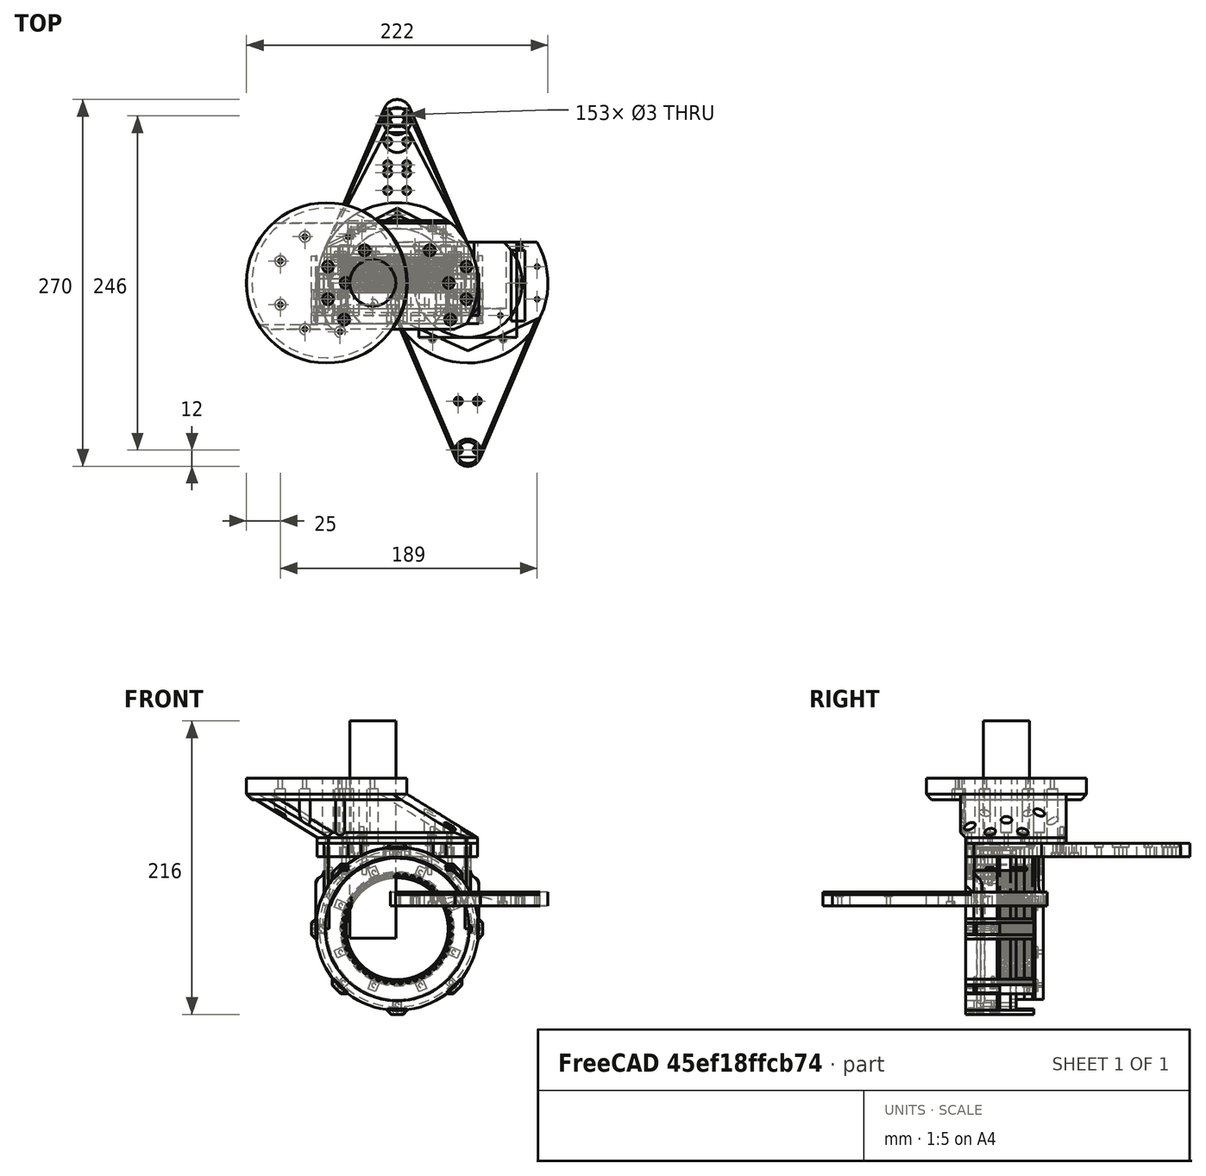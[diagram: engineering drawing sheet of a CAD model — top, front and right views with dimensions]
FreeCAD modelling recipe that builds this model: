
FCSTD DOCUMENT  (FreeCAD 0.19R24276 (Git))
Label: Base_triangle_014
License: All rights reserved
LicenseURL: http://en.wikipedia.org/wiki/All_rights_reserved
objects: Part::Cylinder×647, Part::Compound×283, Part::Cut×229, Part::Box×183, Part::Chamfer×32, Part::FeaturePython×15, Part::Fillet×14, Sketcher::SketchObject×7, PartDesign::Pad×6, PartDesign::Body×6, Part::Common×3, Mesh::Feature×2, Part::Torus×1, Part::Extrusion×1
note: 1433 computed .brp shape members not serialized (recipe doc carries the construction recipe); baked Part::Feature solids carry a one-line shape summary decoded from their .brp

FEATURE [Part::Cylinder] Cylinder284  label="Válec284"
  Angle = 360
  AttacherType = Attacher::AttachEngine3D
  Height = 10
  Placement = pos=(0,106,0) rot=(0,0,1;0rad)
  Radius = 10
FEATURE [Part::Box] Box135  label="Krychle135"
  AttacherType = Attacher::AttachEngine3D
  Height = 32
  Length = 200
  Placement = pos=(-100,-124,0) rot=(0,0,1;0rad)
  Width = 100
FEATURE [Part::Box] Box136  label="Krychle136"
  AttacherType = Attacher::AttachEngine3D
  Height = 10
  Length = 10
  Placement = pos=(32,-24,0) rot=(0,0,1;0rad)
  Width = 52
FEATURE [Part::FeaturePython] Tube  # WARN: FeaturePython — macro-defined, semantics opaque (R4)
  AttacherType = Attacher::AttachEngine3D
  Height = 10
  InnerRadius = 40
  OuterRadius = 59
FEATURE [Part::Cylinder] Cylinder292  label="Válec292"
  Angle = 360
  AttacherType = Attacher::AttachEngine3D
  Height = 100
  Placement = pos=(51,-12,0) rot=(0,0,1;0rad)
  Radius = 1.5
FEATURE [Part::Cylinder] Cylinder312  label="Válec312"
  Angle = 360
  AttacherType = Attacher::AttachEngine3D
  Height = 4
  Placement = pos=(34,36,-1) rot=(0,0,1;0rad)
  Radius = 3
FEATURE [Part::Cylinder] Cylinder311  label="Válec311"
  Angle = 360
  AttacherType = Attacher::AttachEngine3D
  Height = 4
  Placement = pos=(-34,36,-1) rot=(0,0,1;0rad)
  Radius = 3
FEATURE [Part::Compound] Compound290
  Links = -> [Cylinder312,Cylinder311]
FEATURE [Part::Cut] Cut136
  Base = -> Tube
  Tool = -> Compound290
FEATURE [Part::Box] Box137  label="Krychle137"
  AttacherType = Attacher::AttachEngine3D
  Height = 10
  Length = 10
  Placement = pos=(-42,-24,0) rot=(0,0,1;0rad)
  Width = 52
FEATURE [Part::Box] Box138  label="Krychle138"
  AttacherType = Attacher::AttachEngine3D
  Height = 10
  Length = 72
  Placement = pos=(-36,10,0) rot=(0,0,1;0rad)
  Width = 34
FEATURE [Part::Cylinder] Cylinder291  label="Válec291"
  Angle = 360
  AttacherType = Attacher::AttachEngine3D
  Height = 100
  Placement = pos=(-51,-12,0) rot=(0,0,1;0rad)
  Radius = 1.5
FEATURE [Part::Compound] Compound292
  Links = -> [Cylinder291,Cylinder292]
FEATURE [Part::Cylinder] Cylinder324  label="Válec324"
  Angle = 360
  AttacherType = Attacher::AttachEngine3D
  Height = 4
  Placement = pos=(51,7,0) rot=(0,0,1;0rad)
  Radius = 3
FEATURE [Part::Cylinder] Cylinder325  label="Válec325"
  Angle = 360
  AttacherType = Attacher::AttachEngine3D
  Height = 4
  Placement = pos=(-24,18,0) rot=(0,0,1;0rad)
  Radius = 3
FEATURE [Part::Cylinder] Cylinder326  label="Válec326"
  Angle = 360
  AttacherType = Attacher::AttachEngine3D
  Height = 4
  Placement = pos=(24,18,0) rot=(0,0,1;0rad)
  Radius = 3
FEATURE [Part::Cylinder] Cylinder315  label="Válec315"
  Angle = 360
  AttacherType = Attacher::AttachEngine3D
  Height = 4
  Placement = pos=(-51,-16,0) rot=(0,0,1;0rad)
  Radius = 3
FEATURE [Part::Cylinder] Cylinder314  label="Válec314"
  Angle = 360
  AttacherType = Attacher::AttachEngine3D
  Height = 50
  Placement = pos=(-34,36,0) rot=(0,0,1;0rad)
  Radius = 1.5
FEATURE [Part::Cylinder] Cylinder328  label="Válec328"
  Angle = 360
  AttacherType = Attacher::AttachEngine3D
  Height = 50
  Placement = pos=(-51,6,0) rot=(0,0,1;0rad)
  Radius = 1.5
FEATURE [Part::Cylinder] Cylinder327  label="Válec327"
  Angle = 360
  AttacherType = Attacher::AttachEngine3D
  Height = 4
  Placement = pos=(-24,18,0) rot=(0,0,1;0rad)
  Radius = 3
FEATURE [Part::Cylinder] Cylinder319  label="Válec319"
  Angle = 360
  AttacherType = Attacher::AttachEngine3D
  Height = 50
  Placement = pos=(51,6,0) rot=(0,0,1;0rad)
  Radius = 1.5
FEATURE [Part::Cylinder] Cylinder313  label="Válec313"
  Angle = 360
  AttacherType = Attacher::AttachEngine3D
  Height = 50
  Placement = pos=(34,36,0) rot=(0,0,1;0rad)
  Radius = 1.5
FEATURE [Part::Compound] Compound291
  Links = -> [Cylinder314,Cylinder313]
FEATURE [Part::Cylinder] Cylinder323  label="Válec323"
  Angle = 360
  AttacherType = Attacher::AttachEngine3D
  Height = 4
  Placement = pos=(-51,7,0) rot=(0,0,1;0rad)
  Radius = 3
FEATURE [Part::Compound] Compound296
  Links = -> [Cylinder324,Cylinder323,Cylinder325,Cylinder326]
  Placement = pos=(0,0,8) rot=(0,0,1;0rad)
FEATURE [Part::Cylinder] Cylinder329  label="Válec329"
  Angle = 360
  AttacherType = Attacher::AttachEngine3D
  Height = 50
  Placement = pos=(51,6,0) rot=(0,0,1;0rad)
  Radius = 1.5
FEATURE [Part::Cylinder] Cylinder330  label="Válec330"
  Angle = 360
  AttacherType = Attacher::AttachEngine3D
  Height = 50
  Placement = pos=(-24,18,0) rot=(0,0,1;0rad)
  Radius = 1.5
FEATURE [Part::Cylinder] Cylinder316  label="Válec316"
  Angle = 360
  AttacherType = Attacher::AttachEngine3D
  Height = 4
  Placement = pos=(51,-16,0) rot=(0,0,1;0rad)
  Radius = 3
FEATURE [Part::Compound] Compound293
  Links = -> [Cylinder315,Cylinder316]
  Placement = pos=(0,0,25) rot=(0,0,1;0rad)
FEATURE [Part::Cylinder] Cylinder320  label="Válec320"
  Angle = 360
  AttacherType = Attacher::AttachEngine3D
  Height = 50
  Placement = pos=(-51,6,0) rot=(0,0,1;0rad)
  Radius = 1.5
FEATURE [Part::Cylinder] Cylinder321  label="Válec321"
  Angle = 360
  AttacherType = Attacher::AttachEngine3D
  Height = 50
  Placement = pos=(-24,18,0) rot=(0,0,1;0rad)
  Radius = 1.5
FEATURE [Part::Cylinder] Cylinder322  label="Válec322"
  Angle = 360
  AttacherType = Attacher::AttachEngine3D
  Height = 50
  Placement = pos=(24,18,0) rot=(0,0,1;0rad)
  Radius = 1.5
FEATURE [Part::Compound] Compound295
  Links = -> [Cylinder319,Cylinder320,Cylinder321,Cylinder322]
FEATURE [Part::Cut] Cut137
  Base = -> Cut136
  Tool = -> Compound291
FEATURE [Part::Cut] Cut138
  Base = -> Cut137
  Tool = -> Compound293
FEATURE [Part::Cut] Cut139
  Base = -> Cut138
  Tool = -> Compound292
FEATURE [Part::Cylinder] Cylinder334  label="Válec334"
  Angle = 360
  AttacherType = Attacher::AttachEngine3D
  Height = 4
  Placement = pos=(24,18,0) rot=(0,0,1;0rad)
  Radius = 3
FEATURE [Part::Compound] Compound298
  Links = -> [Cylinder327,Cylinder334]
  Placement = pos=(0,0,7) rot=(0,0,1;0rad)
FEATURE [Part::Cut] Cut142
  Base = -> Cut139
  Tool = -> Compound298
FEATURE [Part::Cylinder] Cylinder331  label="Válec331"
  Angle = 360
  AttacherType = Attacher::AttachEngine3D
  Height = 50
  Placement = pos=(24,18,0) rot=(0,0,1;0rad)
  Radius = 1.5
FEATURE [Part::Compound] Compound297
  Links = -> [Cylinder329,Cylinder328,Cylinder330,Cylinder331]
FEATURE [Part::Cut] Cut143
  Base = -> Cut142
  Tool = -> Compound297
FEATURE [Part::Cut] Cut144
  Base = -> Cut143
  Tool = -> Box135
FEATURE [Part::Cylinder] Cylinder297  label="Válec297"
  Angle = 360
  AttacherType = Attacher::AttachEngine3D
  Height = 4
  Placement = pos=(34,36,-1) rot=(0,0,1;0rad)
  Radius = 3
FEATURE [Part::Cylinder] Cylinder363  label="Válec363"
  Angle = 360
  AttacherType = Attacher::AttachEngine3D
  Height = 4
  Placement = pos=(0,50,-1) rot=(0,0,1;0rad)
  Radius = 3
FEATURE [Part::Cut] Cut153
  Base = -> Cut144
  Tool = -> Cylinder363
FEATURE [Part::Cylinder] Cylinder364  label="Válec364"
  Angle = 360
  AttacherType = Attacher::AttachEngine3D
  Height = 50
  Placement = pos=(0,50,0) rot=(0,0,1;0rad)
  Radius = 1.5
FEATURE [Part::Cut] Cut154
  Base = -> Cut153
  Tool = -> Cylinder364
FEATURE [Part::Cylinder] Cylinder298  label="Válec298"
  Angle = 360
  AttacherType = Attacher::AttachEngine3D
  Height = 4
  Placement = pos=(-34,36,-1) rot=(0,0,1;0rad)
  Radius = 3
FEATURE [Part::Compound] Compound282
  Links = -> [Cylinder298,Cylinder297]
FEATURE [Part::Cut] Cut131
  Base = -> Box138
  Tool = -> Compound282
FEATURE [Part::Cylinder] Cylinder294  label="Válec294"
  Angle = 360
  AttacherType = Attacher::AttachEngine3D
  Height = 50
  Placement = pos=(-34,36,0) rot=(0,0,1;0rad)
  Radius = 1.5
FEATURE [Part::Cylinder] Cylinder293  label="Válec293"
  Angle = 360
  AttacherType = Attacher::AttachEngine3D
  Height = 50
  Placement = pos=(34,36,0) rot=(0,0,1;0rad)
  Radius = 1.5
FEATURE [Part::Compound] Compound284
  Links = -> [Cylinder294,Cylinder293]
FEATURE [Part::Cut] Cut132
  Base = -> Cut131
  Tool = -> Compound284
FEATURE [Part::Cut] Cut140
  Base = -> Cut132
  Tool = -> Compound296
FEATURE [Part::Cut] Cut141
  Base = -> Cut140
  Tool = -> Compound295
FEATURE [Part::Cylinder] Cylinder424  label="Válec424"
  Angle = 360
  AttacherType = Attacher::AttachEngine3D
  Height = 4
  Placement = pos=(-7,-34,73) rot=(1,0,0;1.5708rad)
  Radius = 3
FEATURE [Part::Cylinder] Cylinder413  label="Válec413"
  Angle = 360
  AttacherType = Attacher::AttachEngine3D
  Height = 20
  Placement = pos=(7,-34,37) rot=(1,0,0;1.5708rad)
  Radius = 1.5
FEATURE [Part::Cylinder] Cylinder414  label="Válec414"
  Angle = 360
  AttacherType = Attacher::AttachEngine3D
  Height = 20
  Placement = pos=(7,-34,73) rot=(1,0,0;1.5708rad)
  Radius = 1.5
FEATURE [Part::Cylinder] Cylinder415  label="Válec415"
  Angle = 360
  AttacherType = Attacher::AttachEngine3D
  Height = 20
  Placement = pos=(-7,-34,37) rot=(1,0,0;1.5708rad)
  Radius = 1.5
FEATURE [Part::Cylinder] Cylinder412  label="Válec412"
  Angle = 360
  AttacherType = Attacher::AttachEngine3D
  Height = 20
  Placement = pos=(-7,-34,73) rot=(1,0,0;1.5708rad)
  Radius = 1.5
FEATURE [Part::Compound] Compound317
  Links = -> [Cylinder413,Cylinder415,Cylinder414,Cylinder412]
  Placement = pos=(0,141,45) rot=(1,0,0;1.5708rad)
FEATURE [Part::Cut] Cut166
  Base = -> Cylinder284
  Tool = -> Compound317
FEATURE [Part::Cylinder] Cylinder427  label="Válec427"
  Angle = 360
  AttacherType = Attacher::AttachEngine3D
  Height = 4
  Placement = pos=(-7,-34,37) rot=(1,0,0;1.5708rad)
  Radius = 3
FEATURE [Part::Cylinder] Cylinder426  label="Válec426"
  Angle = 360
  AttacherType = Attacher::AttachEngine3D
  Height = 4
  Placement = pos=(7,-34,73) rot=(1,0,0;1.5708rad)
  Radius = 3
FEATURE [Part::Cylinder] Cylinder425  label="Válec425"
  Angle = 360
  AttacherType = Attacher::AttachEngine3D
  Height = 4
  Placement = pos=(7,-34,37) rot=(1,0,0;1.5708rad)
  Radius = 3
FEATURE [Part::Compound] Compound320
  Links = -> [Cylinder425,Cylinder427,Cylinder426,Cylinder424]
  Placement = pos=(0,141,45) rot=(1,0,0;1.5708rad)
FEATURE [Part::Cut] Cut168
  Base = -> Cut166
  Tool = -> Compound320
FEATURE [Sketcher::SketchObject] Sketch
  FullyConstrained = false
  MapMode = 5
  Support = -> [XY_Plane]
  sketch-geometry (5):
    g0: LineSegment StartX=-51.8839 StartY=28.0157 StartZ=0 EndX=-8.82571 EndY=110.528 EndZ=0
    g1: LineSegment StartX=-8.82571 StartY=110.528 StartZ=0 EndX=8.88346 EndY=110.528 EndZ=0
    g2: LineSegment StartX=8.88346 StartY=110.528 StartZ=0 EndX=51.7746 EndY=28.1985 EndZ=0
    g3: LineSegment StartX=51.7746 StartY=28.1985 StartZ=0 EndX=0 EndY=55.1408 EndZ=0
    g4: LineSegment StartX=0 StartY=55.1408 StartZ=0 EndX=-51.8839 EndY=28.0157 EndZ=0
  constraints (7):
    c: Coincident(g0,g1)
    c: Horizontal(g1)
    c: Coincident(g1,g2)
    c: Coincident(g2,g3)
    c: PointOnObject(g3,g-2)
    c: Coincident(g3,g4)
    c: Coincident(g4,g0)
FEATURE [PartDesign::Pad] Pad
  Direction = (1,1,1)
  Length = 10
  Length2 = 100
  Profile = -> Sketch
  Type = 0
FEATURE [PartDesign::Body] Body
  Group = -> [Sketch,Pad]
  Origin = -> Origin
  Tip = -> Pad
FEATURE [Part::Cylinder] Cylinder307  label="Válec307"
  Angle = 360
  AttacherType = Attacher::AttachEngine3D
  Height = 4
  Placement = pos=(-34,36,-1) rot=(0,0,1;0rad)
  Radius = 3
FEATURE [Part::Cylinder] Cylinder308  label="Válec308"
  Angle = 360
  AttacherType = Attacher::AttachEngine3D
  Height = 4
  Placement = pos=(34,36,-1) rot=(0,0,1;0rad)
  Radius = 3
FEATURE [Part::Compound] Compound288
  Links = -> [Cylinder308,Cylinder307]
FEATURE [Part::Cut] Cut134
  Base = -> Body
  Tool = -> Compound288
FEATURE [Part::Cylinder] Cylinder309  label="Válec309"
  Angle = 360
  AttacherType = Attacher::AttachEngine3D
  Height = 50
  Placement = pos=(34,36,0) rot=(0,0,1;0rad)
  Radius = 1.5
FEATURE [Part::Cylinder] Cylinder310  label="Válec310"
  Angle = 360
  AttacherType = Attacher::AttachEngine3D
  Height = 50
  Placement = pos=(-34,36,0) rot=(0,0,1;0rad)
  Radius = 1.5
FEATURE [Part::Compound] Compound289
  Links = -> [Cylinder310,Cylinder309]
FEATURE [Part::Cut] Cut135
  Base = -> Cut134
  Tool = -> Compound289
FEATURE [Part::Cylinder] Cylinder421  label="Válec421"
  Angle = 360
  AttacherType = Attacher::AttachEngine3D
  Height = 4
  Placement = pos=(7,-34,37) rot=(1,0,0;1.5708rad)
  Radius = 3
FEATURE [Part::Cylinder] Cylinder419  label="Válec419"
  Angle = 360
  AttacherType = Attacher::AttachEngine3D
  Height = 20
  Placement = pos=(-7,-34,37) rot=(1,0,0;1.5708rad)
  Radius = 1.5
FEATURE [Part::Cylinder] Cylinder417  label="Válec417"
  Angle = 360
  AttacherType = Attacher::AttachEngine3D
  Height = 20
  Placement = pos=(7,-34,37) rot=(1,0,0;1.5708rad)
  Radius = 1.5
FEATURE [Part::Cylinder] Cylinder418  label="Válec418"
  Angle = 360
  AttacherType = Attacher::AttachEngine3D
  Height = 20
  Placement = pos=(7,-34,73) rot=(1,0,0;1.5708rad)
  Radius = 1.5
FEATURE [Part::Cylinder] Cylinder416  label="Válec416"
  Angle = 360
  AttacherType = Attacher::AttachEngine3D
  Height = 20
  Placement = pos=(-7,-34,73) rot=(1,0,0;1.5708rad)
  Radius = 1.5
FEATURE [Part::Compound] Compound318
  Links = -> [Cylinder417,Cylinder419,Cylinder418,Cylinder416]
  Placement = pos=(0,141,45) rot=(1,0,0;1.5708rad)
FEATURE [Part::Cut] Cut165
  Base = -> Cut135
  Tool = -> Compound318
FEATURE [Part::Cylinder] Cylinder420  label="Válec420"
  Angle = 360
  AttacherType = Attacher::AttachEngine3D
  Height = 4
  Placement = pos=(-7,-34,73) rot=(1,0,0;1.5708rad)
  Radius = 3
FEATURE [Part::Cylinder] Cylinder423  label="Válec423"
  Angle = 360
  AttacherType = Attacher::AttachEngine3D
  Height = 4
  Placement = pos=(-7,-34,37) rot=(1,0,0;1.5708rad)
  Radius = 3
FEATURE [Part::Cylinder] Cylinder422  label="Válec422"
  Angle = 360
  AttacherType = Attacher::AttachEngine3D
  Height = 4
  Placement = pos=(7,-34,73) rot=(1,0,0;1.5708rad)
  Radius = 3
FEATURE [Part::Compound] Compound319
  Links = -> [Cylinder421,Cylinder423,Cylinder422,Cylinder420]
  Placement = pos=(0,141,45) rot=(1,0,0;1.5708rad)
FEATURE [Part::Cut] Cut167
  Base = -> Cut165
  Tool = -> Compound319
FEATURE [Part::Cylinder] Cylinder531  label="Válec531"
  Angle = 360
  AttacherType = Attacher::AttachEngine3D
  Height = 100
  Placement = pos=(39,-21,0) rot=(0,0,1;0rad)
  Radius = 1.5
FEATURE [Part::Cylinder] Cylinder530  label="Válec530"
  Angle = 360
  AttacherType = Attacher::AttachEngine3D
  Height = 100
  Placement = pos=(-39,-21,0) rot=(0,0,1;0rad)
  Radius = 1.5
FEATURE [Part::Compound] Compound308
  Links = -> [Cylinder530,Cylinder531]
FEATURE [Part::Cylinder] Cylinder532  label="Válec532"
  Angle = 360
  AttacherType = Attacher::AttachEngine3D
  Height = 100
  Placement = pos=(-39,-21,0) rot=(0,0,1;0rad)
  Radius = 1.5
FEATURE [Part::Cylinder] Cylinder533  label="Válec533"
  Angle = 360
  AttacherType = Attacher::AttachEngine3D
  Height = 100
  Placement = pos=(39,-21,0) rot=(0,0,1;0rad)
  Radius = 1.5
FEATURE [Part::Compound] Compound321
  Links = -> [Cylinder532,Cylinder533]
FEATURE [Part::Compound] Compound
  Links = -> [Box136,Box137]
FEATURE [Part::Cut] Cut
  Base = -> Compound
  Tool = -> Compound321
FEATURE [Part::Cut] Cut169
  Base = -> Cut154
  Tool = -> Compound308
FEATURE [Part::Compound] Compound322  label="bazovina_part-A_trojuhelnikovina"
  Links = -> [Cut141,Cut168,Cut167,Cut,Cut169]
FEATURE [Sketcher::SketchObject] Sketch001
  FullyConstrained = false
  MapMode = 5
  Support = -> [XY_Plane001]
  sketch-geometry (5):
    g0: LineSegment StartX=-51.8839 StartY=28.0157 StartZ=0 EndX=-9.41248 EndY=122.349 EndZ=0
    g1: LineSegment StartX=-9.41248 StartY=122.349 StartZ=0 EndX=9.41746 EndY=122.349 EndZ=0
    g2: LineSegment StartX=9.41746 StartY=122.349 StartZ=0 EndX=51.7746 EndY=28.1985 EndZ=0
    g3: LineSegment StartX=51.7746 StartY=28.1985 StartZ=0 EndX=0 EndY=55.1408 EndZ=0
    g4: LineSegment StartX=0 StartY=55.1408 StartZ=0 EndX=-51.8839 EndY=28.0157 EndZ=0
  constraints (7):
    c: Coincident(g0,g1)
    c: Horizontal(g1)
    c: Coincident(g1,g2)
    c: Coincident(g2,g3)
    c: PointOnObject(g3,g-2)
    c: Coincident(g3,g4)
    c: Coincident(g4,g0)
FEATURE [Part::Cylinder] Cylinder534  label="Válec534"
  Angle = 360
  AttacherType = Attacher::AttachEngine3D
  Height = 10
  Placement = pos=(0,106,0) rot=(0,0,1;0rad)
  Radius = 10
FEATURE [Part::Box] Box139  label="Krychle139"
  AttacherType = Attacher::AttachEngine3D
  Height = 32
  Length = 200
  Placement = pos=(-100,-124,0) rot=(0,0,1;0rad)
  Width = 100
FEATURE [Part::Box] Box140  label="Krychle140"
  AttacherType = Attacher::AttachEngine3D
  Height = 10
  Length = 10
  Placement = pos=(32,-24,0) rot=(0,0,1;0rad)
  Width = 52
FEATURE [Part::Cylinder] Cylinder535  label="Válec535"
  Angle = 360
  AttacherType = Attacher::AttachEngine3D
  Height = 100
  Placement = pos=(51,-12,0) rot=(0,0,1;0rad)
  Radius = 1.5
FEATURE [Part::Box] Box141  label="Krychle141"
  AttacherType = Attacher::AttachEngine3D
  Height = 10
  Length = 10
  Placement = pos=(-42,-24,0) rot=(0,0,1;0rad)
  Width = 52
FEATURE [Part::Box] Box142  label="Krychle142"
  AttacherType = Attacher::AttachEngine3D
  Height = 10
  Length = 72
  Placement = pos=(-36,-24,0) rot=(0,0,1;0rad)
  Width = 70
FEATURE [Part::Cylinder] Cylinder538  label="Válec538"
  Angle = 360
  AttacherType = Attacher::AttachEngine3D
  Height = 100
  Placement = pos=(-51,-12,0) rot=(0,0,1;0rad)
  Radius = 1.5
FEATURE [Part::Compound] Compound323
  Links = -> [Cylinder538,Cylinder535]
FEATURE [PartDesign::Pad] Pad001
  Direction = (1,1,1)
  Length = 10
  Length2 = 100
  Profile = -> Sketch001
  Type = 0
FEATURE [Part::FeaturePython] Tube001  # WARN: FeaturePython — macro-defined, semantics opaque (R4)
  AttacherType = Attacher::AttachEngine3D
  Height = 10
  InnerRadius = 40
  OuterRadius = 59
FEATURE [PartDesign::Body] Body001
  Group = -> [Sketch001,Pad001]
  Origin = -> Origin001
  Tip = -> Pad001
FEATURE [Part::Cylinder] Cylinder544  label="Válec544"
  Angle = 360
  AttacherType = Attacher::AttachEngine3D
  Height = 50
  Placement = pos=(-51,6,0) rot=(0,0,1;0rad)
  Radius = 1.5
FEATURE [Part::Cylinder] Cylinder549  label="Válec549"
  Angle = 360
  AttacherType = Attacher::AttachEngine3D
  Height = 50
  Placement = pos=(51,6,0) rot=(0,0,1;0rad)
  Radius = 1.5
FEATURE [Part::Cylinder] Cylinder550  label="Válec550"
  Angle = 360
  AttacherType = Attacher::AttachEngine3D
  Height = 50
  Placement = pos=(-24,18,0) rot=(0,0,1;0rad)
  Radius = 1.5
FEATURE [Part::Cylinder] Cylinder556  label="Válec556"
  Angle = 360
  AttacherType = Attacher::AttachEngine3D
  Height = 50
  Placement = pos=(24,18,0) rot=(0,0,1;0rad)
  Radius = 1.5
FEATURE [Part::Compound] Compound324
  Links = -> [Cylinder549,Cylinder544,Cylinder550,Cylinder556]
FEATURE [Part::Cylinder] Cylinder563  label="Válec563"
  Angle = 360
  AttacherType = Attacher::AttachEngine3D
  Height = 4
  Placement = pos=(-7,-34,73) rot=(1,0,0;1.5708rad)
  Radius = 3
FEATURE [Part::Cylinder] Cylinder564  label="Válec564"
  Angle = 360
  AttacherType = Attacher::AttachEngine3D
  Height = 20
  Placement = pos=(7,-34,37) rot=(1,0,0;1.5708rad)
  Radius = 1.5
FEATURE [Part::Cylinder] Cylinder565  label="Válec565"
  Angle = 360
  AttacherType = Attacher::AttachEngine3D
  Height = 20
  Placement = pos=(7,-34,73) rot=(1,0,0;1.5708rad)
  Radius = 1.5
FEATURE [Part::Cylinder] Cylinder566  label="Válec566"
  Angle = 360
  AttacherType = Attacher::AttachEngine3D
  Height = 20
  Placement = pos=(-7,-34,37) rot=(1,0,0;1.5708rad)
  Radius = 1.5
FEATURE [Part::Cylinder] Cylinder567  label="Válec567"
  Angle = 360
  AttacherType = Attacher::AttachEngine3D
  Height = 20
  Placement = pos=(-7,-34,73) rot=(1,0,0;1.5708rad)
  Radius = 1.5
FEATURE [Part::Compound] Compound333
  Links = -> [Cylinder564,Cylinder566,Cylinder565,Cylinder567]
  Placement = pos=(0,141,45) rot=(1,0,0;1.5708rad)
FEATURE [Part::Cut] Cut189
  Base = -> Cylinder534
  Tool = -> Compound333
FEATURE [Part::Cylinder] Cylinder568  label="Válec568"
  Angle = 360
  AttacherType = Attacher::AttachEngine3D
  Height = 4
  Placement = pos=(-7,-34,37) rot=(1,0,0;1.5708rad)
  Radius = 3
FEATURE [Part::Cylinder] Cylinder569  label="Válec569"
  Angle = 360
  AttacherType = Attacher::AttachEngine3D
  Height = 4
  Placement = pos=(7,-34,73) rot=(1,0,0;1.5708rad)
  Radius = 3
FEATURE [Part::Cylinder] Cylinder570  label="Válec570"
  Angle = 360
  AttacherType = Attacher::AttachEngine3D
  Height = 4
  Placement = pos=(7,-34,37) rot=(1,0,0;1.5708rad)
  Radius = 3
FEATURE [Part::Compound] Compound332
  Links = -> [Cylinder570,Cylinder568,Cylinder569,Cylinder563]
  Placement = pos=(0,141,45) rot=(1,0,0;1.5708rad)
FEATURE [Part::Cut] Cut190
  Base = -> Cut189
  Placement = pos=(0,13,0) rot=(0,0,1;0rad)
  Tool = -> Compound332
FEATURE [Part::Cylinder] Cylinder575  label="Válec575"
  Angle = 360
  AttacherType = Attacher::AttachEngine3D
  Height = 4
  Placement = pos=(7,-34,37) rot=(1,0,0;1.5708rad)
  Radius = 3
FEATURE [Part::Cylinder] Cylinder576  label="Válec576"
  Angle = 360
  AttacherType = Attacher::AttachEngine3D
  Height = 20
  Placement = pos=(-7,-34,37) rot=(1,0,0;1.5708rad)
  Radius = 1.5
FEATURE [Part::Compound] Compound341
  Links = -> [Box140,Box141]
FEATURE [Part::Cylinder] Cylinder577  label="Válec577"
  Angle = 360
  AttacherType = Attacher::AttachEngine3D
  Height = 20
  Placement = pos=(7,-34,37) rot=(1,0,0;1.5708rad)
  Radius = 1.5
FEATURE [Part::Cylinder] Cylinder578  label="Válec578"
  Angle = 360
  AttacherType = Attacher::AttachEngine3D
  Height = 20
  Placement = pos=(7,-34,73) rot=(1,0,0;1.5708rad)
  Radius = 1.5
FEATURE [Part::Cylinder] Cylinder579  label="Válec579"
  Angle = 360
  AttacherType = Attacher::AttachEngine3D
  Height = 20
  Placement = pos=(-7,-34,73) rot=(1,0,0;1.5708rad)
  Radius = 1.5
FEATURE [Part::Compound] Compound337
  Links = -> [Cylinder577,Cylinder576,Cylinder578,Cylinder579]
  Placement = pos=(0,154,45) rot=(1,0,0;1.5708rad)
FEATURE [Part::Cylinder] Cylinder580  label="Válec580"
  Angle = 360
  AttacherType = Attacher::AttachEngine3D
  Height = 4
  Placement = pos=(-7,-34,73) rot=(1,0,0;1.5708rad)
  Radius = 3
FEATURE [Part::Cylinder] Cylinder581  label="Válec581"
  Angle = 360
  AttacherType = Attacher::AttachEngine3D
  Height = 4
  Placement = pos=(-7,-34,37) rot=(1,0,0;1.5708rad)
  Radius = 3
FEATURE [Part::Cylinder] Cylinder582  label="Válec582"
  Angle = 360
  AttacherType = Attacher::AttachEngine3D
  Height = 4
  Placement = pos=(7,-34,73) rot=(1,0,0;1.5708rad)
  Radius = 3
FEATURE [Part::Compound] Compound338
  Links = -> [Cylinder575,Cylinder581,Cylinder582,Cylinder580]
  Placement = pos=(0,154,45) rot=(1,0,0;1.5708rad)
FEATURE [Part::Cylinder] Cylinder583  label="Válec583"
  Angle = 360
  AttacherType = Attacher::AttachEngine3D
  Height = 100
  Placement = pos=(39,-21,0) rot=(0,0,1;0rad)
  Radius = 1.5
FEATURE [Part::Cylinder] Cylinder584  label="Válec584"
  Angle = 360
  AttacherType = Attacher::AttachEngine3D
  Height = 100
  Placement = pos=(-39,-21,0) rot=(0,0,1;0rad)
  Radius = 1.5
FEATURE [Part::Compound] Compound339
  Links = -> [Cylinder584,Cylinder583]
FEATURE [Part::Cylinder] Cylinder585  label="Válec585"
  Angle = 360
  AttacherType = Attacher::AttachEngine3D
  Height = 100
  Placement = pos=(-39,-21,0) rot=(0,0,1;0rad)
  Radius = 1.5
FEATURE [Part::Cylinder] Cylinder586  label="Válec586"
  Angle = 360
  AttacherType = Attacher::AttachEngine3D
  Height = 100
  Placement = pos=(39,-21,0) rot=(0,0,1;0rad)
  Radius = 1.5
FEATURE [Part::Compound] Compound340
  Links = -> [Cylinder585,Cylinder586]
FEATURE [Part::Cut] Cut173
  Base = -> Compound341
  Tool = -> Compound340
FEATURE [Part::Box] Box236  label="Krychle236"
  AttacherType = Attacher::AttachEngine3D
  Height = 64
  Length = 6
  Placement = pos=(11,-3,-93) rot=(0,0,1;0rad)
  Width = 6
FEATURE [Part::Box] Box237  label="Krychle237"
  AttacherType = Attacher::AttachEngine3D
  Height = 64
  Length = 6
  Placement = pos=(87,-3,-93) rot=(0,0,1;0rad)
  Width = 6
FEATURE [Part::Compound] Compound627
  Links = -> [Box236,Box237]
  Placement = pos=(-52,0,36) rot=(0,0,1;0rad)
FEATURE [Part::Cylinder] Cylinder1238  label="Válec1238"
  Angle = 360
  AttacherType = Attacher::AttachEngine3D
  Height = 100
  Placement = pos=(90,0,-60) rot=(0,0,1;0rad)
  Radius = 1.5
FEATURE [Part::Cylinder] Cylinder1239  label="Válec1239"
  Angle = 360
  AttacherType = Attacher::AttachEngine3D
  Height = 100
  Placement = pos=(14,0,-60) rot=(0,0,1;0rad)
  Radius = 1.5
FEATURE [Part::Compound] Compound625  label="srouby_troj001"
  Links = -> [Cylinder1238,Cylinder1239]
  Placement = pos=(-52,0,0) rot=(0,0,1;0rad)
FEATURE [Part::Cylinder] Cylinder1232  label="Válec1232"
  Angle = 360
  AttacherType = Attacher::AttachEngine3D
  Height = 32
  Placement = pos=(26,41,-42) rot=(0,0,1;0rad)
  Radius = 1.5
FEATURE [Part::Cylinder] Cylinder1233  label="Válec1233"
  Angle = 360
  AttacherType = Attacher::AttachEngine3D
  Height = 32
  Placement = pos=(78,41,-42) rot=(0,0,1;0rad)
  Radius = 1.5
FEATURE [Part::Compound] Compound620
  Links = -> [Cylinder1232,Cylinder1233]
  Placement = pos=(-52,0,36) rot=(0,0,1;0rad)
FEATURE [Part::Cut] Cut191
  Base = -> Tube001
  Tool = -> Box139
FEATURE [Part::Compound] Compound628
  Links = -> [Compound339,Compound324,Compound323]
  Placement = pos=(0,0,-10) rot=(0,0,1;0rad)
FEATURE [Part::Compound] Compound630
  Links = -> [Compound625,Compound620]
FEATURE [Part::Cylinder] Cylinder1242  label="Válec1242"
  Angle = 360
  AttacherType = Attacher::AttachEngine3D
  Height = 3
  Placement = pos=(26,41,-42) rot=(0,0,1;0rad)
  Radius = 3
FEATURE [Part::Cylinder] Cylinder1243  label="Válec1243"
  Angle = 360
  AttacherType = Attacher::AttachEngine3D
  Height = 3
  Placement = pos=(78,41,-42) rot=(0,0,1;0rad)
  Radius = 3
FEATURE [Part::Compound] Compound633
  Links = -> [Cylinder1242,Cylinder1243]
  Placement = pos=(-52,0,42) rot=(0,0,1;0rad)
FEATURE [Part::Cylinder] Cylinder1244  label="Válec1244"
  Angle = 360
  AttacherType = Attacher::AttachEngine3D
  Height = 3
  Placement = pos=(26,41,-42) rot=(0,0,1;0rad)
  Radius = 3
FEATURE [Part::Cylinder] Cylinder1245  label="Válec1245"
  Angle = 360
  AttacherType = Attacher::AttachEngine3D
  Height = 3
  Placement = pos=(78,41,-42) rot=(0,0,1;0rad)
  Radius = 3
FEATURE [Part::Compound] Compound634
  Links = -> [Cylinder1244,Cylinder1245]
  Placement = pos=(-52,0,42) rot=(0,0,1;0rad)
FEATURE [Part::Cut] Cut192
  Base = -> Body001
  Tool = -> Compound337
FEATURE [Part::Cut] Cut193
  Base = -> Cut192
  Tool = -> Compound338
FEATURE [Part::Cylinder] Cylinder1246  label="Válec1246"
  Angle = 360
  AttacherType = Attacher::AttachEngine3D
  Height = 100
  Placement = pos=(51,-12,0) rot=(0,0,1;0rad)
  Radius = 1.5
FEATURE [Part::Cylinder] Cylinder1247  label="Válec1247"
  Angle = 360
  AttacherType = Attacher::AttachEngine3D
  Height = 100
  Placement = pos=(-51,-12,0) rot=(0,0,1;0rad)
  Radius = 1.5
FEATURE [Part::Compound] Compound636
  Links = -> [Cylinder1247,Cylinder1246]
FEATURE [Part::Cylinder] Cylinder1248  label="Válec1248"
  Angle = 360
  AttacherType = Attacher::AttachEngine3D
  Height = 50
  Placement = pos=(-51,6,0) rot=(0,0,1;0rad)
  Radius = 1.5
FEATURE [Part::Cylinder] Cylinder1249  label="Válec1249"
  Angle = 360
  AttacherType = Attacher::AttachEngine3D
  Height = 50
  Placement = pos=(51,6,0) rot=(0,0,1;0rad)
  Radius = 1.5
FEATURE [Part::Cylinder] Cylinder1250  label="Válec1250"
  Angle = 360
  AttacherType = Attacher::AttachEngine3D
  Height = 50
  Placement = pos=(-24,18,0) rot=(0,0,1;0rad)
  Radius = 1.5
FEATURE [Part::Cylinder] Cylinder1251  label="Válec1251"
  Angle = 360
  AttacherType = Attacher::AttachEngine3D
  Height = 50
  Placement = pos=(24,18,0) rot=(0,0,1;0rad)
  Radius = 1.5
FEATURE [Part::Compound] Compound637
  Links = -> [Cylinder1249,Cylinder1248,Cylinder1250,Cylinder1251]
FEATURE [Part::Cylinder] Cylinder1252  label="Válec1252"
  Angle = 360
  AttacherType = Attacher::AttachEngine3D
  Height = 100
  Placement = pos=(39,-21,0) rot=(0,0,1;0rad)
  Radius = 1.5
FEATURE [Part::Cylinder] Cylinder1253  label="Válec1253"
  Angle = 360
  AttacherType = Attacher::AttachEngine3D
  Height = 100
  Placement = pos=(-39,-21,0) rot=(0,0,1;0rad)
  Radius = 1.5
FEATURE [Part::Compound] Compound638
  Links = -> [Cylinder1253,Cylinder1252]
FEATURE [Part::Compound] Compound635
  Links = -> [Compound638,Compound637,Compound636]
  Placement = pos=(0,0,-10) rot=(0,0,1;0rad)
FEATURE [Part::Cut] Cut194
  Base = -> Cut191
  Tool = -> Compound635
FEATURE [Part::Cylinder] Cylinder1254  label="Válec1254"
  Angle = 360
  AttacherType = Attacher::AttachEngine3D
  Height = 100
  Placement = pos=(90,0,-60) rot=(0,0,1;0rad)
  Radius = 1.5
FEATURE [Part::Cylinder] Cylinder1255  label="Válec1255"
  Angle = 360
  AttacherType = Attacher::AttachEngine3D
  Height = 100
  Placement = pos=(14,0,-60) rot=(0,0,1;0rad)
  Radius = 1.5
FEATURE [Part::Compound] Compound640  label="srouby_troj002"
  Links = -> [Cylinder1254,Cylinder1255]
  Placement = pos=(-52,0,0) rot=(0,0,1;0rad)
FEATURE [Part::Cylinder] Cylinder1256  label="Válec1256"
  Angle = 360
  AttacherType = Attacher::AttachEngine3D
  Height = 32
  Placement = pos=(26,41,-42) rot=(0,0,1;0rad)
  Radius = 1.5
FEATURE [Part::Cylinder] Cylinder1257  label="Válec1257"
  Angle = 360
  AttacherType = Attacher::AttachEngine3D
  Height = 32
  Placement = pos=(78,41,-42) rot=(0,0,1;0rad)
  Radius = 1.5
FEATURE [Part::Compound] Compound641
  Links = -> [Cylinder1256,Cylinder1257]
  Placement = pos=(-52,0,36) rot=(0,0,1;0rad)
FEATURE [Part::Compound] Compound639
  Links = -> [Compound640,Compound641]
FEATURE [Part::Cut] Cut195
  Base = -> Cut194
  Tool = -> Compound639
FEATURE [Part::Cut] Cut196
  Base = -> Cut195
  Tool = -> Compound633
FEATURE [Part::Cylinder] Cylinder1258  label="Válec1258"
  Angle = 360
  AttacherType = Attacher::AttachEngine3D
  Height = 3
  Placement = pos=(26,41,-42) rot=(0,0,1;0rad)
  Radius = 3
FEATURE [Part::Cylinder] Cylinder1259  label="Válec1259"
  Angle = 360
  AttacherType = Attacher::AttachEngine3D
  Height = 3
  Placement = pos=(78,41,-42) rot=(0,0,1;0rad)
  Radius = 3
FEATURE [Part::Compound] Compound642
  Links = -> [Cylinder1258,Cylinder1259]
  Placement = pos=(-52,0,42) rot=(0,0,1;0rad)
FEATURE [Part::Cut] Cut197
  Base = -> Cut193
  Tool = -> Compound642
FEATURE [Part::Cut] Cut198
  Base = -> Cut196
  Tool = -> Compound627
FEATURE [Part::Cylinder] Cylinder1260  label="Válec1260"
  Angle = 360
  AttacherType = Attacher::AttachEngine3D
  Height = 100
  Placement = pos=(90,0,-60) rot=(0,0,1;0rad)
  Radius = 1.5
FEATURE [Part::Cylinder] Cylinder1261  label="Válec1261"
  Angle = 360
  AttacherType = Attacher::AttachEngine3D
  Height = 100
  Placement = pos=(14,0,-60) rot=(0,0,1;0rad)
  Radius = 1.5
FEATURE [Part::Compound] Compound644  label="srouby_troj003"
  Links = -> [Cylinder1260,Cylinder1261]
  Placement = pos=(-52,0,0) rot=(0,0,1;0rad)
FEATURE [Part::Cylinder] Cylinder1262  label="Válec1262"
  Angle = 360
  AttacherType = Attacher::AttachEngine3D
  Height = 32
  Placement = pos=(26,41,-42) rot=(0,0,1;0rad)
  Radius = 1.5
FEATURE [Part::Cylinder] Cylinder1263  label="Válec1263"
  Angle = 360
  AttacherType = Attacher::AttachEngine3D
  Height = 32
  Placement = pos=(78,41,-42) rot=(0,0,1;0rad)
  Radius = 1.5
FEATURE [Part::Compound] Compound645
  Links = -> [Cylinder1262,Cylinder1263]
  Placement = pos=(-52,0,36) rot=(0,0,1;0rad)
FEATURE [Part::Compound] Compound643
  Links = -> [Compound644,Compound645]
FEATURE [Part::Cut] Cut199
  Base = -> Cut173
  Tool = -> Compound643
FEATURE [Part::Box] Box238  label="Krychle238"
  AttacherType = Attacher::AttachEngine3D
  Height = 64
  Length = 6
  Placement = pos=(11,-3,-93) rot=(0,0,1;0rad)
  Width = 6
FEATURE [Part::Box] Box239  label="Krychle239"
  AttacherType = Attacher::AttachEngine3D
  Height = 64
  Length = 6
  Placement = pos=(87,-3,-93) rot=(0,0,1;0rad)
  Width = 6
FEATURE [Part::Compound] Compound646
  Links = -> [Box238,Box239]
  Placement = pos=(-52,0,36) rot=(0,0,1;0rad)
FEATURE [Part::Cut] Cut200
  Base = -> Cut199
  Tool = -> Compound646
FEATURE [Part::Cut] Cut201
  Base = -> Box142
  Tool = -> Compound628
FEATURE [Part::Cut] Cut202
  Base = -> Cut201
  Tool = -> Compound634
FEATURE [Part::Cut] Cut203
  Base = -> Cut202
  Tool = -> Compound630
FEATURE [Part::Cylinder] Cylinder1264  label="Válec1264"
  Angle = 360
  AttacherType = Attacher::AttachEngine3D
  Height = 100
  Placement = pos=(90,0,-60) rot=(0,0,1;0rad)
  Radius = 1.5
FEATURE [Part::Cylinder] Cylinder1265  label="Válec1265"
  Angle = 360
  AttacherType = Attacher::AttachEngine3D
  Height = 100
  Placement = pos=(14,0,-60) rot=(0,0,1;0rad)
  Radius = 1.5
FEATURE [Part::Compound] Compound648  label="srouby_troj004"
  Links = -> [Cylinder1264,Cylinder1265]
  Placement = pos=(-52,0,0) rot=(0,0,1;0rad)
FEATURE [Part::Cylinder] Cylinder1266  label="Válec1266"
  Angle = 360
  AttacherType = Attacher::AttachEngine3D
  Height = 32
  Placement = pos=(26,41,-42) rot=(0,0,1;0rad)
  Radius = 1.5
FEATURE [Part::Cylinder] Cylinder1267  label="Válec1267"
  Angle = 360
  AttacherType = Attacher::AttachEngine3D
  Height = 32
  Placement = pos=(78,41,-42) rot=(0,0,1;0rad)
  Radius = 1.5
FEATURE [Part::Compound] Compound649
  Links = -> [Cylinder1266,Cylinder1267]
  Placement = pos=(-52,0,36) rot=(0,0,1;0rad)
FEATURE [Part::Compound] Compound647
  Links = -> [Compound648,Compound649]
FEATURE [Part::Cut] Cut204
  Base = -> Cut197
  Tool = -> Compound647
FEATURE [Part::Cylinder] Cylinder490  label="Válec490"
  Angle = 360
  AttacherType = Attacher::AttachEngine3D
  Height = 10
  Radius = 60
FEATURE [Part::Cylinder] Cylinder491  label="Válec491"
  Angle = 360
  AttacherType = Attacher::AttachEngine3D
  Height = 10
  Radius = 52
FEATURE [Part::Cylinder] Cylinder492  label="Válec492"
  Angle = 360
  AttacherType = Attacher::AttachEngine3D
  Height = 20
  Placement = pos=(24,-40,-5) rot=(1,0,0;1.5708rad)
  Radius = 1.5
FEATURE [Part::Box] Box047  label="Krychle047"
  AttacherType = Attacher::AttachEngine3D
  Height = 6
  Length = 6
  Placement = pos=(-27,-47,-8) rot=(0,0,1;0rad)
  Width = 2
FEATURE [Part::Box] Box172  label="Krychle172"
  AttacherType = Attacher::AttachEngine3D
  Height = 6
  Length = 6
  Placement = pos=(48,-45,4) rot=(0,0,1;0rad)
  Width = 2
FEATURE [Part::Cylinder] Cylinder493  label="Válec493"
  Angle = 360
  AttacherType = Attacher::AttachEngine3D
  Height = 10
  Placement = pos=(0,0,20) rot=(0,0,1;0rad)
  Radius = 52
FEATURE [Part::Cylinder] Cylinder494  label="Válec494"
  Angle = 360
  AttacherType = Attacher::AttachEngine3D
  Height = 40
  Placement = pos=(59,-17,0) rot=(0,0,1;0rad)
  Radius = 10
FEATURE [Part::FeaturePython] wormgear027  # WARN: FeaturePython — macro-defined, semantics opaque (R4)
  AttacherType = Attacher::AttachEngine3D
  Placement = pos=(0,0,0) rot=(0,0,1;0.009355rad)
  beta = 29.4806
  clearance = 0.25
  diameter = 79.6
  head = 0
  height = 20
  module = 1
  pressure_angle = 20
  reverse_pitch = false
  teeth = 45
  version = 0.0.3
FEATURE [Part::Cut] Cut056
  Base = -> Cylinder491
  Tool = -> wormgear027
FEATURE [Part::FeaturePython] wormgear026  # WARN: FeaturePython — macro-defined, semantics opaque (R4)
  AttacherType = Attacher::AttachEngine3D
  beta = 29.4806
  clearance = 0.25
  diameter = 79.6
  head = 0
  height = 20
  module = 1
  pressure_angle = 20
  reverse_pitch = true
  teeth = 45
  version = 0.0.3
FEATURE [Part::Cut] Cut057
  Base = -> Cylinder490
  Placement = pos=(0,0,10) rot=(0,0,1;0.034907rad)
  Tool = -> wormgear026
FEATURE [Part::FeaturePython] Tube025  # WARN: FeaturePython — macro-defined, semantics opaque (R4)
  AttacherType = Attacher::AttachEngine3D
  Height = 8
  InnerRadius = 42
  OuterRadius = 52
  Placement = pos=(0,0,-8) rot=(0,0,1;0rad)
FEATURE [Part::Compound] Compound157
  Links = -> [Cut057,Cut056]
FEATURE [Part::Box] Box173  label="Krychle173"
  AttacherType = Attacher::AttachEngine3D
  Height = 6
  Length = 6
  Placement = pos=(21,-47,-8) rot=(0,0,1;0rad)
  Width = 2
FEATURE [Part::Box] Box045  label="Krychle045"
  AttacherType = Attacher::AttachEngine3D
  Height = 10
  Length = 108
  Placement = pos=(-54,-53,20) rot=(0,0,1;0rad)
  Width = 36
FEATURE [Part::Cut] Cut184
  Base = -> Box045
  Placement = pos=(0,0,-20) rot=(0,0,1;0rad)
  Tool = -> Cylinder493
FEATURE [Part::Cylinder] Cylinder495  label="Válec495"
  Angle = 360
  AttacherType = Attacher::AttachEngine3D
  Height = 40
  Placement = pos=(-59,-17,0) rot=(0,0,1;0rad)
  Radius = 10
FEATURE [Part::Compound] Compound163
  Links = -> [Cylinder494,Cylinder495]
FEATURE [Part::Cylinder] Cylinder496  label="Válec496"
  Angle = 360
  AttacherType = Attacher::AttachEngine3D
  Height = 8
  Placement = pos=(0,0,20) rot=(0,0,1;0rad)
  Radius = 52
FEATURE [Part::Box] Box174  label="Krychle174"
  AttacherType = Attacher::AttachEngine3D
  Height = 8
  Length = 108
  Placement = pos=(-54,-53,20) rot=(0,0,1;0rad)
  Width = 36
FEATURE [Part::Cut] Cut183
  Base = -> Box174
  Placement = pos=(0,0,-20) rot=(0,0,1;0rad)
  Tool = -> Cylinder496
FEATURE [Part::Cut] Cut185
  Base = -> Cut183
  Placement = pos=(0,0,-8) rot=(0,0,1;0rad)
  Tool = -> Compound163
FEATURE [Part::Cylinder] Cylinder497  label="Válec497"
  Angle = 360
  AttacherType = Attacher::AttachEngine3D
  Height = 40
  Placement = pos=(-59,-17,0) rot=(0,0,1;0rad)
  Radius = 10
FEATURE [Part::Box] Box046  label="Krychle046"
  AttacherType = Attacher::AttachEngine3D
  Height = 10
  Length = 108
  Placement = pos=(-54,-53,20) rot=(0,0,1;0rad)
  Width = 36
FEATURE [Part::Cylinder] Cylinder498  label="Válec498"
  Angle = 360
  AttacherType = Attacher::AttachEngine3D
  Height = 20
  Placement = pos=(-24,-40,-5) rot=(1,0,0;1.5708rad)
  Radius = 1.5
FEATURE [Part::Cylinder] Cylinder499  label="Válec499"
  Angle = 360
  AttacherType = Attacher::AttachEngine3D
  Height = 40
  Placement = pos=(59,-17,0) rot=(0,0,1;0rad)
  Radius = 10
FEATURE [Part::Compound] Compound162
  Links = -> [Cylinder499,Cylinder497]
FEATURE [Part::Cut] Cut188
  Base = -> Cut184
  Tool = -> Compound162
FEATURE [Part::Cylinder] Cylinder500  label="Válec500"
  Angle = 360
  AttacherType = Attacher::AttachEngine3D
  Height = 10
  Placement = pos=(0,0,20) rot=(0,0,1;0rad)
  Radius = 52
FEATURE [Part::Cut] Cut205
  Base = -> Box046
  Placement = pos=(0,0,-10) rot=(0,0,1;0rad)
  Tool = -> Cylinder500
FEATURE [Part::Cylinder] Cylinder501  label="Válec501"
  Angle = 360
  AttacherType = Attacher::AttachEngine3D
  Height = 20
  Placement = pos=(-51,-40,7) rot=(1,0,0;1.5708rad)
  Radius = 1.5
FEATURE [Part::Cylinder] Cylinder502  label="Válec502"
  Angle = 360
  AttacherType = Attacher::AttachEngine3D
  Height = 20
  Placement = pos=(-39.598,39.598,2) rot=(0,0,1;3.92699rad)
  Radius = 1.5
FEATURE [Part::Cylinder] Cylinder503  label="Válec503"
  Angle = 360
  AttacherType = Attacher::AttachEngine3D
  Height = 20
  Placement = pos=(-39.598,-39.598,2) rot=(0,0,-1;0.785398rad)
  Radius = 1.5
FEATURE [Part::Box] Box051  label="Krychle051"
  AttacherType = Attacher::AttachEngine3D
  Height = 6
  Length = 6
  Placement = pos=(-54,-45,4) rot=(0,0,1;0rad)
  Width = 2
FEATURE [Part::Compound] Compound169
  Links = -> [Box047,Box173,Box172,Box051]
FEATURE [Part::Cylinder] Cylinder504  label="Válec504"
  Angle = 360
  AttacherType = Attacher::AttachEngine3D
  Height = 20
  Placement = pos=(39.598,39.598,2) rot=(0,0,1;2.35619rad)
  Radius = 1.5
FEATURE [Part::Cylinder] Cylinder505  label="Válec505"
  Angle = 360
  AttacherType = Attacher::AttachEngine3D
  Height = 20
  Placement = pos=(56,0,2) rot=(0,0,1;1.5708rad)
  Radius = 1.5
FEATURE [Part::Cylinder] Cylinder154  label="Válec154"
  Angle = 360
  AttacherType = Attacher::AttachEngine3D
  Height = 20
  Placement = pos=(-1.2e-14,56,2) rot=(0,0,1;3.14159rad)
  Radius = 1.5
FEATURE [Part::Cylinder] Cylinder155  label="Válec155"
  Angle = 360
  AttacherType = Attacher::AttachEngine3D
  Height = 20
  Placement = pos=(0,-56,2) rot=(0,0,1;0rad)
  Radius = 1.5
FEATURE [Part::Cylinder] Cylinder506  label="Válec506"
  Angle = 360
  AttacherType = Attacher::AttachEngine3D
  Height = 20
  Placement = pos=(56,0,2) rot=(0,0,1;1.5708rad)
  Radius = 1.5
FEATURE [Part::Cylinder] Cylinder507  label="Válec507"
  Angle = 360
  AttacherType = Attacher::AttachEngine3D
  Height = 20
  Placement = pos=(51,-40,7) rot=(1,0,0;1.5708rad)
  Radius = 1.5
FEATURE [Part::Compound] Compound172
  Links = -> [Cylinder498,Cylinder492,Cylinder507,Cylinder501]
FEATURE [Part::Cylinder] Cylinder508  label="Válec508"
  Angle = 360
  AttacherType = Attacher::AttachEngine3D
  Height = 20
  Placement = pos=(0,-56,2) rot=(0,0,1;0rad)
  Radius = 1.5
FEATURE [Part::Cylinder] Cylinder509  label="Válec509"
  Angle = 360
  AttacherType = Attacher::AttachEngine3D
  Height = 20
  Placement = pos=(-56,-1.3e-14,2) rot=(0,0,-1;1.5708rad)
  Radius = 1.5
FEATURE [Part::Cylinder] Cylinder510  label="Válec510"
  Angle = 360
  AttacherType = Attacher::AttachEngine3D
  Height = 20
  Placement = pos=(-1.2e-14,56,2) rot=(0,0,1;3.14159rad)
  Radius = 1.5
FEATURE [Part::Cylinder] Cylinder511  label="Válec511"
  Angle = 360
  AttacherType = Attacher::AttachEngine3D
  Height = 20
  Placement = pos=(-39.598,39.598,2) rot=(0,0,1;3.92699rad)
  Radius = 1.5
FEATURE [Part::Cylinder] Cylinder512  label="Válec512"
  Angle = 360
  AttacherType = Attacher::AttachEngine3D
  Height = 20
  Placement = pos=(39.598,-39.598,2) rot=(0,0,1;0.785398rad)
  Radius = 1.5
FEATURE [Part::Cylinder] Cylinder513  label="Válec513"
  Angle = 360
  AttacherType = Attacher::AttachEngine3D
  Height = 20
  Placement = pos=(-39.598,-39.598,2) rot=(0,0,-1;0.785398rad)
  Radius = 1.5
FEATURE [Part::Compound] Compound164
  Links = -> [Cylinder508,Cylinder512,Cylinder506,Cylinder504,Cylinder510,Cylinder502,Cylinder509,Cylinder513]
FEATURE [Part::Cut] Cut187
  Base = -> Compound157
  Tool = -> Compound164
FEATURE [Part::Cylinder] Cylinder514  label="Válec514"
  Angle = 360
  AttacherType = Attacher::AttachEngine3D
  Height = 20
  Placement = pos=(-39.6,-39.6,-10) rot=(0,0,-1;0.785398rad)
  Radius = 4
FEATURE [Part::Box] Box057  label="Krychle057"
  AttacherType = Attacher::AttachEngine3D
  Height = 6
  Length = 6
  Placement = pos=(21,-47,-8) rot=(0,0,1;0rad)
  Width = 2
FEATURE [Part::Box] Box058  label="Krychle058"
  AttacherType = Attacher::AttachEngine3D
  Height = 6
  Length = 6
  Placement = pos=(-27,-47,-8) rot=(0,0,1;0rad)
  Width = 2
FEATURE [Part::Cylinder] Cylinder156  label="Válec156"
  Angle = 360
  AttacherType = Attacher::AttachEngine3D
  Height = 20
  Placement = pos=(39.598,39.598,2) rot=(0,0,1;2.35619rad)
  Radius = 1.5
FEATURE [Part::Cylinder] Cylinder515  label="Válec515"
  Angle = 360
  AttacherType = Attacher::AttachEngine3D
  Height = 20
  Placement = pos=(39.6,-39.6,-10) rot=(0,0,1;0.785398rad)
  Radius = 4
FEATURE [Part::Compound] Compound166
  Links = -> [Cylinder514,Cylinder515]
FEATURE [Part::Cut] Cut069
  Base = -> Cut187
  Tool = -> Compound166
FEATURE [Part::Cylinder] Cylinder164  label="Válec164"
  Angle = 360
  AttacherType = Attacher::AttachEngine3D
  Height = 20
  Placement = pos=(-39.6,-39.6,-10) rot=(0,0,-1;0.785398rad)
  Radius = 4
FEATURE [Part::Cylinder] Cylinder162  label="Válec162"
  Angle = 360
  AttacherType = Attacher::AttachEngine3D
  Height = 20
  Placement = pos=(-39.6,-39.6,-10) rot=(0,0,-1;0.785398rad)
  Radius = 4
FEATURE [Part::Cylinder] Cylinder163  label="Válec163"
  Angle = 360
  AttacherType = Attacher::AttachEngine3D
  Height = 20
  Placement = pos=(39.6,-39.6,-10) rot=(0,0,1;0.785398rad)
  Radius = 4
FEATURE [Part::Compound] Compound168
  Links = -> [Cylinder164,Cylinder163]
FEATURE [Part::Cut] Cut071
  Base = -> Cut188
  Tool = -> Compound168
FEATURE [Part::Box] Box052  label="Krychle052"
  AttacherType = Attacher::AttachEngine3D
  Height = 6
  Length = 6
  Placement = pos=(48,-45,4) rot=(0,0,1;0rad)
  Width = 2
FEATURE [Part::Box] Box053  label="Krychle053"
  AttacherType = Attacher::AttachEngine3D
  Height = 6
  Length = 6
  Placement = pos=(17,-47,-8) rot=(0,0,1;0rad)
  Width = 2
FEATURE [Part::Box] Box054  label="Krychle054"
  AttacherType = Attacher::AttachEngine3D
  Height = 6
  Length = 6
  Placement = pos=(-23,-47,-8) rot=(0,0,1;0rad)
  Width = 2
FEATURE [Part::Cylinder] Cylinder161  label="Válec161"
  Angle = 360
  AttacherType = Attacher::AttachEngine3D
  Height = 20
  Placement = pos=(39.6,-39.6,-10) rot=(0,0,1;0.785398rad)
  Radius = 4
FEATURE [Part::Compound] Compound167
  Links = -> [Cylinder162,Cylinder161]
FEATURE [Part::Cut] Cut070
  Base = -> Cut185
  Tool = -> Compound167
FEATURE [Part::Cut] Cut072
  Base = -> Cut070
  Tool = -> Compound169
FEATURE [Part::Box] Box055  label="Krychle055"
  AttacherType = Attacher::AttachEngine3D
  Height = 6
  Length = 6
  Placement = pos=(-54,-45,4) rot=(0,0,1;0rad)
  Width = 2
FEATURE [Part::Compound] Compound170
  Links = -> [Box054,Box053,Box052,Box055]
FEATURE [Part::Cut] Cut186
  Base = -> Cut071
  Tool = -> Compound170
FEATURE [Part::Box] Box056  label="Krychle056"
  AttacherType = Attacher::AttachEngine3D
  Height = 6
  Length = 6
  Placement = pos=(48,-45,4) rot=(0,0,1;0rad)
  Width = 2
FEATURE [Part::Cylinder] Cylinder516  label="Válec516"
  Angle = 360
  AttacherType = Attacher::AttachEngine3D
  Height = 20
  Placement = pos=(-56,-1.3e-14,2) rot=(0,0,-1;1.5708rad)
  Radius = 1.5
FEATURE [Part::Cylinder] Cylinder517  label="Válec517"
  Angle = 360
  AttacherType = Attacher::AttachEngine3D
  Height = 20
  Placement = pos=(39.598,-39.598,2) rot=(0,0,1;0.785398rad)
  Radius = 1.5
FEATURE [Part::Compound] Compound165
  Links = -> [Cylinder155,Cylinder517,Cylinder505,Cylinder156,Cylinder154,Cylinder511,Cylinder516,Cylinder503]
FEATURE [Part::Cut] Cut181
  Base = -> Cut205
  Tool = -> Compound165
FEATURE [Part::Box] Box062  label="Krychle062"
  AttacherType = Attacher::AttachEngine3D
  Height = 2
  Length = 6
  Placement = pos=(-41,-3,-4) rot=(0,0,1;1.5708rad)
  Width = 8
FEATURE [Part::Cylinder] Cylinder166  label="Válec166"
  Angle = 360
  AttacherType = Attacher::AttachEngine3D
  Height = 20
  Placement = pos=(24,-40,-5) rot=(1,0,0;1.5708rad)
  Radius = 1.5
FEATURE [Part::Cylinder] Cylinder167  label="Válec167"
  Angle = 360
  AttacherType = Attacher::AttachEngine3D
  Height = 20
  Placement = pos=(51,-40,7) rot=(1,0,0;1.5708rad)
  Radius = 1.5
FEATURE [Part::Box] Box061  label="Krychle061"
  AttacherType = Attacher::AttachEngine3D
  Height = 2
  Length = 6
  Placement = pos=(-31.1127,26.8701,-4) rot=(0,0,1;0.785398rad)
  Width = 8
FEATURE [Part::Box] Box067  label="Krychle067"
  AttacherType = Attacher::AttachEngine3D
  Height = 2
  Length = 6
  Placement = pos=(26.8701,31.1127,-4) rot=(0,0,-1;0.785398rad)
  Width = 8
FEATURE [Part::Cylinder] Cylinder175  label="Válec175"
  Angle = 360
  AttacherType = Attacher::AttachEngine3D
  Height = 20
  Placement = pos=(-45,-6e-15,-18) rot=(0,0,1;1.5708rad)
  Radius = 1.5
FEATURE [Part::Cylinder] Cylinder177  label="Válec177"
  Angle = 360
  AttacherType = Attacher::AttachEngine3D
  Height = 20
  Placement = pos=(1.4e-14,-45,-18) rot=(0,0,1;3.14159rad)
  Radius = 1.5
FEATURE [Part::Box] Box059  label="Krychle059"
  AttacherType = Attacher::AttachEngine3D
  Height = 6
  Length = 6
  Placement = pos=(-54,-45,4) rot=(0,0,1;0rad)
  Width = 2
FEATURE [Part::Compound] Compound171
  Links = -> [Box058,Box057,Box056,Box059]
FEATURE [Part::Cut] Cut182
  Base = -> Tube025
  Tool = -> Compound171
FEATURE [Part::Cut] Cut075
  Base = -> Cut182
  Tool = -> Compound172
FEATURE [Part::Cylinder] Cylinder170  label="Válec170"
  Angle = 360
  AttacherType = Attacher::AttachEngine3D
  Height = 20
  Placement = pos=(20,-40,-5) rot=(1,0,0;1.5708rad)
  Radius = 1.5
FEATURE [Part::Cylinder] Cylinder172  label="Válec172"
  Angle = 360
  AttacherType = Attacher::AttachEngine3D
  Height = 20
  Placement = pos=(-51,-40,7) rot=(1,0,0;1.5708rad)
  Radius = 1.5
FEATURE [Part::Cylinder] Cylinder169  label="Válec169"
  Angle = 360
  AttacherType = Attacher::AttachEngine3D
  Height = 20
  Placement = pos=(-20,-40,-5) rot=(1,0,0;1.5708rad)
  Radius = 1.5
FEATURE [Part::Cylinder] Cylinder168  label="Válec168"
  Angle = 360
  AttacherType = Attacher::AttachEngine3D
  Height = 20
  Placement = pos=(-51,-40,7) rot=(1,0,0;1.5708rad)
  Radius = 1.5
FEATURE [Part::Cylinder] Cylinder171  label="Válec171"
  Angle = 360
  AttacherType = Attacher::AttachEngine3D
  Height = 20
  Placement = pos=(51,-40,7) rot=(1,0,0;1.5708rad)
  Radius = 1.5
FEATURE [Part::Compound] Compound174
  Links = -> [Cylinder169,Cylinder170,Cylinder171,Cylinder172]
FEATURE [Part::Cut] Cut077
  Base = -> Cut186
  Tool = -> Compound174
FEATURE [Part::Box] Box060  label="Krychle060"
  AttacherType = Attacher::AttachEngine3D
  Height = 2
  Length = 6
  Placement = pos=(-3,41,-4) rot=(0,0,1;0rad)
  Width = 8
FEATURE [Part::Cylinder] Cylinder173  label="Válec173"
  Angle = 360
  AttacherType = Attacher::AttachEngine3D
  Height = 20
  Placement = pos=(0,45,-18) rot=(0,0,1;0rad)
  Radius = 1.5
FEATURE [Part::Cylinder] Cylinder165  label="Válec165"
  Angle = 360
  AttacherType = Attacher::AttachEngine3D
  Height = 20
  Placement = pos=(-24,-40,-5) rot=(1,0,0;1.5708rad)
  Radius = 1.5
FEATURE [Part::Compound] Compound173
  Links = -> [Cylinder165,Cylinder166,Cylinder167,Cylinder168]
FEATURE [Part::Cut] Cut076
  Base = -> Cut072
  Tool = -> Compound173
FEATURE [Part::Box] Box063  label="Krychle063"
  AttacherType = Attacher::AttachEngine3D
  Height = 2
  Length = 6
  Placement = pos=(-26.8701,-31.1127,-4) rot=(0,0,1;2.35619rad)
  Width = 8
FEATURE [Part::Box] Box064  label="Krychle064"
  AttacherType = Attacher::AttachEngine3D
  Height = 2
  Length = 6
  Placement = pos=(3,-41,-4) rot=(0,0,1;3.14159rad)
  Width = 8
FEATURE [Part::Box] Box065  label="Krychle065"
  AttacherType = Attacher::AttachEngine3D
  Height = 2
  Length = 6
  Placement = pos=(31.1127,-26.8701,-4) rot=(0,0,1;3.92699rad)
  Width = 8
FEATURE [Part::Box] Box066  label="Krychle066"
  AttacherType = Attacher::AttachEngine3D
  Height = 2
  Length = 6
  Placement = pos=(41,3,-4) rot=(0,0,-1;1.5708rad)
  Width = 8
FEATURE [Part::Compound] Compound175
  Links = -> [Box060,Box061,Box062,Box063,Box064,Box065,Box066,Box067]
  Placement = pos=(0,0,0) rot=(0,0,1;0.392699rad)
FEATURE [Part::Cut] Cut078
  Base = -> Cut075
  Tool = -> Compound175
FEATURE [Part::Cylinder] Cylinder174  label="Válec174"
  Angle = 360
  AttacherType = Attacher::AttachEngine3D
  Height = 20
  Placement = pos=(-31.8198,31.8198,-18) rot=(0,0,1;0.785398rad)
  Radius = 1.5
FEATURE [Part::Cylinder] Cylinder176  label="Válec176"
  Angle = 360
  AttacherType = Attacher::AttachEngine3D
  Height = 20
  Placement = pos=(-31.8198,-31.8198,-18) rot=(0,0,1;2.35619rad)
  Radius = 1.5
FEATURE [Part::Cylinder] Cylinder178  label="Válec178"
  Angle = 360
  AttacherType = Attacher::AttachEngine3D
  Height = 20
  Placement = pos=(31.8198,-31.8198,-18) rot=(0,0,1;3.92699rad)
  Radius = 1.5
FEATURE [Part::Cylinder] Cylinder179  label="Válec179"
  Angle = 360
  AttacherType = Attacher::AttachEngine3D
  Height = 20
  Placement = pos=(45,1.9e-14,-18) rot=(0,0,-1;1.5708rad)
  Radius = 1.5
FEATURE [Part::Cylinder] Cylinder180  label="Válec180"
  Angle = 360
  AttacherType = Attacher::AttachEngine3D
  Height = 20
  Placement = pos=(31.8198,31.8198,-18) rot=(0,0,-1;0.785398rad)
  Radius = 1.5
FEATURE [Part::Compound] Compound176
  Links = -> [Cylinder173,Cylinder174,Cylinder175,Cylinder176,Cylinder177,Cylinder178,Cylinder179,Cylinder180]
  Placement = pos=(0,0,0) rot=(0,0,1;0.392699rad)
FEATURE [Part::Cut] Cut079
  Base = -> Cut078
  Tool = -> Compound176
FEATURE [Part::Compound] Compound177  label="joint_max_monoblok1"
  Links = -> [Cut077,Cut079,Cut076,Cut069,Cut181]
FEATURE [Part::Fillet] Fillet004
  Base = -> Compound177
  Edges = 2 edges r=9: [Edge42,Edge278]
FEATURE [Part::Fillet] Fillet001  label="J-max_monoblok2"
  Base = -> Fillet004
  Edges = 2 edges r=8: [Edge30,Edge90]
FEATURE [Part::Box] Box108  label="Krychle108"
  AttacherType = Attacher::AttachEngine3D
  Height = 10
  Length = 10
  Placement = pos=(50,-43,10) rot=(0,0,1;0rad)
  Width = 43
FEATURE [Part::Cylinder] Cylinder518  label="Válec518"
  Angle = 360
  AttacherType = Attacher::AttachEngine3D
  Height = 20
  Placement = pos=(-39.598,-39.598,2) rot=(0,0,-1;0.785398rad)
  Radius = 1.5
FEATURE [Part::Cylinder] Cylinder519  label="Válec519"
  Angle = 360
  AttacherType = Attacher::AttachEngine3D
  Height = 20
  Placement = pos=(0,-56,2) rot=(0,0,1;0rad)
  Radius = 1.5
FEATURE [Part::Cylinder] Cylinder520  label="Válec520"
  Angle = 360
  AttacherType = Attacher::AttachEngine3D
  Height = 20
  Placement = pos=(-39.598,39.598,2) rot=(0,0,1;3.92699rad)
  Radius = 1.5
FEATURE [Part::Cylinder] Cylinder521  label="Válec521"
  Angle = 360
  AttacherType = Attacher::AttachEngine3D
  Height = 20
  Placement = pos=(56,0,2) rot=(0,0,1;1.5708rad)
  Radius = 1.5
FEATURE [Part::Cylinder] Cylinder522  label="Válec522"
  Angle = 360
  AttacherType = Attacher::AttachEngine3D
  Height = 10
  Placement = pos=(60,-43,10) rot=(0,0,1;0rad)
  Radius = 6
FEATURE [Part::Box] Box109  label="Krychle109"
  AttacherType = Attacher::AttachEngine3D
  Height = 10
  Length = 10
  Placement = pos=(-60,-43,10) rot=(0,0,1;0rad)
  Width = 43
FEATURE [Part::Compound] Compound239
  Links = -> [Box109,Box108]
FEATURE [Part::Cylinder] Cylinder523  label="Válec523"
  Angle = 360
  AttacherType = Attacher::AttachEngine3D
  Height = 20
  Placement = pos=(39.598,39.598,2) rot=(0,0,1;2.35619rad)
  Radius = 1.5
FEATURE [Part::Cylinder] Cylinder524  label="Válec524"
  Angle = 360
  AttacherType = Attacher::AttachEngine3D
  Height = 20
  Placement = pos=(39.598,-39.598,2) rot=(0,0,1;0.785398rad)
  Radius = 1.5
FEATURE [Part::Cylinder] Cylinder525  label="Válec525"
  Angle = 360
  AttacherType = Attacher::AttachEngine3D
  Height = 20
  Placement = pos=(-56,-1.3e-14,2) rot=(0,0,-1;1.5708rad)
  Radius = 1.5
FEATURE [Part::Cylinder] Cylinder526  label="Válec526"
  Angle = 360
  AttacherType = Attacher::AttachEngine3D
  Height = 10
  Placement = pos=(-60,-43,10) rot=(0,0,1;0rad)
  Radius = 6
FEATURE [Part::Compound] Compound241
  Links = -> [Cylinder522,Cylinder526]
FEATURE [Part::Cylinder] Cylinder527  label="Válec527"
  Angle = 360
  AttacherType = Attacher::AttachEngine3D
  Height = 20
  Placement = pos=(-1.2e-14,56,2) rot=(0,0,1;3.14159rad)
  Radius = 1.5
FEATURE [Part::Compound] Compound240
  Links = -> [Cylinder519,Cylinder524,Cylinder521,Cylinder523,Cylinder527,Cylinder520,Cylinder525,Cylinder518]
FEATURE [Part::Cut] Cut206
  Base = -> Compound239
  Tool = -> Compound240
FEATURE [Part::Cut] Cut207
  Base = -> Cut206
  Tool = -> Compound241
FEATURE [Part::Fillet] Fillet002
  Base = -> Cut207
  Edges = 2 edges r=4: [Edge4,Edge43]
FEATURE [Part::Compound] Compound242  label="J-max_monoblok"
  Links = -> [Fillet002,Fillet001]
  Placement = pos=(0,13,-53) rot=(0,0.707107,-0.707107;3.14159rad)
FEATURE [Part::Cylinder] Cylinder  label="Válec"
  Angle = 360
  AttacherType = Attacher::AttachEngine3D
  Height = 52
  Placement = pos=(0,13,-53) rot=(1,0,0;1.5708rad)
  Radius = 60.2
FEATURE [Part::Cut] Cut208
  Base = -> Cut203
  Tool = -> Cylinder
FEATURE [Part::Box] Box240  label="Krychle240"
  AttacherType = Attacher::AttachEngine3D
  Height = 64
  Length = 6
  Placement = pos=(11,-3,-93) rot=(0,0,1;0rad)
  Width = 6
FEATURE [Part::Box] Box241  label="Krychle241"
  AttacherType = Attacher::AttachEngine3D
  Height = 64
  Length = 6
  Placement = pos=(87,-3,-93) rot=(0,0,1;0rad)
  Width = 6
FEATURE [Part::Compound] Compound653
  Links = -> [Box240,Box241]
  Placement = pos=(-52,0,36) rot=(0,0,1;0rad)
FEATURE [Part::Cut] Cut209
  Base = -> Cut208
  Tool = -> Compound653
FEATURE [Part::Compound] Compound654  label="bazovina_part-A_triangle-support"
  Links = -> [Cut209,Cut190,Cut198,Cut200,Cut204]
FEATURE [Mesh::Feature] Mesh  label="bazovina_part-A_triangle-support (Meshed)"
FEATURE [Sketcher::SketchObject] Sketch002
  FullyConstrained = false
  MapMode = 5
  Support = -> [XY_Plane002]
  sketch-geometry (5):
    g0: LineSegment StartX=-53.11 StartY=25.5869 StartZ=0 EndX=-9.47198 EndY=128.297 EndZ=0
    g1: LineSegment StartX=-9.47198 StartY=128.297 StartZ=0 EndX=9.50803 EndY=128.154 EndZ=0
    g2: LineSegment StartX=9.50803 StartY=128.154 StartZ=0 EndX=53.1093 EndY=25.7412 EndZ=0
    g3: LineSegment StartX=53.1093 StartY=25.7412 StartZ=0 EndX=-0.067027 EndY=50.049 EndZ=0
    g4: LineSegment StartX=-0.067027 StartY=50.049 StartZ=0 EndX=-53.11 EndY=25.5869 EndZ=0
  constraints (5):
    c: Coincident(g0,g1)
    c: Coincident(g1,g2)
    c: Coincident(g2,g3)
    c: Coincident(g3,g4)
    c: Coincident(g4,g0)
FEATURE [PartDesign::Pad] Pad002
  Direction = (1,1,1)
  Length = 10
  Length2 = 100
  Profile = -> Sketch002
  Type = 0
FEATURE [PartDesign::Body] Body002
  Group = -> [Sketch002,Pad002]
  Origin = -> Origin002
  Tip = -> Pad002
FEATURE [Part::Cylinder] Cylinder1268  label="Válec1268"
  Angle = 360
  AttacherType = Attacher::AttachEngine3D
  Height = 10
  Placement = pos=(0,106,0) rot=(0,0,1;0rad)
  Radius = 10
FEATURE [Part::Box] Box242  label="Krychle242"
  AttacherType = Attacher::AttachEngine3D
  Height = 32
  Length = 200
  Placement = pos=(-100,-130,0) rot=(0,0,1;0rad)
  Width = 100
FEATURE [Part::Box] Box243  label="Krychle243"
  AttacherType = Attacher::AttachEngine3D
  Height = 10
  Length = 10
  Placement = pos=(32,-24,0) rot=(0,0,1;0rad)
  Width = 52
FEATURE [Part::Cylinder] Cylinder1269  label="Válec1269"
  Angle = 360
  AttacherType = Attacher::AttachEngine3D
  Height = 100
  Placement = pos=(51,-12,0) rot=(0,0,1;0rad)
  Radius = 1.5
FEATURE [Part::Box] Box244  label="Krychle244"
  AttacherType = Attacher::AttachEngine3D
  Height = 10
  Length = 10
  Placement = pos=(-42,-24,0) rot=(0,0,1;0rad)
  Width = 52
FEATURE [Part::Compound] Compound663
  Links = -> [Box243,Box244]
FEATURE [Part::Box] Box245  label="Krychle245"
  AttacherType = Attacher::AttachEngine3D
  Height = 10
  Length = 72
  Placement = pos=(-36,-30,0) rot=(0,0,1;0rad)
  Width = 70
FEATURE [Part::Cylinder] Cylinder1270  label="Válec1270"
  Angle = 360
  AttacherType = Attacher::AttachEngine3D
  Height = 100
  Placement = pos=(-51,-12,0) rot=(0,0,1;0rad)
  Radius = 1.5
FEATURE [Part::Compound] Compound655
  Links = -> [Cylinder1270,Cylinder1269]
FEATURE [Part::Cylinder] Cylinder1271  label="Válec1271"
  Angle = 360
  AttacherType = Attacher::AttachEngine3D
  Height = 50
  Placement = pos=(-51,6,0) rot=(0,0,1;0rad)
  Radius = 1.5
FEATURE [Part::Cylinder] Cylinder1272  label="Válec1272"
  Angle = 360
  AttacherType = Attacher::AttachEngine3D
  Height = 50
  Placement = pos=(51,6,0) rot=(0,0,1;0rad)
  Radius = 1.5
FEATURE [Part::FeaturePython] Tube026  # WARN: FeaturePython — macro-defined, semantics opaque (R4)
  AttacherType = Attacher::AttachEngine3D
  Height = 10
  InnerRadius = 40
  OuterRadius = 59
FEATURE [Part::Cut] Cut213
  Base = -> Tube026
  Tool = -> Box242
FEATURE [Part::Cylinder] Cylinder1273  label="Válec1273"
  Angle = 360
  AttacherType = Attacher::AttachEngine3D
  Height = 50
  Placement = pos=(-24,18,0) rot=(0,0,1;0rad)
  Radius = 1.5
FEATURE [Part::Cylinder] Cylinder1274  label="Válec1274"
  Angle = 360
  AttacherType = Attacher::AttachEngine3D
  Height = 50
  Placement = pos=(24,18,0) rot=(0,0,1;0rad)
  Radius = 1.5
FEATURE [Part::Compound] Compound656
  Links = -> [Cylinder1272,Cylinder1271,Cylinder1273,Cylinder1274]
  Placement = pos=(0,6,0) rot=(0,0,1;0rad)
FEATURE [Part::Cylinder] Cylinder1275  label="Válec1275"
  Angle = 360
  AttacherType = Attacher::AttachEngine3D
  Height = 4
  Placement = pos=(-7,-34,73) rot=(1,0,0;1.5708rad)
  Radius = 3
FEATURE [Part::Cylinder] Cylinder1276  label="Válec1276"
  Angle = 360
  AttacherType = Attacher::AttachEngine3D
  Height = 20
  Placement = pos=(7,-34,37) rot=(1,0,0;1.5708rad)
  Radius = 1.5
FEATURE [Part::Cylinder] Cylinder1277  label="Válec1277"
  Angle = 360
  AttacherType = Attacher::AttachEngine3D
  Height = 20
  Placement = pos=(7,-34,73) rot=(1,0,0;1.5708rad)
  Radius = 1.5
FEATURE [Part::Cylinder] Cylinder1278  label="Válec1278"
  Angle = 360
  AttacherType = Attacher::AttachEngine3D
  Height = 20
  Placement = pos=(-7,-34,37) rot=(1,0,0;1.5708rad)
  Radius = 1.5
FEATURE [Part::Cylinder] Cylinder1279  label="Válec1279"
  Angle = 360
  AttacherType = Attacher::AttachEngine3D
  Height = 20
  Placement = pos=(-7,-34,73) rot=(1,0,0;1.5708rad)
  Radius = 1.5
FEATURE [Part::Compound] Compound658
  Links = -> [Cylinder1276,Cylinder1278,Cylinder1277,Cylinder1279]
  Placement = pos=(0,141,45) rot=(1,0,0;1.5708rad)
FEATURE [Part::Cut] Cut211
  Base = -> Cylinder1268
  Tool = -> Compound658
FEATURE [Part::Cylinder] Cylinder1280  label="Válec1280"
  Angle = 360
  AttacherType = Attacher::AttachEngine3D
  Height = 4
  Placement = pos=(-7,-34,37) rot=(1,0,0;1.5708rad)
  Radius = 3
FEATURE [Part::Cylinder] Cylinder1281  label="Válec1281"
  Angle = 360
  AttacherType = Attacher::AttachEngine3D
  Height = 4
  Placement = pos=(7,-34,73) rot=(1,0,0;1.5708rad)
  Radius = 3
FEATURE [Part::Cylinder] Cylinder1282  label="Válec1282"
  Angle = 360
  AttacherType = Attacher::AttachEngine3D
  Height = 4
  Placement = pos=(7,-34,37) rot=(1,0,0;1.5708rad)
  Radius = 3
FEATURE [Part::Compound] Compound657
  Links = -> [Cylinder1282,Cylinder1280,Cylinder1281,Cylinder1275]
  Placement = pos=(0,141,45) rot=(1,0,0;1.5708rad)
FEATURE [Part::Cut] Cut212
  Base = -> Cut211
  Placement = pos=(0,19,0) rot=(0,0,1;0rad)
  Tool = -> Compound657
FEATURE [Part::Cylinder] Cylinder1283  label="Válec1283"
  Angle = 360
  AttacherType = Attacher::AttachEngine3D
  Height = 4
  Placement = pos=(7,-34,37) rot=(1,0,0;1.5708rad)
  Radius = 3
FEATURE [Part::Cylinder] Cylinder1284  label="Válec1284"
  Angle = 360
  AttacherType = Attacher::AttachEngine3D
  Height = 20
  Placement = pos=(-7,-34,37) rot=(1,0,0;1.5708rad)
  Radius = 1.5
FEATURE [Part::Cylinder] Cylinder1285  label="Válec1285"
  Angle = 360
  AttacherType = Attacher::AttachEngine3D
  Height = 20
  Placement = pos=(7,-34,37) rot=(1,0,0;1.5708rad)
  Radius = 1.5
FEATURE [Part::Cylinder] Cylinder1286  label="Válec1286"
  Angle = 360
  AttacherType = Attacher::AttachEngine3D
  Height = 20
  Placement = pos=(7,-34,73) rot=(1,0,0;1.5708rad)
  Radius = 1.5
FEATURE [Part::Cylinder] Cylinder1287  label="Válec1287"
  Angle = 360
  AttacherType = Attacher::AttachEngine3D
  Height = 20
  Placement = pos=(-7,-34,73) rot=(1,0,0;1.5708rad)
  Radius = 1.5
FEATURE [Part::Compound] Compound659
  Links = -> [Cylinder1285,Cylinder1284,Cylinder1286,Cylinder1287]
  Placement = pos=(0,160,45) rot=(1,0,0;1.5708rad)
FEATURE [Part::Cut] Cut214
  Base = -> Body002
  Tool = -> Compound659
FEATURE [Part::Cylinder] Cylinder1288  label="Válec1288"
  Angle = 360
  AttacherType = Attacher::AttachEngine3D
  Height = 4
  Placement = pos=(-7,-34,73) rot=(1,0,0;1.5708rad)
  Radius = 3
FEATURE [Part::Cylinder] Cylinder1289  label="Válec1289"
  Angle = 360
  AttacherType = Attacher::AttachEngine3D
  Height = 4
  Placement = pos=(-7,-34,37) rot=(1,0,0;1.5708rad)
  Radius = 3
FEATURE [Part::Cylinder] Cylinder1290  label="Válec1290"
  Angle = 360
  AttacherType = Attacher::AttachEngine3D
  Height = 4
  Placement = pos=(7,-34,73) rot=(1,0,0;1.5708rad)
  Radius = 3
FEATURE [Part::Compound] Compound660
  Links = -> [Cylinder1283,Cylinder1289,Cylinder1290,Cylinder1288]
  Placement = pos=(0,160,45) rot=(1,0,0;1.5708rad)
FEATURE [Part::Cylinder] Cylinder1291  label="Válec1291"
  Angle = 360
  AttacherType = Attacher::AttachEngine3D
  Height = 100
  Placement = pos=(39,-21,0) rot=(0,0,1;0rad)
  Radius = 1.5
FEATURE [Part::Cylinder] Cylinder1292  label="Válec1292"
  Angle = 360
  AttacherType = Attacher::AttachEngine3D
  Height = 100
  Placement = pos=(-39,-21,0) rot=(0,0,1;0rad)
  Radius = 1.5
FEATURE [Part::Compound] Compound661
  Links = -> [Cylinder1292,Cylinder1291]
  Placement = pos=(0,-6,0) rot=(0,0,1;0rad)
FEATURE [Part::Cylinder] Cylinder1293  label="Válec1293"
  Angle = 360
  AttacherType = Attacher::AttachEngine3D
  Height = 100
  Placement = pos=(-39,-21,0) rot=(0,0,1;0rad)
  Radius = 1.5
FEATURE [Part::Cylinder] Cylinder1294  label="Válec1294"
  Angle = 360
  AttacherType = Attacher::AttachEngine3D
  Height = 100
  Placement = pos=(39,-21,0) rot=(0,0,1;0rad)
  Radius = 1.5
FEATURE [Part::Compound] Compound662
  Links = -> [Cylinder1293,Cylinder1294]
  Placement = pos=(0,-6,0) rot=(0,0,1;0rad)
FEATURE [Part::Cut] Cut210
  Base = -> Compound663
  Tool = -> Compound662
FEATURE [Part::Box] Box246  label="Krychle246"
  AttacherType = Attacher::AttachEngine3D
  Height = 64
  Length = 6
  Placement = pos=(11,-3,-93) rot=(0,0,1;0rad)
  Width = 6
FEATURE [Part::Box] Box247  label="Krychle247"
  AttacherType = Attacher::AttachEngine3D
  Height = 64
  Length = 6
  Placement = pos=(87,-3,-93) rot=(0,0,1;0rad)
  Width = 6
FEATURE [Part::Compound] Compound664
  Links = -> [Box246,Box247]
  Placement = pos=(-52,0,36) rot=(0,0,1;0rad)
FEATURE [Part::Cylinder] Cylinder1295  label="Válec1295"
  Angle = 360
  AttacherType = Attacher::AttachEngine3D
  Height = 100
  Placement = pos=(90,0,-60) rot=(0,0,1;0rad)
  Radius = 1.5
FEATURE [Part::Cylinder] Cylinder1296  label="Válec1296"
  Angle = 360
  AttacherType = Attacher::AttachEngine3D
  Height = 100
  Placement = pos=(14,0,-60) rot=(0,0,1;0rad)
  Radius = 1.5
FEATURE [Part::Compound] Compound665  label="srouby_troj005"
  Links = -> [Cylinder1295,Cylinder1296]
  Placement = pos=(-52,0,0) rot=(0,0,1;0rad)
FEATURE [Part::Cylinder] Cylinder1297  label="Válec1297"
  Angle = 360
  AttacherType = Attacher::AttachEngine3D
  Height = 32
  Placement = pos=(26,41,-42) rot=(0,0,1;0rad)
  Radius = 1.5
FEATURE [Part::Cylinder] Cylinder1298  label="Válec1298"
  Angle = 360
  AttacherType = Attacher::AttachEngine3D
  Height = 32
  Placement = pos=(78,41,-42) rot=(0,0,1;0rad)
  Radius = 1.5
FEATURE [Part::Compound] Compound666
  Links = -> [Cylinder1297,Cylinder1298]
  Placement = pos=(-52,0,36) rot=(0,0,1;0rad)
FEATURE [Part::Cylinder] Cylinder1299  label="Válec1299"
  Angle = 360
  AttacherType = Attacher::AttachEngine3D
  Height = 3
  Placement = pos=(26,41,-42) rot=(0,0,1;0rad)
  Radius = 3
FEATURE [Part::Cylinder] Cylinder1300  label="Válec1300"
  Angle = 360
  AttacherType = Attacher::AttachEngine3D
  Height = 3
  Placement = pos=(78,41,-42) rot=(0,0,1;0rad)
  Radius = 3
FEATURE [Part::Cylinder] Cylinder1301  label="Válec1301"
  Angle = 360
  AttacherType = Attacher::AttachEngine3D
  Height = 3
  Placement = pos=(26,41,-42) rot=(0,0,1;0rad)
  Radius = 3
FEATURE [Part::Cylinder] Cylinder1302  label="Válec1302"
  Angle = 360
  AttacherType = Attacher::AttachEngine3D
  Height = 3
  Placement = pos=(78,41,-42) rot=(0,0,1;0rad)
  Radius = 3
FEATURE [Part::Compound] Compound667
  Links = -> [Compound661,Compound656,Compound655]
  Placement = pos=(0,0,-10) rot=(0,0,1;0rad)
FEATURE [Part::Compound] Compound668
  Links = -> [Compound665,Compound666]
FEATURE [Part::Compound] Compound669
  Links = -> [Cylinder1299,Cylinder1300]
  Placement = pos=(-52,0,42) rot=(0,0,1;0rad)
FEATURE [Part::Compound] Compound670
  Links = -> [Cylinder1301,Cylinder1302]
  Placement = pos=(-52,0,42) rot=(0,0,1;0rad)
FEATURE [Part::Cut] Cut215
  Base = -> Cut214
  Tool = -> Compound660
FEATURE [Part::Cut] Cut223
  Base = -> Box245
  Tool = -> Compound667
FEATURE [Part::Cut] Cut224
  Base = -> Cut223
  Tool = -> Compound670
FEATURE [Part::Cylinder] Cylinder1303  label="Válec1303"
  Angle = 360
  AttacherType = Attacher::AttachEngine3D
  Height = 100
  Placement = pos=(51,-12,0) rot=(0,0,1;0rad)
  Radius = 1.5
FEATURE [Part::Cylinder] Cylinder1304  label="Válec1304"
  Angle = 360
  AttacherType = Attacher::AttachEngine3D
  Height = 100
  Placement = pos=(-51,-12,0) rot=(0,0,1;0rad)
  Radius = 1.5
FEATURE [Part::Compound] Compound672
  Links = -> [Cylinder1304,Cylinder1303]
FEATURE [Part::Cylinder] Cylinder1305  label="Válec1305"
  Angle = 360
  AttacherType = Attacher::AttachEngine3D
  Height = 50
  Placement = pos=(-51,6,0) rot=(0,0,1;0rad)
  Radius = 1.5
FEATURE [Part::Cylinder] Cylinder1306  label="Válec1306"
  Angle = 360
  AttacherType = Attacher::AttachEngine3D
  Height = 50
  Placement = pos=(51,6,0) rot=(0,0,1;0rad)
  Radius = 1.5
FEATURE [Part::Cylinder] Cylinder1307  label="Válec1307"
  Angle = 360
  AttacherType = Attacher::AttachEngine3D
  Height = 50
  Placement = pos=(-24,18,0) rot=(0,0,1;0rad)
  Radius = 1.5
FEATURE [Part::Cylinder] Cylinder1308  label="Válec1308"
  Angle = 360
  AttacherType = Attacher::AttachEngine3D
  Height = 50
  Placement = pos=(24,18,0) rot=(0,0,1;0rad)
  Radius = 1.5
FEATURE [Part::Compound] Compound673
  Links = -> [Cylinder1306,Cylinder1305,Cylinder1307,Cylinder1308]
  Placement = pos=(0,6,0) rot=(0,0,1;0rad)
FEATURE [Part::Cylinder] Cylinder1309  label="Válec1309"
  Angle = 360
  AttacherType = Attacher::AttachEngine3D
  Height = 100
  Placement = pos=(39,-21,0) rot=(0,0,1;0rad)
  Radius = 1.5
FEATURE [Part::Cylinder] Cylinder1310  label="Válec1310"
  Angle = 360
  AttacherType = Attacher::AttachEngine3D
  Height = 100
  Placement = pos=(-39,-21,0) rot=(0,0,1;0rad)
  Radius = 1.5
FEATURE [Part::Compound] Compound674
  Links = -> [Cylinder1310,Cylinder1309]
  Placement = pos=(0,-6,0) rot=(0,0,1;0rad)
FEATURE [Part::Compound] Compound671
  Links = -> [Compound674,Compound673,Compound672]
  Placement = pos=(0,0,-10) rot=(0,0,1;0rad)
FEATURE [Part::Cut] Cut216
  Base = -> Cut213
  Tool = -> Compound671
FEATURE [Part::Cylinder] Cylinder1311  label="Válec1311"
  Angle = 360
  AttacherType = Attacher::AttachEngine3D
  Height = 100
  Placement = pos=(90,0,-60) rot=(0,0,1;0rad)
  Radius = 1.5
FEATURE [Part::Cylinder] Cylinder1312  label="Válec1312"
  Angle = 360
  AttacherType = Attacher::AttachEngine3D
  Height = 100
  Placement = pos=(14,0,-60) rot=(0,0,1;0rad)
  Radius = 1.5
FEATURE [Part::Compound] Compound676  label="srouby_troj006"
  Links = -> [Cylinder1311,Cylinder1312]
  Placement = pos=(-52,0,0) rot=(0,0,1;0rad)
FEATURE [Part::Cylinder] Cylinder1313  label="Válec1313"
  Angle = 360
  AttacherType = Attacher::AttachEngine3D
  Height = 32
  Placement = pos=(26,41,-42) rot=(0,0,1;0rad)
  Radius = 1.5
FEATURE [Part::Cylinder] Cylinder1314  label="Válec1314"
  Angle = 360
  AttacherType = Attacher::AttachEngine3D
  Height = 32
  Placement = pos=(78,41,-42) rot=(0,0,1;0rad)
  Radius = 1.5
FEATURE [Part::Compound] Compound677
  Links = -> [Cylinder1313,Cylinder1314]
  Placement = pos=(-52,0,36) rot=(0,0,1;0rad)
FEATURE [Part::Compound] Compound675
  Links = -> [Compound676,Compound677]
FEATURE [Part::Cut] Cut217
  Base = -> Cut216
  Tool = -> Compound675
FEATURE [Part::Cut] Cut218
  Base = -> Cut217
  Tool = -> Compound669
FEATURE [Part::Cut] Cut220
  Base = -> Cut218
  Tool = -> Compound664
FEATURE [Part::Cylinder] Cylinder1315  label="Válec1315"
  Angle = 360
  AttacherType = Attacher::AttachEngine3D
  Height = 3
  Placement = pos=(26,41,-42) rot=(0,0,1;0rad)
  Radius = 3
FEATURE [Part::Cylinder] Cylinder1316  label="Válec1316"
  Angle = 360
  AttacherType = Attacher::AttachEngine3D
  Height = 3
  Placement = pos=(78,41,-42) rot=(0,0,1;0rad)
  Radius = 3
FEATURE [Part::Compound] Compound678
  Links = -> [Cylinder1315,Cylinder1316]
  Placement = pos=(-52,0,42) rot=(0,0,1;0rad)
FEATURE [Part::Cut] Cut219
  Base = -> Cut215
  Tool = -> Compound678
FEATURE [Part::Cylinder] Cylinder1317  label="Válec1317"
  Angle = 360
  AttacherType = Attacher::AttachEngine3D
  Height = 100
  Placement = pos=(90,0,-60) rot=(0,0,1;0rad)
  Radius = 1.5
FEATURE [Part::Cylinder] Cylinder1318  label="Válec1318"
  Angle = 360
  AttacherType = Attacher::AttachEngine3D
  Height = 100
  Placement = pos=(14,0,-60) rot=(0,0,1;0rad)
  Radius = 1.5
FEATURE [Part::Compound] Compound680  label="srouby_troj007"
  Links = -> [Cylinder1317,Cylinder1318]
  Placement = pos=(-52,0,0) rot=(0,0,1;0rad)
FEATURE [Part::Cylinder] Cylinder1319  label="Válec1319"
  Angle = 360
  AttacherType = Attacher::AttachEngine3D
  Height = 32
  Placement = pos=(26,41,-42) rot=(0,0,1;0rad)
  Radius = 1.5
FEATURE [Part::Cylinder] Cylinder1320  label="Válec1320"
  Angle = 360
  AttacherType = Attacher::AttachEngine3D
  Height = 32
  Placement = pos=(78,41,-42) rot=(0,0,1;0rad)
  Radius = 1.5
FEATURE [Part::Compound] Compound681
  Links = -> [Cylinder1319,Cylinder1320]
  Placement = pos=(-52,0,36) rot=(0,0,1;0rad)
FEATURE [Part::Compound] Compound679
  Links = -> [Compound680,Compound681]
FEATURE [Part::Cut] Cut221
  Base = -> Cut210
  Tool = -> Compound679
FEATURE [Part::Box] Box248  label="Krychle248"
  AttacherType = Attacher::AttachEngine3D
  Height = 64
  Length = 6
  Placement = pos=(11,-3,-93) rot=(0,0,1;0rad)
  Width = 6
FEATURE [Part::Box] Box249  label="Krychle249"
  AttacherType = Attacher::AttachEngine3D
  Height = 64
  Length = 6
  Placement = pos=(87,-3,-93) rot=(0,0,1;0rad)
  Width = 6
FEATURE [Part::Compound] Compound682
  Links = -> [Box248,Box249]
  Placement = pos=(-52,0,36) rot=(0,0,1;0rad)
FEATURE [Part::Cut] Cut222
  Base = -> Cut221
  Tool = -> Compound682
FEATURE [Part::Cylinder] Cylinder1321  label="Válec1321"
  Angle = 360
  AttacherType = Attacher::AttachEngine3D
  Height = 100
  Placement = pos=(90,0,-60) rot=(0,0,1;0rad)
  Radius = 1.5
FEATURE [Part::Cylinder] Cylinder1322  label="Válec1322"
  Angle = 360
  AttacherType = Attacher::AttachEngine3D
  Height = 100
  Placement = pos=(14,0,-60) rot=(0,0,1;0rad)
  Radius = 1.5
FEATURE [Part::Compound] Compound684  label="srouby_troj008"
  Links = -> [Cylinder1321,Cylinder1322]
  Placement = pos=(-52,0,0) rot=(0,0,1;0rad)
FEATURE [Part::Cylinder] Cylinder1323  label="Válec1323"
  Angle = 360
  AttacherType = Attacher::AttachEngine3D
  Height = 32
  Placement = pos=(26,41,-42) rot=(0,0,1;0rad)
  Radius = 1.5
FEATURE [Part::Cylinder] Cylinder1324  label="Válec1324"
  Angle = 360
  AttacherType = Attacher::AttachEngine3D
  Height = 32
  Placement = pos=(78,41,-42) rot=(0,0,1;0rad)
  Radius = 1.5
FEATURE [Part::Compound] Compound685
  Links = -> [Cylinder1323,Cylinder1324]
  Placement = pos=(-52,0,36) rot=(0,0,1;0rad)
FEATURE [Part::Compound] Compound683
  Links = -> [Compound684,Compound685]
FEATURE [Part::Cut] Cut225
  Base = -> Cut224
  Tool = -> Compound668
FEATURE [Part::Cut] Cut226
  Base = -> Cut219
  Tool = -> Compound683
FEATURE [Part::Cylinder] Cylinder1325  label="Válec1325"
  Angle = 360
  AttacherType = Attacher::AttachEngine3D
  Height = 58
  Placement = pos=(0,19,-53) rot=(1,0,0;1.5708rad)
  Radius = 60.2
FEATURE [Part::Cut] Cut227
  Base = -> Cut225
  Tool = -> Cylinder1325
FEATURE [Part::Box] Box250  label="Krychle250"
  AttacherType = Attacher::AttachEngine3D
  Height = 64
  Length = 6
  Placement = pos=(11,-3,-93) rot=(0,0,1;0rad)
  Width = 6
FEATURE [Part::Box] Box251  label="Krychle251"
  AttacherType = Attacher::AttachEngine3D
  Height = 64
  Length = 6
  Placement = pos=(87,-3,-93) rot=(0,0,1;0rad)
  Width = 6
FEATURE [Part::Compound] Compound686
  Links = -> [Box250,Box251]
  Placement = pos=(-52,0,36) rot=(0,0,1;0rad)
FEATURE [Part::Cut] Cut228
  Base = -> Cut227
  Tool = -> Compound686
FEATURE [Part::Torus] Torus004  label="Anuloid004"
  Angle1 = -180
  Angle2 = 180
  Angle3 = 360
  AttacherType = Attacher::AttachEngine3D
  Placement = pos=(0,0,34) rot=(0,0,1;0rad)
  Radius1 = 51.9
  Radius2 = 3.1
FEATURE [Part::Box] Box489  label="Krychle489"
  AttacherType = Attacher::AttachEngine3D
  Height = 6
  Length = 6
  Placement = pos=(-54,-45,4) rot=(0,0,1;0rad)
  Width = 2
FEATURE [Part::Cylinder] Cylinder1337  label="Válec1337"
  Angle = 360
  AttacherType = Attacher::AttachEngine3D
  Height = 20
  Placement = pos=(-39.6,-39.6,-10) rot=(0,0,-1;0.785398rad)
  Radius = 4
FEATURE [Part::Cylinder] Cylinder1338  label="Válec1338"
  Angle = 360
  AttacherType = Attacher::AttachEngine3D
  Height = 40
  Placement = pos=(59,-17,0) rot=(0,0,1;0rad)
  Radius = 10
FEATURE [Part::Box] Box490  label="Krychle490"
  AttacherType = Attacher::AttachEngine3D
  Height = 6
  Length = 6
  Placement = pos=(48,-45,4) rot=(0,0,1;0rad)
  Width = 2
FEATURE [Part::Cylinder] Cylinder1339  label="Válec1339"
  Angle = 360
  AttacherType = Attacher::AttachEngine3D
  Height = 20
  Placement = pos=(51,-40,7) rot=(1,0,0;1.5708rad)
  Radius = 1.5
FEATURE [Part::Cylinder] Cylinder1340  label="Válec1340"
  Angle = 360
  AttacherType = Attacher::AttachEngine3D
  Height = 20
  Placement = pos=(-24,-40,-5) rot=(1,0,0;1.5708rad)
  Radius = 1.5
FEATURE [Part::Cylinder] Cylinder1341  label="Válec1341"
  Angle = 360
  AttacherType = Attacher::AttachEngine3D
  Height = 8
  Placement = pos=(0,0,20) rot=(0,0,1;0rad)
  Radius = 52
FEATURE [Part::Box] Box491  label="Krychle491"
  AttacherType = Attacher::AttachEngine3D
  Height = 6
  Length = 6
  Placement = pos=(-27,-47,-8) rot=(0,0,1;0rad)
  Width = 2
FEATURE [Part::Cylinder] Cylinder1342  label="Válec1342"
  Angle = 360
  AttacherType = Attacher::AttachEngine3D
  Height = 40
  Placement = pos=(-59,-17,0) rot=(0,0,1;0rad)
  Radius = 10
FEATURE [Part::Box] Box492  label="Krychle492"
  AttacherType = Attacher::AttachEngine3D
  Height = 8
  Length = 108
  Placement = pos=(-54,-53,20) rot=(0,0,1;0rad)
  Width = 36
FEATURE [Part::Cut] Cut481
  Base = -> Box492
  Placement = pos=(0,0,-20) rot=(0,0,1;0rad)
  Tool = -> Cylinder1341
FEATURE [Part::Box] Box493  label="Krychle493"
  AttacherType = Attacher::AttachEngine3D
  Height = 6
  Length = 6
  Placement = pos=(21,-47,-8) rot=(0,0,1;0rad)
  Width = 2
FEATURE [Part::Compound] Compound864
  Links = -> [Box491,Box493,Box490,Box489]
FEATURE [Part::Cylinder] Cylinder1343  label="Válec1343"
  Angle = 360
  AttacherType = Attacher::AttachEngine3D
  Height = 20
  Placement = pos=(24,-40,-5) rot=(1,0,0;1.5708rad)
  Radius = 1.5
FEATURE [Part::Cylinder] Cylinder1344  label="Válec1344"
  Angle = 360
  AttacherType = Attacher::AttachEngine3D
  Height = 20
  Placement = pos=(39.6,-39.6,-10) rot=(0,0,1;0.785398rad)
  Radius = 4
FEATURE [Part::Cylinder] Cylinder1345  label="Válec1345"
  Angle = 360
  AttacherType = Attacher::AttachEngine3D
  Height = 20
  Placement = pos=(-51,-40,7) rot=(1,0,0;1.5708rad)
  Radius = 1.5
FEATURE [Part::Compound] Compound863
  Links = -> [Cylinder1340,Cylinder1343,Cylinder1339,Cylinder1345]
FEATURE [Part::Cylinder] Cylinder1346  label="Válec1346"
  Angle = 360
  AttacherType = Attacher::AttachEngine3D
  Height = 50
  Placement = pos=(0,-56,2) rot=(0,0,1;0rad)
  Radius = 1.5
FEATURE [Part::Cylinder] Cylinder1347  label="Válec1347"
  Angle = 360
  AttacherType = Attacher::AttachEngine3D
  Height = 50
  Placement = pos=(-39.598,39.598,2) rot=(0,0,1;3.92699rad)
  Radius = 1.5
FEATURE [Part::Box] Box494  label="Krychle494"
  AttacherType = Attacher::AttachEngine3D
  Height = 12
  Length = 10
  Placement = pos=(50,-43,10) rot=(0,0,1;0rad)
  Width = 43
FEATURE [Part::FeaturePython] Tube091  # WARN: FeaturePython — macro-defined, semantics opaque (R4)
  AttacherType = Attacher::AttachEngine3D
  Height = 8
  InnerRadius = 42
  OuterRadius = 52
  Placement = pos=(0,0,-8) rot=(0,0,1;0rad)
FEATURE [Part::Cylinder] Cylinder1348  label="Válec1348"
  Angle = 360
  AttacherType = Attacher::AttachEngine3D
  Height = 16
  Placement = pos=(-60,-43,10) rot=(0,0,1;0rad)
  Radius = 6
FEATURE [Part::Cylinder] Cylinder1349  label="Válec1349"
  Angle = 360
  AttacherType = Attacher::AttachEngine3D
  Height = 50
  Placement = pos=(39.598,39.598,2) rot=(0,0,1;2.35619rad)
  Radius = 1.5
FEATURE [Part::Cylinder] Cylinder1350  label="Válec1350"
  Angle = 360
  AttacherType = Attacher::AttachEngine3D
  Height = 50
  Placement = pos=(-39.598,-39.598,2) rot=(0,0,-1;0.785398rad)
  Radius = 1.5
FEATURE [Part::Cylinder] Cylinder1351  label="Válec1351"
  Angle = 360
  AttacherType = Attacher::AttachEngine3D
  Height = 50
  Placement = pos=(56,0,2) rot=(0,0,1;1.5708rad)
  Radius = 1.5
FEATURE [Part::Box] Box495  label="Krychle495"
  AttacherType = Attacher::AttachEngine3D
  Height = 12
  Length = 10
  Placement = pos=(-60,-43,10) rot=(0,0,1;0rad)
  Width = 43
FEATURE [Part::Cylinder] Cylinder1352  label="Válec1352"
  Angle = 360
  AttacherType = Attacher::AttachEngine3D
  Height = 16
  Placement = pos=(60,-43,10) rot=(0,0,1;0rad)
  Radius = 6
FEATURE [Part::Cylinder] Cylinder1353  label="Válec1353"
  Angle = 360
  AttacherType = Attacher::AttachEngine3D
  Height = 50
  Placement = pos=(-1.2e-14,56,2) rot=(0,0,1;3.14159rad)
  Radius = 1.5
FEATURE [Part::Cylinder] Cylinder1354  label="Válec1354"
  Angle = 360
  AttacherType = Attacher::AttachEngine3D
  Height = 50
  Placement = pos=(-56,-1.3e-14,2) rot=(0,0,-1;1.5708rad)
  Radius = 1.5
FEATURE [Part::Cylinder] Cylinder1355  label="Válec1355"
  Angle = 360
  AttacherType = Attacher::AttachEngine3D
  Height = 50
  Placement = pos=(39.598,-39.598,2) rot=(0,0,1;0.785398rad)
  Radius = 1.5
FEATURE [Part::Cylinder] Cylinder1364  label="Válec1364"
  Angle = 360
  AttacherType = Attacher::AttachEngine3D
  Height = 50
  Placement = pos=(-39.598,39.598,2) rot=(0,0,1;3.92699rad)
  Radius = 1.5
FEATURE [Part::Cylinder] Cylinder1365  label="Válec1365"
  Angle = 360
  AttacherType = Attacher::AttachEngine3D
  Height = 50
  Placement = pos=(-56,-1.3e-14,2) rot=(0,0,-1;1.5708rad)
  Radius = 1.5
FEATURE [Part::Cylinder] Cylinder1366  label="Válec1366"
  Angle = 360
  AttacherType = Attacher::AttachEngine3D
  Height = 50
  Placement = pos=(39.598,39.598,2) rot=(0,0,1;2.35619rad)
  Radius = 1.5
FEATURE [Part::Cylinder] Cylinder1367  label="Válec1367"
  Angle = 360
  AttacherType = Attacher::AttachEngine3D
  Height = 50
  Placement = pos=(-39.598,-39.598,2) rot=(0,0,-1;0.785398rad)
  Radius = 1.5
FEATURE [Part::Cylinder] Cylinder1368  label="Válec1368"
  Angle = 360
  AttacherType = Attacher::AttachEngine3D
  Height = 16
  Placement = pos=(0,0,20) rot=(0,0,1;0rad)
  Radius = 52
FEATURE [Part::Cylinder] Cylinder1369  label="Válec1369"
  Angle = 360
  AttacherType = Attacher::AttachEngine3D
  Height = 50
  Placement = pos=(0,-56,2) rot=(0,0,1;0rad)
  Radius = 1.5
FEATURE [Part::Cylinder] Cylinder1370  label="Válec1370"
  Angle = 360
  AttacherType = Attacher::AttachEngine3D
  Height = 50
  Placement = pos=(-1.2e-14,56,2) rot=(0,0,1;3.14159rad)
  Radius = 1.5
FEATURE [Part::Compound] Compound865
  Links = -> [Cylinder1338,Cylinder1342]
FEATURE [Part::Cut] Cut484
  Base = -> Cut481
  Placement = pos=(0,0,-8) rot=(0,0,1;0rad)
  Tool = -> Compound865
FEATURE [Part::Compound] Compound866
  Links = -> [Cylinder1337,Cylinder1344]
FEATURE [Part::Cut] Cut482
  Base = -> Cut484
  Tool = -> Compound866
FEATURE [Part::Cut] Cut483
  Base = -> Cut482
  Tool = -> Compound864
FEATURE [Part::Cut] Cut480
  Base = -> Cut483
  Tool = -> Compound863
FEATURE [Part::Compound] Compound867
  Links = -> [Box495,Box494]
FEATURE [Part::Compound] Compound868
  Links = -> [Cylinder1346,Cylinder1355,Cylinder1351,Cylinder1349,Cylinder1353,Cylinder1347,Cylinder1354,Cylinder1350]
FEATURE [Part::Cut] Cut485
  Base = -> Compound867
  Tool = -> Compound868
FEATURE [Part::Compound] Compound869
  Links = -> [Cylinder1352,Cylinder1348]
FEATURE [Part::Cut] Cut486
  Base = -> Cut485
  Tool = -> Compound869
FEATURE [Part::Fillet] Fillet020
  Base = -> Cut480
  Edges = 2 edges r=12: [Edge2,Edge38]
  Placement = pos=(0,0,-6) rot=(0,0,1;0rad)
FEATURE [Part::Fillet] Fillet021
  Base = -> Cut486
  Edges = 2 edges r=8: [Edge4,Edge43]
  Placement = pos=(0,0,-4) rot=(0,0,1;0rad)
FEATURE [Part::Cylinder] Cylinder1371  label="Válec1371"
  Angle = 360
  AttacherType = Attacher::AttachEngine3D
  Height = 50
  Placement = pos=(39.598,-39.598,2) rot=(0,0,1;0.785398rad)
  Radius = 1.5
FEATURE [Part::Compound] Compound871
  Links = -> [Cylinder1369,Cylinder1371,Cylinder1366,Cylinder1370,Cylinder1364,Cylinder1365,Cylinder1367]
FEATURE [Part::Box] Box497  label="Krychle497"
  AttacherType = Attacher::AttachEngine3D
  Height = 12
  Length = 108
  Placement = pos=(-54,-53,20) rot=(0,0,1;0rad)
  Width = 36
FEATURE [Part::Cut] Cut490
  Base = -> Box497
  Placement = pos=(0,0,-10) rot=(0,0,1;0rad)
  Tool = -> Cylinder1368
FEATURE [Part::Cut] Cut489
  Base = -> Cut490
  Placement = pos=(0,0,-4) rot=(0,0,1;0rad)
  Tool = -> Compound871
FEATURE [Part::Cylinder] Cylinder1372  label="Válec1372"
  Angle = 360
  AttacherType = Attacher::AttachEngine3D
  Height = 20
  Placement = pos=(51,-40,7) rot=(1,0,0;1.5708rad)
  Radius = 1.5
FEATURE [Part::Cylinder] Cylinder1373  label="Válec1373"
  Angle = 360
  AttacherType = Attacher::AttachEngine3D
  Height = 20
  Placement = pos=(0,45,-18) rot=(0,0,1;0rad)
  Radius = 1.5
FEATURE [Part::Cylinder] Cylinder1374  label="Válec1374"
  Angle = 360
  AttacherType = Attacher::AttachEngine3D
  Height = 20
  Placement = pos=(-24,-40,-5) rot=(1,0,0;1.5708rad)
  Radius = 1.5
FEATURE [Part::Box] Box498  label="Krychle498"
  AttacherType = Attacher::AttachEngine3D
  Height = 2
  Length = 6
  Placement = pos=(3,-41,-4) rot=(0,0,1;3.14159rad)
  Width = 8
FEATURE [Part::Cylinder] Cylinder1375  label="Válec1375"
  Angle = 360
  AttacherType = Attacher::AttachEngine3D
  Height = 20
  Placement = pos=(-51,-40,7) rot=(1,0,0;1.5708rad)
  Radius = 1.5
FEATURE [Part::Box] Box499  label="Krychle499"
  AttacherType = Attacher::AttachEngine3D
  Height = 6
  Length = 6
  Placement = pos=(48,-45,4) rot=(0,0,1;0rad)
  Width = 2
FEATURE [Part::Box] Box500  label="Krychle500"
  AttacherType = Attacher::AttachEngine3D
  Height = 2
  Length = 6
  Placement = pos=(-41,-3,-4) rot=(0,0,1;1.5708rad)
  Width = 8
FEATURE [Part::Cylinder] Cylinder1376  label="Válec1376"
  Angle = 360
  AttacherType = Attacher::AttachEngine3D
  Height = 20
  Placement = pos=(24,-40,-5) rot=(1,0,0;1.5708rad)
  Radius = 1.5
FEATURE [Part::Compound] Compound875
  Links = -> [Cylinder1374,Cylinder1376,Cylinder1372,Cylinder1375]
FEATURE [Part::Cylinder] Cylinder1377  label="Válec1377"
  Angle = 360
  AttacherType = Attacher::AttachEngine3D
  Height = 20
  Placement = pos=(1.4e-14,-45,-18) rot=(0,0,1;3.14159rad)
  Radius = 1.5
FEATURE [Part::Box] Box501  label="Krychle501"
  AttacherType = Attacher::AttachEngine3D
  Height = 2
  Length = 6
  Placement = pos=(41,3,-4) rot=(0,0,-1;1.5708rad)
  Width = 8
FEATURE [Part::Cylinder] Cylinder1378  label="Válec1378"
  Angle = 360
  AttacherType = Attacher::AttachEngine3D
  Height = 20
  Placement = pos=(-45,-6e-15,-18) rot=(0,0,1;1.5708rad)
  Radius = 1.5
FEATURE [Part::Cylinder] Cylinder1379  label="Válec1379"
  Angle = 360
  AttacherType = Attacher::AttachEngine3D
  Height = 20
  Placement = pos=(-31.8198,-31.8198,-18) rot=(0,0,1;2.35619rad)
  Radius = 1.5
FEATURE [Part::Cylinder] Cylinder1380  label="Válec1380"
  Angle = 360
  AttacherType = Attacher::AttachEngine3D
  Height = 20
  Placement = pos=(45,1.9e-14,-18) rot=(0,0,-1;1.5708rad)
  Radius = 1.5
FEATURE [Part::Box] Box502  label="Krychle502"
  AttacherType = Attacher::AttachEngine3D
  Height = 2
  Length = 6
  Placement = pos=(-3,41,-4) rot=(0,0,1;0rad)
  Width = 8
FEATURE [Part::FeaturePython] wormgear062  # WARN: FeaturePython — macro-defined, semantics opaque (R4)
  AttacherType = Attacher::AttachEngine3D
  Placement = pos=(0,0,0) rot=(0,0,1;0.083427rad)
  beta = 40.5833
  clearance = 0.25
  diameter = 78.8
  head = 0
  height = 20
  module = 1.5
  pressure_angle = 20
  reverse_pitch = false
  teeth = 45
  version = 0.0.3
FEATURE [Part::Box] Box503  label="Krychle503"
  AttacherType = Attacher::AttachEngine3D
  Height = 2
  Length = 6
  Placement = pos=(-31.1127,26.8701,-4) rot=(0,0,1;0.785398rad)
  Width = 8
FEATURE [Part::Box] Box504  label="Krychle504"
  AttacherType = Attacher::AttachEngine3D
  Height = 6
  Length = 6
  Placement = pos=(-27,-47,-8) rot=(0,0,1;0rad)
  Width = 2
FEATURE [Part::Box] Box505  label="Krychle505"
  AttacherType = Attacher::AttachEngine3D
  Height = 2
  Length = 6
  Placement = pos=(31.1127,-26.8701,-4) rot=(0,0,1;3.92699rad)
  Width = 8
FEATURE [Part::Cylinder] Cylinder1381  label="Válec1381"
  Angle = 360
  AttacherType = Attacher::AttachEngine3D
  Height = 20
  Placement = pos=(31.8198,31.8198,-18) rot=(0,0,-1;0.785398rad)
  Radius = 1.5
FEATURE [Part::Box] Box506  label="Krychle506"
  AttacherType = Attacher::AttachEngine3D
  Height = 6
  Length = 6
  Placement = pos=(-54,-45,4) rot=(0,0,1;0rad)
  Width = 2
FEATURE [Part::Cylinder] Cylinder1382  label="Válec1382"
  Angle = 360
  AttacherType = Attacher::AttachEngine3D
  Height = 20
  Placement = pos=(-31.8198,31.8198,-18) rot=(0,0,1;0.785398rad)
  Radius = 1.5
FEATURE [Part::Box] Box507  label="Krychle507"
  AttacherType = Attacher::AttachEngine3D
  Height = 6
  Length = 6
  Placement = pos=(21,-47,-8) rot=(0,0,1;0rad)
  Width = 2
FEATURE [Part::Compound] Compound874
  Links = -> [Box504,Box507,Box499,Box506]
FEATURE [Part::Cut] Cut494
  Base = -> Tube091
  Tool = -> Compound874
FEATURE [Part::Cut] Cut492
  Base = -> Cut494
  Tool = -> Compound875
FEATURE [Part::Cylinder] Cylinder1383  label="Válec1383"
  Angle = 360
  AttacherType = Attacher::AttachEngine3D
  Height = 20
  Placement = pos=(31.8198,-31.8198,-18) rot=(0,0,1;3.92699rad)
  Radius = 1.5
FEATURE [Part::Compound] Compound872
  Links = -> [Cylinder1373,Cylinder1382,Cylinder1378,Cylinder1379,Cylinder1377,Cylinder1383,Cylinder1380,Cylinder1381]
  Placement = pos=(0,0,0) rot=(0,0,1;0.392699rad)
FEATURE [Part::Box] Box508  label="Krychle508"
  AttacherType = Attacher::AttachEngine3D
  Height = 2
  Length = 6
  Placement = pos=(26.8701,31.1127,-4) rot=(0,0,-1;0.785398rad)
  Width = 8
FEATURE [Part::Box] Box509  label="Krychle509"
  AttacherType = Attacher::AttachEngine3D
  Height = 2
  Length = 6
  Placement = pos=(-26.8701,-31.1127,-4) rot=(0,0,1;2.35619rad)
  Width = 8
FEATURE [Part::Compound] Compound873
  Links = -> [Box502,Box503,Box500,Box509,Box498,Box505,Box501,Box508]
  Placement = pos=(0,0,0) rot=(0,0,1;0.392699rad)
FEATURE [Part::Cut] Cut493
  Base = -> Cut492
  Tool = -> Compound873
FEATURE [Part::Cut] Cut491
  Base = -> Cut493
  Placement = pos=(0,0,-6) rot=(0,0,1;0rad)
  Tool = -> Compound872
FEATURE [Part::Cylinder] Cylinder1384  label="Válec1384"
  Angle = 360
  AttacherType = Attacher::AttachEngine3D
  Height = 40
  Placement = pos=(-59,-17,0) rot=(0,0,1;0rad)
  Radius = 10
FEATURE [Part::Cylinder] Cylinder1385  label="Válec1385"
  Angle = 360
  AttacherType = Attacher::AttachEngine3D
  Height = 20
  Placement = pos=(-51,-40,7) rot=(1,0,0;1.5708rad)
  Radius = 1.5
FEATURE [Part::Box] Box510  label="Krychle510"
  AttacherType = Attacher::AttachEngine3D
  Height = 12
  Length = 108
  Placement = pos=(-54,-53,20) rot=(0,0,1;0rad)
  Width = 36
FEATURE [Part::Cylinder] Cylinder1386  label="Válec1386"
  Angle = 360
  AttacherType = Attacher::AttachEngine3D
  Height = 20
  Placement = pos=(0,0,20) rot=(0,0,1;0rad)
  Radius = 52
FEATURE [Part::Cut] Cut498
  Base = -> Box510
  Placement = pos=(0,0,-20) rot=(0,0,1;0rad)
  Tool = -> Cylinder1386
FEATURE [Part::Cylinder] Cylinder1387  label="Válec1387"
  Angle = 360
  AttacherType = Attacher::AttachEngine3D
  Height = 20
  Placement = pos=(-39.6,-39.6,-10) rot=(0,0,-1;0.785398rad)
  Radius = 4
FEATURE [Part::Box] Box511  label="Krychle511"
  AttacherType = Attacher::AttachEngine3D
  Height = 6
  Length = 6
  Placement = pos=(48,-45,4) rot=(0,0,1;0rad)
  Width = 2
FEATURE [Part::FeaturePython] wormgear063  # WARN: FeaturePython — macro-defined, semantics opaque (R4)
  AttacherType = Attacher::AttachEngine3D
  Placement = pos=(0,0,0) rot=(0,0,1;0.124791rad)
  beta = 40.5833
  clearance = 0.25
  diameter = 78.8
  head = 0
  height = 20
  module = 1.5
  pressure_angle = 20
  reverse_pitch = true
  teeth = 45
  version = 0.0.3
FEATURE [Part::Cylinder] Cylinder1388  label="Válec1388"
  Angle = 360
  AttacherType = Attacher::AttachEngine3D
  Height = 40
  Placement = pos=(59,-17,0) rot=(0,0,1;0rad)
  Radius = 10
FEATURE [Part::Compound] Compound878
  Links = -> [Cylinder1388,Cylinder1384]
FEATURE [Part::Cut] Cut499
  Base = -> Cut498
  Tool = -> Compound878
FEATURE [Part::Cylinder] Cylinder1389  label="Válec1389"
  Angle = 360
  AttacherType = Attacher::AttachEngine3D
  Height = 20
  Placement = pos=(-20,-40,-5) rot=(1,0,0;1.5708rad)
  Radius = 1.5
FEATURE [Part::Cylinder] Cylinder1390  label="Válec1390"
  Angle = 360
  AttacherType = Attacher::AttachEngine3D
  Height = 20
  Placement = pos=(51,-40,7) rot=(1,0,0;1.5708rad)
  Radius = 1.5
FEATURE [Part::Cylinder] Cylinder1391  label="Válec1391"
  Angle = 360
  AttacherType = Attacher::AttachEngine3D
  Height = 20
  Placement = pos=(20,-40,-5) rot=(1,0,0;1.5708rad)
  Radius = 1.5
FEATURE [Part::Compound] Compound879
  Links = -> [Cylinder1389,Cylinder1391,Cylinder1390,Cylinder1385]
FEATURE [Part::Box] Box512  label="Krychle512"
  AttacherType = Attacher::AttachEngine3D
  Height = 6
  Length = 6
  Placement = pos=(-23,-47,-8) rot=(0,0,1;0rad)
  Width = 2
FEATURE [Part::Box] Box513  label="Krychle513"
  AttacherType = Attacher::AttachEngine3D
  Height = 6
  Length = 6
  Placement = pos=(-54,-45,4) rot=(0,0,1;0rad)
  Width = 2
FEATURE [Part::Cylinder] Cylinder1392  label="Válec1392"
  Angle = 360
  AttacherType = Attacher::AttachEngine3D
  Height = 20
  Placement = pos=(39.6,-39.6,-10) rot=(0,0,1;0.785398rad)
  Radius = 4
FEATURE [Part::Compound] Compound876
  Links = -> [Cylinder1387,Cylinder1392]
FEATURE [Part::Cut] Cut496
  Base = -> Cut499
  Tool = -> Compound876
FEATURE [Part::Box] Box514  label="Krychle514"
  AttacherType = Attacher::AttachEngine3D
  Height = 6
  Length = 6
  Placement = pos=(17,-47,-8) rot=(0,0,1;0rad)
  Width = 2
FEATURE [Part::Compound] Compound877
  Links = -> [Box512,Box514,Box511,Box513]
FEATURE [Part::Cut] Cut497
  Base = -> Cut496
  Tool = -> Compound877
FEATURE [Part::Cut] Cut495
  Base = -> Cut497
  Tool = -> Compound879
FEATURE [Part::Fillet] Fillet022
  Base = -> Cut495
  Edges = 2 edges r=12: [Edge3,Edge36]
  Placement = pos=(0,0,-6) rot=(0,0,1;0rad)
FEATURE [Part::Cylinder] Cylinder1393  label="Válec1393"
  Angle = 360
  AttacherType = Attacher::AttachEngine3D
  Height = 50
  Placement = pos=(31.8198,31.8198,-18) rot=(0,0,-1;0.785398rad)
  Radius = 1.5
FEATURE [Part::Cylinder] Cylinder1394  label="Válec1394"
  Angle = 360
  AttacherType = Attacher::AttachEngine3D
  Height = 50
  Placement = pos=(39.598,-39.598,2) rot=(0,0,1;0.785398rad)
  Radius = 1.5
FEATURE [Part::Cylinder] Cylinder1395  label="Válec1395"
  Angle = 360
  AttacherType = Attacher::AttachEngine3D
  Height = 50
  Placement = pos=(0,45,-18) rot=(0,0,1;0rad)
  Radius = 1.5
FEATURE [Part::Cylinder] Cylinder1396  label="Válec1396"
  Angle = 360
  AttacherType = Attacher::AttachEngine3D
  Height = 50
  Placement = pos=(1.4e-14,-45,-18) rot=(0,0,1;3.14159rad)
  Radius = 1.5
FEATURE [Part::Cylinder] Cylinder1397  label="Válec1397"
  Angle = 360
  AttacherType = Attacher::AttachEngine3D
  Height = 50
  Placement = pos=(31.8198,-31.8198,-18) rot=(0,0,1;3.92699rad)
  Radius = 1.5
FEATURE [Part::Cylinder] Cylinder1398  label="Válec1398"
  Angle = 360
  AttacherType = Attacher::AttachEngine3D
  Height = 20
  Placement = pos=(39.6,-39.6,-10) rot=(0,0,1;0.785398rad)
  Radius = 4
FEATURE [Part::Cylinder] Cylinder1399  label="Válec1399"
  Angle = 360
  AttacherType = Attacher::AttachEngine3D
  Height = 50
  Placement = pos=(-31.8198,31.8198,-18) rot=(0,0,1;0.785398rad)
  Radius = 1.5
FEATURE [Part::Cylinder] Cylinder1400  label="Válec1400"
  Angle = 360
  AttacherType = Attacher::AttachEngine3D
  Height = 50
  Placement = pos=(-56,-1.3e-14,2) rot=(0,0,-1;1.5708rad)
  Radius = 1.5
FEATURE [Part::Cylinder] Cylinder1401  label="Válec1401"
  Angle = 360
  AttacherType = Attacher::AttachEngine3D
  Height = 50
  Placement = pos=(45,1.9e-14,-18) rot=(0,0,-1;1.5708rad)
  Radius = 1.5
FEATURE [Part::Cylinder] Cylinder1402  label="Válec1402"
  Angle = 360
  AttacherType = Attacher::AttachEngine3D
  Height = 50
  Placement = pos=(-39.598,39.598,2) rot=(0,0,1;3.92699rad)
  Radius = 1.5
FEATURE [Part::Cylinder] Cylinder1403  label="Válec1403"
  Angle = 360
  AttacherType = Attacher::AttachEngine3D
  Height = 50
  Placement = pos=(-31.8198,-31.8198,-18) rot=(0,0,1;2.35619rad)
  Radius = 1.5
FEATURE [Part::Cylinder] Cylinder1404  label="Válec1404"
  Angle = 360
  AttacherType = Attacher::AttachEngine3D
  Height = 50
  Placement = pos=(-45,-6e-15,-18) rot=(0,0,1;1.5708rad)
  Radius = 1.5
FEATURE [Part::Compound] Compound883
  Links = -> [Cylinder1395,Cylinder1399,Cylinder1404,Cylinder1403,Cylinder1396,Cylinder1397,Cylinder1401,Cylinder1393]
  Placement = pos=(0,0,-20) rot=(0,0,1;0.392699rad)
FEATURE [Part::Cylinder] Cylinder1405  label="Válec1405"
  Angle = 360
  AttacherType = Attacher::AttachEngine3D
  Height = 50
  Placement = pos=(-39.598,-39.598,2) rot=(0,0,-1;0.785398rad)
  Radius = 1.5
FEATURE [Part::Cylinder] Cylinder1406  label="Válec1406"
  Angle = 360
  AttacherType = Attacher::AttachEngine3D
  Height = 12
  Radius = 52
FEATURE [Part::Cut] Cut500
  Base = -> Cylinder1406
  Tool = -> wormgear062
FEATURE [Part::Cylinder] Cylinder1407  label="Válec1407"
  Angle = 360
  AttacherType = Attacher::AttachEngine3D
  Height = 50
  Placement = pos=(0,-56,2) rot=(0,0,1;0rad)
  Radius = 1.5
FEATURE [Part::Cylinder] Cylinder1408  label="Válec1408"
  Angle = 360
  AttacherType = Attacher::AttachEngine3D
  Height = 50
  Placement = pos=(-1.2e-14,56,2) rot=(0,0,1;3.14159rad)
  Radius = 1.5
FEATURE [Part::Cylinder] Cylinder1409  label="Válec1409"
  Angle = 360
  AttacherType = Attacher::AttachEngine3D
  Height = 50
  Placement = pos=(39.598,39.598,2) rot=(0,0,1;2.35619rad)
  Radius = 1.5
FEATURE [Part::Cylinder] Cylinder1410  label="Válec1410"
  Angle = 360
  AttacherType = Attacher::AttachEngine3D
  Height = 12
  Radius = 60
FEATURE [Part::Cut] Cut503
  Base = -> Cylinder1410
  Placement = pos=(0,0,12) rot=(0,0,1;0.034907rad)
  Tool = -> wormgear063
FEATURE [Part::Compound] Compound882
  Links = -> [Cut503,Cut500]
FEATURE [Part::Cylinder] Cylinder1411  label="Válec1411"
  Angle = 360
  AttacherType = Attacher::AttachEngine3D
  Height = 50
  Placement = pos=(56,0,2) rot=(0,0,1;1.5708rad)
  Radius = 1.5
FEATURE [Part::Compound] Compound881
  Links = -> [Cylinder1407,Cylinder1394,Cylinder1411,Cylinder1409,Cylinder1408,Cylinder1402,Cylinder1400,Cylinder1405]
FEATURE [Part::Cut] Cut501
  Base = -> Compound882
  Tool = -> Compound881
FEATURE [Part::Cylinder] Cylinder1412  label="Válec1412"
  Angle = 360
  AttacherType = Attacher::AttachEngine3D
  Height = 20
  Placement = pos=(-39.6,-39.6,-10) rot=(0,0,-1;0.785398rad)
  Radius = 4
FEATURE [Part::Compound] Compound880
  Links = -> [Cylinder1412,Cylinder1398]
FEATURE [Part::Cylinder] Cylinder1413  label="Válec1413"
  Angle = 360
  AttacherType = Attacher::AttachEngine3D
  Height = 40
  Placement = pos=(0,-17,13) rot=(1,0,0;1.5708rad)
  Radius = 59
FEATURE [Part::Box] Box464  label="Krychle464"
  AttacherType = Attacher::AttachEngine3D
  Height = 19
  Length = 10
  Placement = pos=(-60,-43,10) rot=(0,0,1;0rad)
  Width = 43
FEATURE [Part::Box] Box465  label="Krychle465"
  AttacherType = Attacher::AttachEngine3D
  Height = 19
  Length = 10
  Placement = pos=(50,-43,10) rot=(0,0,1;0rad)
  Width = 43
FEATURE [Part::Cylinder] Cylinder1414  label="Válec1414"
  Angle = 360
  AttacherType = Attacher::AttachEngine3D
  Height = 33
  Placement = pos=(60,-43,10) rot=(0,0,1;0rad)
  Radius = 6
FEATURE [Part::Cut] Cut504
  Base = -> Cut501
  Tool = -> Compound880
FEATURE [Part::Cut] Cut502
  Base = -> Cut504
  Placement = pos=(0,0,-6) rot=(0,0,1;0rad)
  Tool = -> Compound883
FEATURE [Part::Common] Common004
  Base = -> Fillet020
  Tool = -> Cylinder1413
FEATURE [Part::Compound] Compound884  label="J-max-deep_monoblok"
  Links = -> [Fillet021,Cut489,Cut491,Fillet022,Cut502,Common004]
  Placement = pos=(0,13,-53) rot=(0,0.707107,-0.707107;3.14159rad)
FEATURE [Part::Box] Box466  label="Krychle466"
  AttacherType = Attacher::AttachEngine3D
  Height = 2
  Length = 6
  Placement = pos=(45.9619,41.7193,23) rot=(0,0,1;2.35619rad)
  Width = 10
FEATURE [Part::Box] Box467  label="Krychle467"
  AttacherType = Attacher::AttachEngine3D
  Height = 2
  Length = 6
  Placement = pos=(62,-3,23) rot=(0,0,1;1.5708rad)
  Width = 10
FEATURE [Part::Box] Box468  label="Krychle468"
  AttacherType = Attacher::AttachEngine3D
  Height = 2
  Length = 6
  Placement = pos=(41.7193,-45.9619,23) rot=(0,0,1;0.785398rad)
  Width = 10
FEATURE [Part::Box] Box469  label="Krychle469"
  AttacherType = Attacher::AttachEngine3D
  Height = 2
  Length = 6
  Placement = pos=(-3,-62,23) rot=(0,0,1;0rad)
  Width = 10
FEATURE [Part::Box] Box470  label="Krychle470"
  AttacherType = Attacher::AttachEngine3D
  Height = 2
  Length = 6
  Placement = pos=(-45.9619,-41.7193,23) rot=(0,0,-1;0.785398rad)
  Width = 10
FEATURE [Part::Box] Box471  label="Krychle471"
  AttacherType = Attacher::AttachEngine3D
  Height = 2
  Length = 6
  Placement = pos=(-62,3,23) rot=(0,0,-1;1.5708rad)
  Width = 10
FEATURE [Part::Cylinder] Cylinder1415  label="Válec1415"
  Angle = 360
  AttacherType = Attacher::AttachEngine3D
  Height = 50
  Placement = pos=(39.598,39.598,2) rot=(0,0,1;2.35619rad)
  Radius = 1.5
FEATURE [Part::Cylinder] Cylinder1416  label="Válec1416"
  Angle = 360
  AttacherType = Attacher::AttachEngine3D
  Height = 33
  Placement = pos=(-60,-43,10) rot=(0,0,1;0rad)
  Radius = 6
FEATURE [Part::Cylinder] Cylinder1417  label="Válec1417"
  Angle = 360
  AttacherType = Attacher::AttachEngine3D
  Height = 50
  Placement = pos=(-39.598,39.598,2) rot=(0,0,1;3.92699rad)
  Radius = 1.5
FEATURE [Part::Cylinder] Cylinder1418  label="Válec1418"
  Angle = 360
  AttacherType = Attacher::AttachEngine3D
  Height = 50
  Placement = pos=(56,0,2) rot=(0,0,1;1.5708rad)
  Radius = 1.5
FEATURE [Part::Cylinder] Cylinder1419  label="Válec1419"
  Angle = 360
  AttacherType = Attacher::AttachEngine3D
  Height = 50
  Placement = pos=(-1.2e-14,56,2) rot=(0,0,1;3.14159rad)
  Radius = 1.5
FEATURE [Part::Cylinder] Cylinder1420  label="Válec1420"
  Angle = 360
  AttacherType = Attacher::AttachEngine3D
  Height = 50
  Placement = pos=(-56,-1.3e-14,2) rot=(0,0,-1;1.5708rad)
  Radius = 1.5
FEATURE [Part::Cylinder] Cylinder1421  label="Válec1421"
  Angle = 360
  AttacherType = Attacher::AttachEngine3D
  Height = 50
  Placement = pos=(0,-56,2) rot=(0,0,1;0rad)
  Radius = 1.5
FEATURE [Part::Cylinder] Cylinder1422  label="Válec1422"
  Angle = 360
  AttacherType = Attacher::AttachEngine3D
  Height = 50
  Placement = pos=(39.598,-39.598,2) rot=(0,0,1;0.785398rad)
  Radius = 1.5
FEATURE [Part::Cylinder] Cylinder1423  label="Válec1423"
  Angle = 360
  AttacherType = Attacher::AttachEngine3D
  Height = 50
  Placement = pos=(-39.598,-39.598,2) rot=(0,0,-1;0.785398rad)
  Radius = 1.5
FEATURE [Part::Cylinder] Cylinder1424  label="Válec1424"
  Angle = 360
  AttacherType = Attacher::AttachEngine3D
  Height = 33
  Placement = pos=(0,0,20) rot=(0,0,1;0rad)
  Radius = 60
FEATURE [Part::Cylinder] Cylinder1425  label="Válec1425"
  Angle = 360
  AttacherType = Attacher::AttachEngine3D
  Height = 40
  Placement = pos=(-51,-40,25) rot=(1,0,0;1.5708rad)
  Radius = 1.5
FEATURE [Part::Cylinder] Cylinder1426  label="Válec1426"
  Angle = 360
  AttacherType = Attacher::AttachEngine3D
  Height = 40
  Placement = pos=(51,-40,25) rot=(1,0,0;1.5708rad)
  Radius = 1.5
FEATURE [Part::Box] Box472  label="Krychle472"
  AttacherType = Attacher::AttachEngine3D
  Height = 2
  Length = 6
  Placement = pos=(3,62,23) rot=(0,0,1;3.14159rad)
  Width = 10
FEATURE [Part::Box] Box473  label="Krychle473"
  AttacherType = Attacher::AttachEngine3D
  Height = 2
  Length = 6
  Placement = pos=(-41.7193,45.9619,23) rot=(0,0,1;3.92699rad)
  Width = 10
FEATURE [Part::Box] Box474  label="Krychle474"
  AttacherType = Attacher::AttachEngine3D
  Height = 6
  Length = 6
  Placement = pos=(48,-45,35) rot=(0,0,1;0rad)
  Width = 2
FEATURE [Part::Box] Box475  label="Krychle475"
  AttacherType = Attacher::AttachEngine3D
  Height = 6
  Length = 6
  Placement = pos=(-54,-45,35) rot=(0,0,1;0rad)
  Width = 2
FEATURE [Part::Cylinder] Cylinder1427  label="Válec1427"
  Angle = 360
  AttacherType = Attacher::AttachEngine3D
  Height = 40
  Placement = pos=(-51,-40,38) rot=(1,0,0;1.5708rad)
  Radius = 1.5
FEATURE [Part::Cylinder] Cylinder1428  label="Válec1428"
  Angle = 360
  AttacherType = Attacher::AttachEngine3D
  Height = 40
  Placement = pos=(51,-40,38) rot=(1,0,0;1.5708rad)
  Radius = 1.5
FEATURE [Part::Compound] Compound851
  Links = -> [Cylinder1427,Cylinder1428]
  Placement = pos=(0,8,-11) rot=(0,0,1;0rad)
FEATURE [Part::Cylinder] Cylinder1429  label="Válec1429"
  Angle = 360
  AttacherType = Attacher::AttachEngine3D
  Height = 10
  Placement = pos=(-40,0,36) rot=(0,0,1;0rad)
  Radius = 3.5
FEATURE [Part::Cylinder] Cylinder1430  label="Válec1430"
  Angle = 360
  AttacherType = Attacher::AttachEngine3D
  Height = 20
  Placement = pos=(39.598,-39.598,2) rot=(0,0,1;0.785398rad)
  Radius = 1.5
FEATURE [Part::Cylinder] Cylinder1431  label="Válec1431"
  Angle = 360
  AttacherType = Attacher::AttachEngine3D
  Height = 50
  Placement = pos=(-51.5,0,34) rot=(0,0,1;0rad)
  Radius = 3.5
FEATURE [Part::Cylinder] Cylinder1432  label="Válec1432"
  Angle = 360
  AttacherType = Attacher::AttachEngine3D
  Height = 20
  Placement = pos=(0,-56,2) rot=(0,0,1;0rad)
  Radius = 1.5
FEATURE [Part::Cylinder] Cylinder1433  label="Válec1433"
  Angle = 360
  AttacherType = Attacher::AttachEngine3D
  Height = 20
  Placement = pos=(56,0,2) rot=(0,0,1;1.5708rad)
  Radius = 1.5
FEATURE [Part::Cylinder] Cylinder1434  label="Válec1434"
  Angle = 360
  AttacherType = Attacher::AttachEngine3D
  Height = 20
  Placement = pos=(39.598,39.598,2) rot=(0,0,1;2.35619rad)
  Radius = 1.5
FEATURE [Part::Cylinder] Cylinder1435  label="Válec1435"
  Angle = 360
  AttacherType = Attacher::AttachEngine3D
  Height = 20
  Placement = pos=(-1.2e-14,56,2) rot=(0,0,1;3.14159rad)
  Radius = 1.5
FEATURE [Part::Cylinder] Cylinder1436  label="Válec1436"
  Angle = 360
  AttacherType = Attacher::AttachEngine3D
  Height = 20
  Placement = pos=(-39.598,39.598,2) rot=(0,0,1;3.92699rad)
  Radius = 1.5
FEATURE [Part::FeaturePython] Tube090  # WARN: FeaturePython — macro-defined, semantics opaque (R4)
  AttacherType = Attacher::AttachEngine3D
  Height = 25
  InnerRadius = 53
  OuterRadius = 60
  Placement = pos=(0,0,20) rot=(0,0,1;0rad)
FEATURE [Part::Cylinder] Cylinder1437  label="Válec1437"
  Angle = 360
  AttacherType = Attacher::AttachEngine3D
  Height = 20
  Placement = pos=(-56,-1.3e-14,2) rot=(0,0,-1;1.5708rad)
  Radius = 1.5
FEATURE [Part::Cylinder] Cylinder1438  label="Válec1438"
  Angle = 360
  AttacherType = Attacher::AttachEngine3D
  Height = 20
  Placement = pos=(-39.598,-39.598,2) rot=(0,0,-1;0.785398rad)
  Radius = 1.5
FEATURE [Part::Compound] Compound852
  Links = -> [Cylinder1432,Cylinder1430,Cylinder1433,Cylinder1434,Cylinder1435,Cylinder1436,Cylinder1437,Cylinder1438]
  Placement = pos=(0,0,10) rot=(0,0,1;0rad)
FEATURE [Part::Box] Box476  label="Krychle476"
  AttacherType = Attacher::AttachEngine3D
  Height = 2
  Length = 6
  Placement = pos=(-3,-60,23) rot=(0,0,1;0rad)
  Width = 8
FEATURE [Part::Box] Box477  label="Krychle477"
  AttacherType = Attacher::AttachEngine3D
  Height = 2
  Length = 6
  Placement = pos=(40.3051,-44.5477,23) rot=(0,0,1;0.785398rad)
  Width = 8
FEATURE [Part::Box] Box478  label="Krychle478"
  AttacherType = Attacher::AttachEngine3D
  Height = 2
  Length = 6
  Placement = pos=(60,-3,23) rot=(0,0,1;1.5708rad)
  Width = 8
FEATURE [Part::Box] Box479  label="Krychle479"
  AttacherType = Attacher::AttachEngine3D
  Height = 2
  Length = 6
  Placement = pos=(44.5477,40.3051,23) rot=(0,0,1;2.35619rad)
  Width = 8
FEATURE [Part::Box] Box480  label="Krychle480"
  AttacherType = Attacher::AttachEngine3D
  Height = 2
  Length = 6
  Placement = pos=(3,60,23) rot=(0,0,1;3.14159rad)
  Width = 8
FEATURE [Part::Box] Box481  label="Krychle481"
  AttacherType = Attacher::AttachEngine3D
  Height = 2
  Length = 6
  Placement = pos=(-40.3051,44.5477,23) rot=(0,0,1;3.92699rad)
  Width = 8
FEATURE [Part::Box] Box482  label="Krychle482"
  AttacherType = Attacher::AttachEngine3D
  Height = 2
  Length = 6
  Placement = pos=(-60,3,23) rot=(0,0,-1;1.5708rad)
  Width = 8
FEATURE [Part::Box] Box483  label="Krychle483"
  AttacherType = Attacher::AttachEngine3D
  Height = 2
  Length = 6
  Placement = pos=(-44.5477,-40.3051,23) rot=(0,0,-1;0.785398rad)
  Width = 8
FEATURE [Part::Cylinder] Cylinder1439  label="Válec1439"
  Angle = 360
  AttacherType = Attacher::AttachEngine3D
  Height = 25
  Placement = pos=(0,0,20) rot=(0,0,1;0rad)
  Radius = 60
FEATURE [Part::Box] Box484  label="Krychle484"
  AttacherType = Attacher::AttachEngine3D
  Height = 25
  Length = 108
  Placement = pos=(-54,-53,20) rot=(0,0,1;0rad)
  Width = 46
FEATURE [Part::Cut] Cut458
  Base = -> Box484
  Tool = -> Cylinder1439
FEATURE [Part::Cut] Cut468
  Base = -> Cut458
  Tool = -> Compound851
FEATURE [Part::Cylinder] Cylinder1440  label="Válec1440"
  Angle = 360
  AttacherType = Attacher::AttachEngine3D
  Height = 40
  Placement = pos=(0,-17,27) rot=(1,0,0;1.5708rad)
  Radius = 59
FEATURE [Part::Box] Box485  label="Krychle485"
  AttacherType = Attacher::AttachEngine3D
  Height = 6
  Length = 6
  Placement = pos=(36,-47,56) rot=(0,0,1;0rad)
  Width = 2
FEATURE [Part::Cylinder] Cylinder1441  label="Válec1441"
  Angle = 360
  AttacherType = Attacher::AttachEngine3D
  Height = 40
  Placement = pos=(39,-40,59) rot=(1,0,0;1.5708rad)
  Radius = 1.5
FEATURE [Part::Cylinder] Cylinder1442  label="Válec1442"
  Angle = 360
  AttacherType = Attacher::AttachEngine3D
  Height = 40
  Placement = pos=(-39,-40,59) rot=(1,0,0;1.5708rad)
  Radius = 1.5
FEATURE [Part::Compound] Compound847
  Links = -> [Cylinder1441,Cylinder1442]
  Placement = pos=(0,0,-5) rot=(0,0,1;0rad)
FEATURE [Part::Box] Box486  label="Krychle486"
  AttacherType = Attacher::AttachEngine3D
  Height = 6
  Length = 6
  Placement = pos=(-42,-47,56) rot=(0,0,1;0rad)
  Width = 2
FEATURE [Part::Compound] Compound850
  Links = -> [Box486,Box485]
  Placement = pos=(0,2,-5) rot=(0,0,1;0rad)
FEATURE [Part::Box] Box487  label="Krychle487"
  AttacherType = Attacher::AttachEngine3D
  Height = 6
  Length = 6
  Placement = pos=(36,-47,56) rot=(0,0,1;0rad)
  Width = 2
FEATURE [Part::Box] Box488  label="Krychle488"
  AttacherType = Attacher::AttachEngine3D
  Height = 6
  Length = 6
  Placement = pos=(-42,-47,56) rot=(0,0,1;0rad)
  Width = 2
FEATURE [Part::Compound] Compound849
  Links = -> [Box488,Box487]
  Placement = pos=(0,2,-5) rot=(0,0,1;0rad)
FEATURE [Part::Cylinder] Cylinder1443  label="Válec1443"
  Angle = 360
  AttacherType = Attacher::AttachEngine3D
  Height = 40
  Placement = pos=(39,-40,59) rot=(1,0,0;1.5708rad)
  Radius = 1.5
FEATURE [Part::Cylinder] Cylinder1327  label="Válec1327"
  Angle = 360
  AttacherType = Attacher::AttachEngine3D
  Height = 40
  Placement = pos=(-39,-40,59) rot=(1,0,0;1.5708rad)
  Radius = 1.5
FEATURE [Part::Compound] Compound848
  Links = -> [Cylinder1443,Cylinder1327]
  Placement = pos=(0,2,-5) rot=(0,0,1;0rad)
FEATURE [Part::Compound] Compound853
  Links = -> [Box474,Box475]
  Placement = pos=(0,0,-11) rot=(0,0,1;0rad)
FEATURE [Part::Cut] Cut455
  Base = -> Cut468
  Placement = pos=(0,0,12) rot=(0,0,1;0rad)
  Tool = -> Compound853
FEATURE [Part::Common] Common002
  Base = -> Cut455
  Tool = -> Cylinder1440
FEATURE [Part::Cut] Cut470
  Base = -> Common002
  Tool = -> Compound850
FEATURE [Part::Cut] Cut471
  Base = -> Cut470
  Tool = -> Compound847
FEATURE [Part::Compound] Compound854
  Links = -> [Cylinder1421,Cylinder1422,Cylinder1418,Cylinder1415,Cylinder1419,Cylinder1417,Cylinder1420,Cylinder1423]
FEATURE [Part::Compound] Compound855
  Links = -> [Box476,Box477,Box478,Box479,Box480,Box481,Box482,Box483]
  Placement = pos=(0,0,1) rot=(0,0,1;0rad)
FEATURE [Part::Compound] Compound856
  Links = -> [Cylinder1425,Cylinder1426]
  Placement = pos=(0,8,2) rot=(0,0,1;0rad)
FEATURE [Part::Compound] Compound857
  Links = -> [Box472,Box473,Box471,Box470,Box469,Box468,Box467,Box466]
  Placement = pos=(0,0,1) rot=(0,0,1;0rad)
FEATURE [Part::Compound] Compound858
  Links = -> [Cylinder1414,Cylinder1416]
FEATURE [Part::Compound] Compound859
  Links = -> [Box464,Box465]
FEATURE [Part::Cut] Cut460
  Base = -> Compound859
  Tool = -> Compound854
FEATURE [Part::Cut] Cut461
  Base = -> Cut460
  Placement = pos=(0,0,10) rot=(0,0,1;0rad)
  Tool = -> Compound858
FEATURE [Part::Cut] Cut463
  Base = -> Tube090
  Tool = -> Torus004
FEATURE [Part::Cut] Cut462
  Base = -> Cut463
  Tool = -> Cylinder1429
FEATURE [Part::Cut] Cut456  label="J-max_lozo-harmo006"
  Base = -> Cut462
  Tool = -> Cylinder1431
FEATURE [Part::Cut] Cut457
  Base = -> Cut456
  Tool = -> Compound852
FEATURE [Part::Cut] Cut464
  Base = -> Cut457
  Placement = pos=(0,0,12) rot=(0,0,1;0rad)
  Tool = -> Compound855
FEATURE [Part::Cut] Cut459
  Base = -> Cut464
  Tool = -> Compound849
FEATURE [Part::Cut] Cut469
  Base = -> Cut459
  Tool = -> Compound848
FEATURE [Part::Cut] Cut465
  Base = -> Cut461
  Tool = -> Cylinder1424
FEATURE [Part::Cut] Cut466
  Base = -> Cut465
  Tool = -> Compound857
FEATURE [Part::Cut] Cut467
  Base = -> Cut466
  Placement = pos=(0,0,12) rot=(0,0,1;0rad)
  Tool = -> Compound856
FEATURE [Part::Fillet] Fillet019
  Base = -> Cut467
  Edges = 2 edges r=8: [Edge8,Edge63]
FEATURE [Part::Compound] Compound860  label="J-max-deep_bearing-ring"
  Links = -> [Cut469,Fillet019,Cut471]
  Placement = pos=(0,27,-53) rot=(0,0.707107,-0.707107;3.14159rad)
FEATURE [Sketcher::SketchObject] Sketch004
  FullyConstrained = false
  sketch-geometry (1):
    g0: Circle CenterX=-186.411 CenterY=73.9277 CenterZ=0 NormalX=0 NormalY=0 NormalZ=1 AngleXU=0 Radius=59
FEATURE [Part::Extrusion] Extrude002
  Base = -> Sketch004
  Dir = (52,0,32)
  DirMode = 0
  FaceMakerClass = Part::FaceMakerBullseye
  LengthFwd = 61
  LengthRev = 0
  Placement = pos=(-134,74,-22) rot=(0,0,1;3.14159rad)
  Solid = true
  Symmetric = false
FEATURE [Part::Cylinder] Cylinder1444  label="Válec1444"
  Angle = 360
  AttacherType = Attacher::AttachEngine3D
  Height = 100
  Placement = pos=(16,34,-90) rot=(0,0,1;0rad)
  Radius = 4
FEATURE [Part::Cylinder] Cylinder1445  label="Válec1445"
  Angle = 360
  AttacherType = Attacher::AttachEngine3D
  Height = 100
  Placement = pos=(-34,-16,-90) rot=(0,0,1;0rad)
  Radius = 4
FEATURE [Part::Cylinder] Cylinder1446  label="Válec1446"
  Angle = 360
  AttacherType = Attacher::AttachEngine3D
  Height = 100
  Placement = pos=(-16,34,-90) rot=(0,0,1;0rad)
  Radius = 4
FEATURE [Part::Cylinder] Cylinder1447  label="Válec1447"
  Angle = 360
  AttacherType = Attacher::AttachEngine3D
  Height = 100
  Placement = pos=(-16,-34,-90) rot=(0,0,1;0rad)
  Radius = 4
FEATURE [Part::Cylinder] Cylinder1448  label="Válec1448"
  Angle = 360
  AttacherType = Attacher::AttachEngine3D
  Height = 100
  Placement = pos=(34,-16,-90) rot=(0,0,1;0rad)
  Radius = 4
FEATURE [Part::Cylinder] Cylinder1449  label="Válec1449"
  Angle = 360
  AttacherType = Attacher::AttachEngine3D
  Height = 100
  Placement = pos=(10,-36,-90) rot=(0,0,1;0rad)
  Radius = 4
FEATURE [Part::Cylinder] Cylinder1450  label="Válec1450"
  Angle = 360
  AttacherType = Attacher::AttachEngine3D
  Height = 100
  Placement = pos=(16,34,-60) rot=(0,0,1;0rad)
  Radius = 1.5
FEATURE [Part::Cylinder] Cylinder1451  label="Válec1451"
  Angle = 360
  AttacherType = Attacher::AttachEngine3D
  Height = 100
  Placement = pos=(-34,16,-60) rot=(0,0,1;0rad)
  Radius = 1.5
FEATURE [Part::Cylinder] Cylinder1452  label="Válec1452"
  Angle = 360
  AttacherType = Attacher::AttachEngine3D
  Height = 100
  Placement = pos=(-34,-16,-60) rot=(0,0,1;0rad)
  Radius = 1.5
FEATURE [Part::Cylinder] Cylinder1453  label="Válec1453"
  Angle = 360
  AttacherType = Attacher::AttachEngine3D
  Height = 100
  Placement = pos=(34,-16,-60) rot=(0,0,1;0rad)
  Radius = 1.5
FEATURE [Part::Cylinder] Cylinder1454  label="Válec1454"
  Angle = 360
  AttacherType = Attacher::AttachEngine3D
  Height = 100
  Placement = pos=(34,16,-60) rot=(0,0,1;0rad)
  Radius = 1.5
FEATURE [Part::Cylinder] Cylinder1455  label="Válec1455"
  Angle = 360
  AttacherType = Attacher::AttachEngine3D
  Height = 100
  Placement = pos=(10,-36,-60) rot=(0,0,1;0rad)
  Radius = 1.5
FEATURE [Part::Box] Box515  label="Krychle515"
  AttacherType = Attacher::AttachEngine3D
  Height = 100
  Length = 200
  Placement = pos=(-60,-134,-90) rot=(0,0,1;0rad)
  Width = 100
FEATURE [Part::Box] Box516  label="Krychle516"
  AttacherType = Attacher::AttachEngine3D
  Height = 100
  Length = 200
  Placement = pos=(-60,44,-90) rot=(0,0,1;0rad)
  Width = 100
FEATURE [Part::Cylinder] Cylinder1456  label="Válec1456"
  Angle = 360
  AttacherType = Attacher::AttachEngine3D
  Height = 100
  Placement = pos=(90,0,-60) rot=(0,0,1;0rad)
  Radius = 1.5
FEATURE [Part::Cylinder] Cylinder1457  label="Válec1457"
  Angle = 360
  AttacherType = Attacher::AttachEngine3D
  Height = 100
  Placement = pos=(14,0,-60) rot=(0,0,1;0rad)
  Radius = 1.5
FEATURE [Part::Cylinder] Cylinder1458  label="Válec1458"
  Angle = 360
  AttacherType = Attacher::AttachEngine3D
  Height = 100
  Placement = pos=(90,0,-18) rot=(0,0,1;0rad)
  Radius = 4
FEATURE [Part::Cylinder] Cylinder1459  label="Válec1459"
  Angle = 360
  AttacherType = Attacher::AttachEngine3D
  Height = 100
  Placement = pos=(14,0,-18) rot=(0,0,1;0rad)
  Radius = 4
FEATURE [Part::Compound] Compound891  label="srouby_troj_silne002"
  Links = -> [Cylinder1458,Cylinder1459]
FEATURE [Part::Compound] Compound892  label="srouby_troj009"
  Links = -> [Cylinder1456,Cylinder1457]
FEATURE [Part::Box] Box517  label="Krychle517"
  AttacherType = Attacher::AttachEngine3D
  Height = 2
  Length = 6
  Placement = pos=(75,38,-22) rot=(0,0,1;0rad)
  Width = 6
FEATURE [Part::Box] Box518  label="Krychle518"
  AttacherType = Attacher::AttachEngine3D
  Height = 2
  Length = 6
  Placement = pos=(23,38,-22) rot=(0,0,1;0rad)
  Width = 6
FEATURE [Part::Compound] Compound889
  Links = -> [Box517,Box518]
FEATURE [Part::Cylinder] Cylinder1460  label="Válec1460"
  Angle = 360
  AttacherType = Attacher::AttachEngine3D
  Height = 32
  Placement = pos=(26,41,-46) rot=(0,0,1;0rad)
  Radius = 1.5
FEATURE [Part::Cylinder] Cylinder1461  label="Válec1461"
  Angle = 360
  AttacherType = Attacher::AttachEngine3D
  Height = 32
  Placement = pos=(78,41,-46) rot=(0,0,1;0rad)
  Radius = 1.5
FEATURE [Part::Compound] Compound890
  Links = -> [Cylinder1460,Cylinder1461]
FEATURE [Part::Cylinder] Cylinder1462  label="Válec1462"
  Angle = 360
  AttacherType = Attacher::AttachEngine3D
  Height = 100
  Placement = pos=(-34,16,-90) rot=(0,0,1;0rad)
  Radius = 4
FEATURE [Part::Cylinder] Cylinder1463  label="Válec1463"
  Angle = 360
  AttacherType = Attacher::AttachEngine3D
  Height = 100
  Placement = pos=(34,16,-90) rot=(0,0,1;0rad)
  Radius = 4
FEATURE [Part::Compound] Compound887  label="sbouby_baze_silne003"
  Links = -> [Cylinder1445,Cylinder1446,Cylinder1447,Cylinder1448,Cylinder1444,Cylinder1449,Cylinder1462,Cylinder1463]
FEATURE [Part::Cylinder] Cylinder1464  label="Válec1464"
  Angle = 360
  AttacherType = Attacher::AttachEngine3D
  Height = 100
  Placement = pos=(-16,-34,-60) rot=(0,0,1;0rad)
  Radius = 1.5
FEATURE [Part::Cylinder] Cylinder1465  label="Válec1465"
  Angle = 360
  AttacherType = Attacher::AttachEngine3D
  Height = 100
  Placement = pos=(-16,34,-60) rot=(0,0,1;0rad)
  Radius = 1.5
FEATURE [Part::Compound] Compound888  label="sbouby_baze002"
  Links = -> [Cylinder1451,Cylinder1452,Cylinder1453,Cylinder1454,Cylinder1450,Cylinder1455,Cylinder1464,Cylinder1465]
FEATURE [Part::Cylinder] Cylinder1466  label="Válec1466"
  Angle = 360
  AttacherType = Attacher::AttachEngine3D
  Height = 100
  Placement = pos=(-34,16,-60) rot=(0,0,1;0rad)
  Radius = 1.5
FEATURE [Part::Cylinder] Cylinder1467  label="Válec1467"
  Angle = 360
  AttacherType = Attacher::AttachEngine3D
  Height = 100
  Placement = pos=(-34,-16,-60) rot=(0,0,1;0rad)
  Radius = 1.5
FEATURE [Part::Cylinder] Cylinder1468  label="Válec1468"
  Angle = 360
  AttacherType = Attacher::AttachEngine3D
  Height = 100
  Placement = pos=(34,-16,-60) rot=(0,0,1;0rad)
  Radius = 1.5
FEATURE [Part::Cylinder] Cylinder1469  label="Válec1469"
  Angle = 360
  AttacherType = Attacher::AttachEngine3D
  Height = 100
  Placement = pos=(34,16,-60) rot=(0,0,1;0rad)
  Radius = 1.5
FEATURE [Part::Cylinder] Cylinder1470  label="Válec1470"
  Angle = 360
  AttacherType = Attacher::AttachEngine3D
  Height = 100
  Placement = pos=(16,34,-60) rot=(0,0,1;0rad)
  Radius = 1.5
FEATURE [Part::Cylinder] Cylinder1471  label="Válec1471"
  Angle = 360
  AttacherType = Attacher::AttachEngine3D
  Height = 100
  Placement = pos=(10,-36,-60) rot=(0,0,1;0rad)
  Radius = 1.5
FEATURE [Part::Cylinder] Cylinder1472  label="Válec1472"
  Angle = 360
  AttacherType = Attacher::AttachEngine3D
  Height = 100
  Placement = pos=(-16,-34,-60) rot=(0,0,1;0rad)
  Radius = 1.5
FEATURE [Part::Cylinder] Cylinder1473  label="Válec1473"
  Angle = 360
  AttacherType = Attacher::AttachEngine3D
  Height = 100
  Placement = pos=(-16,34,-60) rot=(0,0,1;0rad)
  Radius = 1.5
FEATURE [Part::Compound] Compound893  label="sbouby_baze003"
  Links = -> [Cylinder1466,Cylinder1467,Cylinder1468,Cylinder1469,Cylinder1470,Cylinder1471,Cylinder1472,Cylinder1473]
FEATURE [Part::Cylinder] Cylinder1474  label="Válec1474"
  Angle = 360
  AttacherType = Attacher::AttachEngine3D
  Height = 16
  Placement = pos=(0,0,2) rot=(0,0,1;0rad)
  Radius = 59
FEATURE [Part::Cylinder] Cylinder1475  label="Válec1475"
  Angle = 360
  AttacherType = Attacher::AttachEngine3D
  Height = 20
  Placement = pos=(103,-12,-20) rot=(0,0,1;0rad)
  Radius = 4
FEATURE [Part::Cylinder] Cylinder1476  label="Válec1476"
  Angle = 360
  AttacherType = Attacher::AttachEngine3D
  Height = 20
  Placement = pos=(103,12,-20) rot=(0,0,1;0rad)
  Radius = 4
FEATURE [Part::Cylinder] Cylinder1477  label="Válec1477"
  Angle = 360
  AttacherType = Attacher::AttachEngine3D
  Height = 20
  Placement = pos=(76,24,-18) rot=(0,0,1;0rad)
  Radius = 4
FEATURE [Part::Cylinder] Cylinder1478  label="Válec1478"
  Angle = 360
  AttacherType = Attacher::AttachEngine3D
  Height = 20
  Placement = pos=(91,-27,-18) rot=(0,0,1;0rad)
  Radius = 4
FEATURE [Part::Cylinder] Cylinder1479  label="Válec1479"
  Angle = 360
  AttacherType = Attacher::AttachEngine3D
  Height = 40
  Placement = pos=(13,-27,-18) rot=(0,0,1;0rad)
  Radius = 4
FEATURE [Part::Cylinder] Cylinder1480  label="Válec1480"
  Angle = 360
  AttacherType = Attacher::AttachEngine3D
  Height = 40
  Placement = pos=(28,24,-18) rot=(0,0,1;0rad)
  Radius = 4
FEATURE [Part::Cylinder] Cylinder1481  label="Válec1481"
  Angle = 360
  AttacherType = Attacher::AttachEngine3D
  Height = 40
  Placement = pos=(1,-12,-18) rot=(0,0,1;0rad)
  Radius = 4
FEATURE [Part::Cylinder] Cylinder1482  label="Válec1482"
  Angle = 360
  AttacherType = Attacher::AttachEngine3D
  Height = 40
  Placement = pos=(1,12,-18) rot=(0,0,1;0rad)
  Radius = 4
FEATURE [Part::Compound] Compound894  label="srouby_monoblok_silne004"
  Links = -> [Cylinder1475,Cylinder1476,Cylinder1477,Cylinder1478,Cylinder1479,Cylinder1480,Cylinder1481,Cylinder1482]
FEATURE [Part::Cut] Cut305
  Base = -> Cylinder1474
  Tool = -> Compound894
FEATURE [Part::Cylinder] Cylinder1483  label="Válec1483"
  Angle = 360
  AttacherType = Attacher::AttachEngine3D
  Height = 100
  Placement = pos=(90,0,-18) rot=(0,0,1;0rad)
  Radius = 4
FEATURE [Part::Cylinder] Cylinder1484  label="Válec1484"
  Angle = 360
  AttacherType = Attacher::AttachEngine3D
  Height = 100
  Placement = pos=(14,0,-18) rot=(0,0,1;0rad)
  Radius = 4
FEATURE [Part::Compound] Compound896  label="srouby_troj_silne003"
  Links = -> [Cylinder1483,Cylinder1484]
FEATURE [Part::Cylinder] Cylinder1485  label="Válec1485"
  Angle = 360
  AttacherType = Attacher::AttachEngine3D
  Height = 100
  Placement = pos=(-16,-34,-90) rot=(0,0,1;0rad)
  Radius = 4
FEATURE [Part::Cylinder] Cylinder1486  label="Válec1486"
  Angle = 360
  AttacherType = Attacher::AttachEngine3D
  Height = 100
  Placement = pos=(-34,-16,-90) rot=(0,0,1;0rad)
  Radius = 4
FEATURE [Part::Cylinder] Cylinder1487  label="Válec1487"
  Angle = 360
  AttacherType = Attacher::AttachEngine3D
  Height = 100
  Placement = pos=(-16,34,-90) rot=(0,0,1;0rad)
  Radius = 4
FEATURE [Part::Cylinder] Cylinder1488  label="Válec1488"
  Angle = 360
  AttacherType = Attacher::AttachEngine3D
  Height = 100
  Placement = pos=(34,-16,-90) rot=(0,0,1;0rad)
  Radius = 4
FEATURE [Part::Cylinder] Cylinder1489  label="Válec1489"
  Angle = 360
  AttacherType = Attacher::AttachEngine3D
  Height = 100
  Placement = pos=(16,34,-90) rot=(0,0,1;0rad)
  Radius = 4
FEATURE [Part::Cylinder] Cylinder1490  label="Válec1490"
  Angle = 360
  AttacherType = Attacher::AttachEngine3D
  Height = 100
  Placement = pos=(10,-36,-90) rot=(0,0,1;0rad)
  Radius = 4
FEATURE [Part::Cylinder] Cylinder1491  label="Válec1491"
  Angle = 360
  AttacherType = Attacher::AttachEngine3D
  Height = 100
  Placement = pos=(-34,16,-90) rot=(0,0,1;0rad)
  Radius = 4
FEATURE [Part::Cylinder] Cylinder1326  label="Válec1326"
  Angle = 360
  AttacherType = Attacher::AttachEngine3D
  Height = 100
  Placement = pos=(34,16,-90) rot=(0,0,1;0rad)
  Radius = 4
FEATURE [Part::Compound] Compound895  label="sbouby_baze_silne004"
  Links = -> [Cylinder1486,Cylinder1487,Cylinder1485,Cylinder1488,Cylinder1489,Cylinder1490,Cylinder1491,Cylinder1326]
FEATURE [Part::Cut] Cut306
  Base = -> Cut305
  Tool = -> Compound895
FEATURE [Part::Cut] Cut307
  Base = -> Cut306
  Tool = -> Compound893
FEATURE [Part::Chamfer] Chamfer038
  Base = -> Cut307
  Edges = 1 edges r=4: [Edge3]
FEATURE [Part::Cut] Cut308
  Base = -> Chamfer038
  Placement = pos=(0,0,4) rot=(0,0,1;0rad)
  Tool = -> Compound896
FEATURE [Part::Cylinder] Cylinder1492  label="Válec1492"
  Angle = 360
  AttacherType = Attacher::AttachEngine3D
  Height = 100
  Placement = pos=(103,-12,-60) rot=(0,0,1;0rad)
  Radius = 1.5
FEATURE [Part::Cylinder] Cylinder1493  label="Válec1493"
  Angle = 360
  AttacherType = Attacher::AttachEngine3D
  Height = 100
  Placement = pos=(103,12,-60) rot=(0,0,1;0rad)
  Radius = 1.5
FEATURE [Part::Cylinder] Cylinder1494  label="Válec1494"
  Angle = 360
  AttacherType = Attacher::AttachEngine3D
  Height = 100
  Placement = pos=(76,24,-60) rot=(0,0,1;0rad)
  Radius = 1.5
FEATURE [Part::Cylinder] Cylinder1495  label="Válec1495"
  Angle = 360
  AttacherType = Attacher::AttachEngine3D
  Height = 100
  Placement = pos=(91,-27,-60) rot=(0,0,1;0rad)
  Radius = 1.5
FEATURE [Part::Cylinder] Cylinder1496  label="Válec1496"
  Angle = 360
  AttacherType = Attacher::AttachEngine3D
  Height = 100
  Placement = pos=(13,-27,-60) rot=(0,0,1;0rad)
  Radius = 1.5
FEATURE [Part::Cylinder] Cylinder1497  label="Válec1497"
  Angle = 360
  AttacherType = Attacher::AttachEngine3D
  Height = 100
  Placement = pos=(28,24,-60) rot=(0,0,1;0rad)
  Radius = 1.5
FEATURE [Part::Cylinder] Cylinder1498  label="Válec1498"
  Angle = 360
  AttacherType = Attacher::AttachEngine3D
  Height = 100
  Placement = pos=(1,-12,-60) rot=(0,0,1;0rad)
  Radius = 1.5
FEATURE [Part::Cylinder] Cylinder1499  label="Válec1499"
  Angle = 360
  AttacherType = Attacher::AttachEngine3D
  Height = 100
  Placement = pos=(1,12,-60) rot=(0,0,1;0rad)
  Radius = 1.5
FEATURE [Part::Compound] Compound885  label="srouby_monoblok002"
  Links = -> [Cylinder1492,Cylinder1493,Cylinder1494,Cylinder1495,Cylinder1496,Cylinder1497,Cylinder1498,Cylinder1499]
FEATURE [Part::Cut] Cut296
  Base = -> Extrude002
  Tool = -> Compound885
FEATURE [Part::Cylinder] Cylinder1500  label="Válec1500"
  Angle = 360
  AttacherType = Attacher::AttachEngine3D
  Height = 20
  Placement = pos=(103,-12,-20) rot=(0,0,1;0rad)
  Radius = 4
FEATURE [Part::Cylinder] Cylinder1501  label="Válec1501"
  Angle = 360
  AttacherType = Attacher::AttachEngine3D
  Height = 20
  Placement = pos=(103,12,-20) rot=(0,0,1;0rad)
  Radius = 4
FEATURE [Part::Cylinder] Cylinder1502  label="Válec1502"
  Angle = 360
  AttacherType = Attacher::AttachEngine3D
  Height = 20
  Placement = pos=(76,24,-18) rot=(0,0,1;0rad)
  Radius = 4
FEATURE [Part::Cylinder] Cylinder1503  label="Válec1503"
  Angle = 360
  AttacherType = Attacher::AttachEngine3D
  Height = 20
  Placement = pos=(91,-27,-18) rot=(0,0,1;0rad)
  Radius = 4
FEATURE [Part::Cylinder] Cylinder1504  label="Válec1504"
  Angle = 360
  AttacherType = Attacher::AttachEngine3D
  Height = 40
  Placement = pos=(13,-27,-18) rot=(0,0,1;0rad)
  Radius = 4
FEATURE [Part::Cylinder] Cylinder1505  label="Válec1505"
  Angle = 360
  AttacherType = Attacher::AttachEngine3D
  Height = 40
  Placement = pos=(28,24,-18) rot=(0,0,1;0rad)
  Radius = 4
FEATURE [Part::Cylinder] Cylinder1506  label="Válec1506"
  Angle = 360
  AttacherType = Attacher::AttachEngine3D
  Height = 40
  Placement = pos=(1,-12,-18) rot=(0,0,1;0rad)
  Radius = 4
FEATURE [Part::Cylinder] Cylinder1507  label="Válec1507"
  Angle = 360
  AttacherType = Attacher::AttachEngine3D
  Height = 40
  Placement = pos=(1,12,-18) rot=(0,0,1;0rad)
  Radius = 4
FEATURE [Part::Compound] Compound886  label="srouby_monoblok_silne003"
  Links = -> [Cylinder1500,Cylinder1501,Cylinder1502,Cylinder1503,Cylinder1504,Cylinder1505,Cylinder1506,Cylinder1507]
FEATURE [Part::Cut] Cut295
  Base = -> Cut296
  Tool = -> Compound886
FEATURE [Part::Cut] Cut297
  Base = -> Cut295
  Tool = -> Compound887
FEATURE [Part::Cut] Cut298
  Base = -> Cut297
  Tool = -> Compound888
FEATURE [Part::Cut] Cut299
  Base = -> Cut298
  Tool = -> Box515
FEATURE [Part::Cut] Cut300
  Base = -> Cut299
  Tool = -> Box516
FEATURE [Part::Cut] Cut301
  Base = -> Cut300
  Tool = -> Compound889
FEATURE [Part::Cut] Cut302
  Base = -> Cut301
  Tool = -> Compound890
FEATURE [Part::Cut] Cut303
  Base = -> Cut302
  Tool = -> Compound892
FEATURE [Part::Cut] Cut304
  Base = -> Cut303
  Tool = -> Compound891
FEATURE [Part::Cylinder] Cylinder1508  label="Válec1508"
  Angle = 360
  AttacherType = Attacher::AttachEngine3D
  Height = 4
  Placement = pos=(52,0,-26) rot=(0,0,1;0rad)
  Radius = 59
FEATURE [Part::Cylinder] Cylinder1509  label="Válec1509"
  Angle = 360
  AttacherType = Attacher::AttachEngine3D
  Height = 100
  Placement = pos=(103,-12,-60) rot=(0,0,1;0rad)
  Radius = 1.5
FEATURE [Part::Cylinder] Cylinder1510  label="Válec1510"
  Angle = 360
  AttacherType = Attacher::AttachEngine3D
  Height = 100
  Placement = pos=(103,12,-60) rot=(0,0,1;0rad)
  Radius = 1.5
FEATURE [Part::Cylinder] Cylinder1511  label="Válec1511"
  Angle = 360
  AttacherType = Attacher::AttachEngine3D
  Height = 100
  Placement = pos=(76,24,-60) rot=(0,0,1;0rad)
  Radius = 1.5
FEATURE [Part::Cylinder] Cylinder1512  label="Válec1512"
  Angle = 360
  AttacherType = Attacher::AttachEngine3D
  Height = 100
  Placement = pos=(91,-27,-60) rot=(0,0,1;0rad)
  Radius = 1.5
FEATURE [Part::Cylinder] Cylinder1513  label="Válec1513"
  Angle = 360
  AttacherType = Attacher::AttachEngine3D
  Height = 100
  Placement = pos=(13,-27,-60) rot=(0,0,1;0rad)
  Radius = 1.5
FEATURE [Part::Cylinder] Cylinder1514  label="Válec1514"
  Angle = 360
  AttacherType = Attacher::AttachEngine3D
  Height = 100
  Placement = pos=(28,24,-60) rot=(0,0,1;0rad)
  Radius = 1.5
FEATURE [Part::Cylinder] Cylinder1515  label="Válec1515"
  Angle = 360
  AttacherType = Attacher::AttachEngine3D
  Height = 100
  Placement = pos=(1,-12,-60) rot=(0,0,1;0rad)
  Radius = 1.5
FEATURE [Part::Cylinder] Cylinder1516  label="Válec1516"
  Angle = 360
  AttacherType = Attacher::AttachEngine3D
  Height = 100
  Placement = pos=(1,12,-60) rot=(0,0,1;0rad)
  Radius = 1.5
FEATURE [Part::Compound] Compound897  label="srouby_monoblok003"
  Links = -> [Cylinder1509,Cylinder1510,Cylinder1511,Cylinder1512,Cylinder1513,Cylinder1514,Cylinder1515,Cylinder1516]
FEATURE [Part::Cut] Cut505
  Base = -> Cylinder1508
  Tool = -> Compound897
FEATURE [Part::Box] Box519  label="Krychle519"
  AttacherType = Attacher::AttachEngine3D
  Height = 100
  Length = 200
  Placement = pos=(-60,-130,-90) rot=(0,0,1;0rad)
  Width = 100
FEATURE [Part::Box] Box520  label="Krychle520"
  AttacherType = Attacher::AttachEngine3D
  Height = 100
  Length = 200
  Placement = pos=(-60,44,-90) rot=(0,0,1;0rad)
  Width = 100
FEATURE [Part::Cylinder] Cylinder1517  label="Válec1517"
  Angle = 360
  AttacherType = Attacher::AttachEngine3D
  Height = 100
  Placement = pos=(-34,-16,-90) rot=(0,0,1;0rad)
  Radius = 4
FEATURE [Part::Cylinder] Cylinder1518  label="Válec1518"
  Angle = 360
  AttacherType = Attacher::AttachEngine3D
  Height = 100
  Placement = pos=(-16,34,-90) rot=(0,0,1;0rad)
  Radius = 4
FEATURE [Part::Cylinder] Cylinder1519  label="Válec1519"
  Angle = 360
  AttacherType = Attacher::AttachEngine3D
  Height = 100
  Placement = pos=(-16,-34,-90) rot=(0,0,1;0rad)
  Radius = 4
FEATURE [Part::Cylinder] Cylinder1520  label="Válec1520"
  Angle = 360
  AttacherType = Attacher::AttachEngine3D
  Height = 100
  Placement = pos=(34,-16,-90) rot=(0,0,1;0rad)
  Radius = 4
FEATURE [Part::Cylinder] Cylinder1521  label="Válec1521"
  Angle = 360
  AttacherType = Attacher::AttachEngine3D
  Height = 100
  Placement = pos=(16,34,-90) rot=(0,0,1;0rad)
  Radius = 4
FEATURE [Part::Cylinder] Cylinder1522  label="Válec1522"
  Angle = 360
  AttacherType = Attacher::AttachEngine3D
  Height = 100
  Placement = pos=(16,-34,-90) rot=(0,0,1;0rad)
  Radius = 4
FEATURE [Part::Cylinder] Cylinder1523  label="Válec1523"
  Angle = 360
  AttacherType = Attacher::AttachEngine3D
  Height = 100
  Placement = pos=(-34,16,-90) rot=(0,0,1;0rad)
  Radius = 4
FEATURE [Part::Cylinder] Cylinder1524  label="Válec1524"
  Angle = 360
  AttacherType = Attacher::AttachEngine3D
  Height = 100
  Placement = pos=(34,16,-90) rot=(0,0,1;0rad)
  Radius = 4
FEATURE [Part::Compound] Compound898  label="sbouby_baze_silne005"
  Links = -> [Cylinder1517,Cylinder1518,Cylinder1519,Cylinder1520,Cylinder1521,Cylinder1522,Cylinder1523,Cylinder1524]
FEATURE [Part::Cut] Cut506
  Base = -> Cut505
  Tool = -> Compound898
FEATURE [Part::Cut] Cut507
  Base = -> Cut506
  Tool = -> Box519
FEATURE [Part::Cut] Cut508
  Base = -> Cut507
  Tool = -> Box520
FEATURE [Part::Cylinder] Cylinder1525  label="Válec1525"
  Angle = 360
  AttacherType = Attacher::AttachEngine3D
  Height = 32
  Placement = pos=(26,41,-42) rot=(0,0,1;0rad)
  Radius = 1.5
FEATURE [Part::Cylinder] Cylinder1526  label="Válec1526"
  Angle = 360
  AttacherType = Attacher::AttachEngine3D
  Height = 32
  Placement = pos=(78,41,-42) rot=(0,0,1;0rad)
  Radius = 1.5
FEATURE [Part::Cylinder] Cylinder1527  label="Válec1527"
  Angle = 360
  AttacherType = Attacher::AttachEngine3D
  Height = 100
  Placement = pos=(90,0,-60) rot=(0,0,1;0rad)
  Radius = 1.5
FEATURE [Part::Cylinder] Cylinder1528  label="Válec1528"
  Angle = 360
  AttacherType = Attacher::AttachEngine3D
  Height = 100
  Placement = pos=(14,0,-60) rot=(0,0,1;0rad)
  Radius = 1.5
FEATURE [Part::Chamfer] Chamfer
  Base = -> Cut304
  Edges = 1 edges r=4: [Edge44]
FEATURE [Part::Chamfer] Chamfer039
  Base = -> Chamfer
  Edges = 2 edges r=3.5: [Edge4,Edge6]
FEATURE [Part::Compound] Compound899
  Links = -> [Cylinder1525,Cylinder1526]
FEATURE [Part::Cut] Cut509
  Base = -> Cut508
  Tool = -> Compound899
FEATURE [Part::Compound] Compound900  label="srouby_troj010"
  Links = -> [Cylinder1527,Cylinder1528]
FEATURE [Part::Cut] Cut510
  Base = -> Cut509
  Tool = -> Compound900
FEATURE [Part::Compound] Compound901  label="Base_deep-neck"
  Links = -> [Chamfer039,Cut308,Cut510]
  Placement = pos=(-52,0,36) rot=(0,0,1;0rad)
FEATURE [Part::Cylinder] Cylinder1529  label="Válec1529"
  Angle = 360
  AttacherType = Attacher::AttachEngine3D
  Height = 58
  Placement = pos=(0,19,-53) rot=(1,0,0;1.5708rad)
  Radius = 60.2
FEATURE [Part::Cut] Cut511
  Base = -> Cut220
  Tool = -> Cylinder1529
FEATURE [Part::Compound] Compound902  label="Base_deep-triangle"
  Links = -> [Cut511,Cut228,Cut226,Cut222,Cut212]
FEATURE [Part::Cylinder] Cylinder2182  label="Válec2182"
  Angle = 360
  AttacherType = Attacher::AttachEngine3D
  Height = 160
  Placement = pos=(-18,0,-60) rot=(0,0,1;0rad)
  Radius = 17
FEATURE [Sketcher::SketchObject] Sketch005
  FullyConstrained = false
  MapMode = 5
  Support = -> [XY_Plane003]
  sketch-geometry (5):
    g0: LineSegment StartX=-53.11 StartY=25.5869 StartZ=0 EndX=-9.47198 EndY=128.297 EndZ=0
    g1: LineSegment StartX=-9.47198 StartY=128.297 StartZ=0 EndX=9.50803 EndY=128.154 EndZ=0
    g2: LineSegment StartX=9.50803 StartY=128.154 StartZ=0 EndX=53.1093 EndY=25.7412 EndZ=0
    g3: LineSegment StartX=53.1093 StartY=25.7412 StartZ=0 EndX=-0.067027 EndY=50.049 EndZ=0
    g4: LineSegment StartX=-0.067027 StartY=50.049 StartZ=0 EndX=-53.11 EndY=25.5869 EndZ=0
  constraints (5):
    c: Coincident(g0,g1)
    c: Coincident(g1,g2)
    c: Coincident(g2,g3)
    c: Coincident(g3,g4)
    c: Coincident(g4,g0)
FEATURE [PartDesign::Pad] Pad003
  Direction = (1,1,1)
  Length = 10
  Length2 = 100
  Profile = -> Sketch005
  Type = 0
FEATURE [Part::FeaturePython] Tube092  # WARN: FeaturePython — macro-defined, semantics opaque (R4)
  AttacherType = Attacher::AttachEngine3D
  Height = 10
  InnerRadius = 40
  OuterRadius = 59
FEATURE [Part::Cylinder] Cylinder2183  label="Válec2183"
  Angle = 360
  AttacherType = Attacher::AttachEngine3D
  Height = 32
  Placement = pos=(78,41,-42) rot=(0,0,1;0rad)
  Radius = 1.5
FEATURE [Part::Cylinder] Cylinder2184  label="Válec2184"
  Angle = 360
  AttacherType = Attacher::AttachEngine3D
  Height = 160
  Placement = pos=(-18,0,-60) rot=(0,0,1;0rad)
  Radius = 17
FEATURE [Part::Cylinder] Cylinder2185  label="Válec2185"
  Angle = 360
  AttacherType = Attacher::AttachEngine3D
  Height = 4
  Placement = pos=(7,-34,37) rot=(1,0,0;1.5708rad)
  Radius = 3
FEATURE [Part::Cylinder] Cylinder2186  label="Válec2186"
  Angle = 360
  AttacherType = Attacher::AttachEngine3D
  Height = 100
  Placement = pos=(51,-12,0) rot=(0,0,1;0rad)
  Radius = 1.5
FEATURE [Part::Box] Box521  label="Krychle521"
  AttacherType = Attacher::AttachEngine3D
  Height = 10
  Length = 10
  Placement = pos=(32,-24,0) rot=(0,0,1;0rad)
  Width = 52
FEATURE [Part::Cylinder] Cylinder2187  label="Válec2187"
  Angle = 360
  AttacherType = Attacher::AttachEngine3D
  Height = 20
  Placement = pos=(-7,-34,37) rot=(1,0,0;1.5708rad)
  Radius = 1.5
FEATURE [Part::Cylinder] Cylinder2188  label="Válec2188"
  Angle = 360
  AttacherType = Attacher::AttachEngine3D
  Height = 20
  Placement = pos=(-7,-34,37) rot=(1,0,0;1.5708rad)
  Radius = 1.5
FEATURE [Part::Cylinder] Cylinder2189  label="Válec2189"
  Angle = 360
  AttacherType = Attacher::AttachEngine3D
  Height = 50
  Placement = pos=(24,18,0) rot=(0,0,1;0rad)
  Radius = 1.5
FEATURE [Part::Cylinder] Cylinder2190  label="Válec2190"
  Angle = 360
  AttacherType = Attacher::AttachEngine3D
  Height = 10
  Placement = pos=(0,106,0) rot=(0,0,1;0rad)
  Radius = 10
FEATURE [Part::Box] Box522  label="Krychle522"
  AttacherType = Attacher::AttachEngine3D
  Height = 10
  Length = 10
  Placement = pos=(-42,-24,0) rot=(0,0,1;0rad)
  Width = 52
FEATURE [Part::Box] Box523  label="Krychle523"
  AttacherType = Attacher::AttachEngine3D
  Height = 32
  Length = 200
  Placement = pos=(-100,-130,0) rot=(0,0,1;0rad)
  Width = 100
FEATURE [Part::Cut] Cut515
  Base = -> Tube092
  Tool = -> Box523
FEATURE [Part::Cylinder] Cylinder2191  label="Válec2191"
  Angle = 360
  AttacherType = Attacher::AttachEngine3D
  Height = 4
  Placement = pos=(7,-34,73) rot=(1,0,0;1.5708rad)
  Radius = 3
FEATURE [Part::Cylinder] Cylinder2192  label="Válec2192"
  Angle = 360
  AttacherType = Attacher::AttachEngine3D
  Height = 4
  Placement = pos=(7,-34,37) rot=(1,0,0;1.5708rad)
  Radius = 3
FEATURE [Part::Cylinder] Cylinder2193  label="Válec2193"
  Angle = 360
  AttacherType = Attacher::AttachEngine3D
  Height = 4
  Placement = pos=(-7,-34,73) rot=(1,0,0;1.5708rad)
  Radius = 3
FEATURE [Part::Cylinder] Cylinder2194  label="Válec2194"
  Angle = 360
  AttacherType = Attacher::AttachEngine3D
  Height = 20
  Placement = pos=(-7,-34,73) rot=(1,0,0;1.5708rad)
  Radius = 1.5
FEATURE [Part::Cylinder] Cylinder2195  label="Válec2195"
  Angle = 360
  AttacherType = Attacher::AttachEngine3D
  Height = 20
  Placement = pos=(7,-34,73) rot=(1,0,0;1.5708rad)
  Radius = 1.5
FEATURE [Part::Cylinder] Cylinder2196  label="Válec2196"
  Angle = 360
  AttacherType = Attacher::AttachEngine3D
  Height = 20
  Placement = pos=(7,-34,37) rot=(1,0,0;1.5708rad)
  Radius = 1.5
FEATURE [Part::Cylinder] Cylinder2197  label="Válec2197"
  Angle = 360
  AttacherType = Attacher::AttachEngine3D
  Height = 50
  Placement = pos=(51,6,0) rot=(0,0,1;0rad)
  Radius = 1.5
FEATURE [Part::Box] Box524  label="Krychle524"
  AttacherType = Attacher::AttachEngine3D
  Height = 10
  Length = 72
  Placement = pos=(-36,-30,0) rot=(0,0,1;0rad)
  Width = 70
FEATURE [Part::Cylinder] Cylinder2198  label="Válec2198"
  Angle = 360
  AttacherType = Attacher::AttachEngine3D
  Height = 20
  Placement = pos=(7,-34,73) rot=(1,0,0;1.5708rad)
  Radius = 1.5
FEATURE [Part::Cylinder] Cylinder2199  label="Válec2199"
  Angle = 360
  AttacherType = Attacher::AttachEngine3D
  Height = 3
  Placement = pos=(26,41,-42) rot=(0,0,1;0rad)
  Radius = 3
FEATURE [Part::Cylinder] Cylinder2200  label="Válec2200"
  Angle = 360
  AttacherType = Attacher::AttachEngine3D
  Height = 50
  Placement = pos=(-24,18,0) rot=(0,0,1;0rad)
  Radius = 1.5
FEATURE [Part::Cylinder] Cylinder2201  label="Válec2201"
  Angle = 360
  AttacherType = Attacher::AttachEngine3D
  Height = 100
  Placement = pos=(14,0,-60) rot=(0,0,1;0rad)
  Radius = 1.5
FEATURE [Part::Cylinder] Cylinder2202  label="Válec2202"
  Angle = 360
  AttacherType = Attacher::AttachEngine3D
  Height = 20
  Placement = pos=(-7,-34,73) rot=(1,0,0;1.5708rad)
  Radius = 1.5
FEATURE [Part::Cylinder] Cylinder2203  label="Válec2203"
  Angle = 360
  AttacherType = Attacher::AttachEngine3D
  Height = 100
  Placement = pos=(39,-21,0) rot=(0,0,1;0rad)
  Radius = 1.5
FEATURE [Part::Cylinder] Cylinder2204  label="Válec2204"
  Angle = 360
  AttacherType = Attacher::AttachEngine3D
  Height = 4
  Placement = pos=(-7,-34,37) rot=(1,0,0;1.5708rad)
  Radius = 3
FEATURE [Part::Cylinder] Cylinder2205  label="Válec2205"
  Angle = 360
  AttacherType = Attacher::AttachEngine3D
  Height = 4
  Placement = pos=(-7,-34,73) rot=(1,0,0;1.5708rad)
  Radius = 3
FEATURE [Part::Cylinder] Cylinder2206  label="Válec2206"
  Angle = 360
  AttacherType = Attacher::AttachEngine3D
  Height = 100
  Placement = pos=(39,-21,0) rot=(0,0,1;0rad)
  Radius = 1.5
FEATURE [Part::Cylinder] Cylinder2207  label="Válec2207"
  Angle = 360
  AttacherType = Attacher::AttachEngine3D
  Height = 100
  Placement = pos=(-51,-12,0) rot=(0,0,1;0rad)
  Radius = 1.5
FEATURE [Part::Cylinder] Cylinder2208  label="Válec2208"
  Angle = 360
  AttacherType = Attacher::AttachEngine3D
  Height = 50
  Placement = pos=(-51,6,0) rot=(0,0,1;0rad)
  Radius = 1.5
FEATURE [Part::Cylinder] Cylinder2209  label="Válec2209"
  Angle = 360
  AttacherType = Attacher::AttachEngine3D
  Height = 20
  Placement = pos=(7,-34,37) rot=(1,0,0;1.5708rad)
  Radius = 1.5
FEATURE [Part::Cylinder] Cylinder2210  label="Válec2210"
  Angle = 360
  AttacherType = Attacher::AttachEngine3D
  Height = 100
  Placement = pos=(51,-12,0) rot=(0,0,1;0rad)
  Radius = 1.5
FEATURE [Part::Cylinder] Cylinder2211  label="Válec2211"
  Angle = 360
  AttacherType = Attacher::AttachEngine3D
  Height = 32
  Placement = pos=(26,41,-42) rot=(0,0,1;0rad)
  Radius = 1.5
FEATURE [Part::Cylinder] Cylinder2212  label="Válec2212"
  Angle = 360
  AttacherType = Attacher::AttachEngine3D
  Height = 100
  Placement = pos=(-39,-21,0) rot=(0,0,1;0rad)
  Radius = 1.5
FEATURE [Part::Cylinder] Cylinder2213  label="Válec2213"
  Angle = 360
  AttacherType = Attacher::AttachEngine3D
  Height = 4
  Placement = pos=(-7,-34,37) rot=(1,0,0;1.5708rad)
  Radius = 3
FEATURE [Part::Box] Box525  label="Krychle525"
  AttacherType = Attacher::AttachEngine3D
  Height = 64
  Length = 6
  Placement = pos=(11,-3,-93) rot=(0,0,1;0rad)
  Width = 6
FEATURE [Part::Cylinder] Cylinder2214  label="Válec2214"
  Angle = 360
  AttacherType = Attacher::AttachEngine3D
  Height = 100
  Placement = pos=(90,0,-60) rot=(0,0,1;0rad)
  Radius = 1.5
FEATURE [Part::Cylinder] Cylinder2215  label="Válec2215"
  Angle = 360
  AttacherType = Attacher::AttachEngine3D
  Height = 3
  Placement = pos=(78,41,-42) rot=(0,0,1;0rad)
  Radius = 3
FEATURE [Part::Cylinder] Cylinder2216  label="Válec2216"
  Angle = 360
  AttacherType = Attacher::AttachEngine3D
  Height = 100
  Placement = pos=(-39,-21,0) rot=(0,0,1;0rad)
  Radius = 1.5
FEATURE [Part::Cylinder] Cylinder2217  label="Válec2217"
  Angle = 360
  AttacherType = Attacher::AttachEngine3D
  Height = 3
  Placement = pos=(78,41,-42) rot=(0,0,1;0rad)
  Radius = 3
FEATURE [Part::Box] Box526  label="Krychle526"
  AttacherType = Attacher::AttachEngine3D
  Height = 64
  Length = 6
  Placement = pos=(87,-3,-93) rot=(0,0,1;0rad)
  Width = 6
FEATURE [Part::Cylinder] Cylinder2218  label="Válec2218"
  Angle = 360
  AttacherType = Attacher::AttachEngine3D
  Height = 3
  Placement = pos=(26,41,-42) rot=(0,0,1;0rad)
  Radius = 3
FEATURE [Part::Cylinder] Cylinder2219  label="Válec2219"
  Angle = 360
  AttacherType = Attacher::AttachEngine3D
  Height = 4
  Placement = pos=(7,-34,73) rot=(1,0,0;1.5708rad)
  Radius = 3
FEATURE [Part::Cylinder] Cylinder2220  label="Válec2220"
  Angle = 360
  AttacherType = Attacher::AttachEngine3D
  Height = 50
  Placement = pos=(24,18,0) rot=(0,0,1;0rad)
  Radius = 1.5
FEATURE [Part::Cylinder] Cylinder2221  label="Válec2221"
  Angle = 360
  AttacherType = Attacher::AttachEngine3D
  Height = 100
  Placement = pos=(14,0,-60) rot=(0,0,1;0rad)
  Radius = 1.5
FEATURE [Part::Cylinder] Cylinder2222  label="Válec2222"
  Angle = 360
  AttacherType = Attacher::AttachEngine3D
  Height = 100
  Placement = pos=(14,0,-60) rot=(0,0,1;0rad)
  Radius = 1.5
FEATURE [Part::Cylinder] Cylinder2223  label="Válec2223"
  Angle = 360
  AttacherType = Attacher::AttachEngine3D
  Height = 32
  Placement = pos=(26,41,-42) rot=(0,0,1;0rad)
  Radius = 1.5
FEATURE [Part::Cylinder] Cylinder2224  label="Válec2224"
  Angle = 360
  AttacherType = Attacher::AttachEngine3D
  Height = 50
  Placement = pos=(-24,18,0) rot=(0,0,1;0rad)
  Radius = 1.5
FEATURE [Part::Cylinder] Cylinder2225  label="Válec2225"
  Angle = 360
  AttacherType = Attacher::AttachEngine3D
  Height = 32
  Placement = pos=(78,41,-42) rot=(0,0,1;0rad)
  Radius = 1.5
FEATURE [Part::Cylinder] Cylinder2226  label="Válec2226"
  Angle = 360
  AttacherType = Attacher::AttachEngine3D
  Height = 32
  Placement = pos=(78,41,-42) rot=(0,0,1;0rad)
  Radius = 1.5
FEATURE [Part::Cylinder] Cylinder2227  label="Válec2227"
  Angle = 360
  AttacherType = Attacher::AttachEngine3D
  Height = 50
  Placement = pos=(-51,6,0) rot=(0,0,1;0rad)
  Radius = 1.5
FEATURE [Part::Cylinder] Cylinder2228  label="Válec2228"
  Angle = 360
  AttacherType = Attacher::AttachEngine3D
  Height = 100
  Placement = pos=(14,0,-60) rot=(0,0,1;0rad)
  Radius = 1.5
FEATURE [Part::Cylinder] Cylinder2229  label="Válec2229"
  Angle = 360
  AttacherType = Attacher::AttachEngine3D
  Height = 50
  Placement = pos=(51,6,0) rot=(0,0,1;0rad)
  Radius = 1.5
FEATURE [Part::Cylinder] Cylinder2230  label="Válec2230"
  Angle = 360
  AttacherType = Attacher::AttachEngine3D
  Height = 100
  Placement = pos=(-51,-12,0) rot=(0,0,1;0rad)
  Radius = 1.5
FEATURE [Part::Box] Box527  label="Krychle527"
  AttacherType = Attacher::AttachEngine3D
  Height = 64
  Length = 6
  Placement = pos=(87,-3,-93) rot=(0,0,1;0rad)
  Width = 6
FEATURE [Part::Cylinder] Cylinder2231  label="Válec2231"
  Angle = 360
  AttacherType = Attacher::AttachEngine3D
  Height = 100
  Placement = pos=(90,0,-60) rot=(0,0,1;0rad)
  Radius = 1.5
FEATURE [Part::Cylinder] Cylinder2232  label="Válec2232"
  Angle = 360
  AttacherType = Attacher::AttachEngine3D
  Height = 100
  Placement = pos=(39,-21,0) rot=(0,0,1;0rad)
  Radius = 1.5
FEATURE [Part::Cylinder] Cylinder2233  label="Válec2233"
  Angle = 360
  AttacherType = Attacher::AttachEngine3D
  Height = 3
  Placement = pos=(26,41,-42) rot=(0,0,1;0rad)
  Radius = 3
FEATURE [Part::Cylinder] Cylinder2234  label="Válec2234"
  Angle = 360
  AttacherType = Attacher::AttachEngine3D
  Height = 3
  Placement = pos=(78,41,-42) rot=(0,0,1;0rad)
  Radius = 3
FEATURE [Part::Cylinder] Cylinder2235  label="Válec2235"
  Angle = 360
  AttacherType = Attacher::AttachEngine3D
  Height = 32
  Placement = pos=(78,41,-42) rot=(0,0,1;0rad)
  Radius = 1.5
FEATURE [Part::Cylinder] Cylinder2236  label="Válec2236"
  Angle = 360
  AttacherType = Attacher::AttachEngine3D
  Height = 100
  Placement = pos=(-39,-21,0) rot=(0,0,1;0rad)
  Radius = 1.5
FEATURE [Part::Cylinder] Cylinder2237  label="Válec2237"
  Angle = 360
  AttacherType = Attacher::AttachEngine3D
  Height = 100
  Placement = pos=(90,0,-60) rot=(0,0,1;0rad)
  Radius = 1.5
FEATURE [Part::Cylinder] Cylinder2238  label="Válec2238"
  Angle = 360
  AttacherType = Attacher::AttachEngine3D
  Height = 32
  Placement = pos=(26,41,-42) rot=(0,0,1;0rad)
  Radius = 1.5
FEATURE [Part::Cylinder] Cylinder2239  label="Válec2239"
  Angle = 360
  AttacherType = Attacher::AttachEngine3D
  Height = 32
  Placement = pos=(26,41,-42) rot=(0,0,1;0rad)
  Radius = 1.5
FEATURE [Part::Cylinder] Cylinder2240  label="Válec2240"
  Angle = 360
  AttacherType = Attacher::AttachEngine3D
  Height = 100
  Placement = pos=(90,0,-60) rot=(0,0,1;0rad)
  Radius = 1.5
FEATURE [Part::Box] Box528  label="Krychle528"
  AttacherType = Attacher::AttachEngine3D
  Height = 64
  Length = 6
  Placement = pos=(11,-3,-93) rot=(0,0,1;0rad)
  Width = 6
FEATURE [Part::Box] Box529  label="Krychle529"
  AttacherType = Attacher::AttachEngine3D
  Height = 64
  Length = 6
  Placement = pos=(87,-3,-93) rot=(0,0,1;0rad)
  Width = 6
FEATURE [Part::Cylinder] Cylinder2241  label="Válec2241"
  Angle = 360
  AttacherType = Attacher::AttachEngine3D
  Height = 58
  Placement = pos=(0,19,-53) rot=(1,0,0;1.5708rad)
  Radius = 60.2
FEATURE [Part::Cylinder] Cylinder2242  label="Válec2242"
  Angle = 360
  AttacherType = Attacher::AttachEngine3D
  Height = 58
  Placement = pos=(0,19,-53) rot=(1,0,0;1.5708rad)
  Radius = 60.2
FEATURE [Part::Box] Box530  label="Krychle530"
  AttacherType = Attacher::AttachEngine3D
  Height = 64
  Length = 6
  Placement = pos=(11,-3,-93) rot=(0,0,1;0rad)
  Width = 6
FEATURE [PartDesign::Body] Body003
  Group = -> [Sketch005,Pad003]
  Origin = -> Origin003
  Tip = -> Pad003
FEATURE [Part::Compound] Compound903
  Links = -> [Box521,Box522]
FEATURE [Part::Compound] Compound904
  Links = -> [Cylinder2192,Cylinder2204,Cylinder2191,Cylinder2193]
  Placement = pos=(0,141,45) rot=(1,0,0;1.5708rad)
FEATURE [Part::Compound] Compound906
  Links = -> [Cylinder2185,Cylinder2213,Cylinder2219,Cylinder2205]
  Placement = pos=(0,160,45) rot=(1,0,0;1.5708rad)
FEATURE [Part::Compound] Compound907
  Links = -> [Cylinder2230,Cylinder2210]
FEATURE [Part::Compound] Compound908
  Links = -> [Cylinder2197,Cylinder2208,Cylinder2200,Cylinder2189]
  Placement = pos=(0,6,0) rot=(0,0,1;0rad)
FEATURE [Part::Compound] Compound909
  Links = -> [Cylinder2209,Cylinder2188,Cylinder2198,Cylinder2194]
  Placement = pos=(0,141,45) rot=(1,0,0;1.5708rad)
FEATURE [Part::Cut] Cut527
  Base = -> Cylinder2190
  Tool = -> Compound909
FEATURE [Part::Cut] Cut524
  Base = -> Cut527
  Placement = pos=(0,19,0) rot=(0,0,1;0rad)
  Tool = -> Compound904
FEATURE [Part::Compound] Compound910
  Links = -> [Cylinder2212,Cylinder2203]
  Placement = pos=(0,-6,0) rot=(0,0,1;0rad)
FEATURE [Part::Compound] Compound911
  Links = -> [Cylinder2211,Cylinder2226]
  Placement = pos=(-52,0,36) rot=(0,0,1;0rad)
FEATURE [Part::Compound] Compound912
  Links = -> [Cylinder2199,Cylinder2217]
  Placement = pos=(-52,0,42) rot=(0,0,1;0rad)
FEATURE [Part::Compound] Compound913  label="srouby_troj011"
  Links = -> [Cylinder2214,Cylinder2201]
  Placement = pos=(-52,0,0) rot=(0,0,1;0rad)
FEATURE [Part::Compound] Compound914
  Links = -> [Cylinder2196,Cylinder2187,Cylinder2195,Cylinder2202]
  Placement = pos=(0,160,45) rot=(1,0,0;1.5708rad)
FEATURE [Part::Cut] Cut530
  Base = -> Body003
  Tool = -> Compound914
FEATURE [Part::Cut] Cut526
  Base = -> Cut530
  Tool = -> Compound906
FEATURE [Part::Compound] Compound915
  Links = -> [Box525,Box526]
  Placement = pos=(-52,0,36) rot=(0,0,1;0rad)
FEATURE [Part::Compound] Compound917
  Links = -> [Box530,Box529]
  Placement = pos=(-52,0,36) rot=(0,0,1;0rad)
FEATURE [Part::Compound] Compound918
  Links = -> [Cylinder2223,Cylinder2225]
  Placement = pos=(-52,0,36) rot=(0,0,1;0rad)
FEATURE [Part::Compound] Compound919
  Links = -> [Cylinder2238,Cylinder2183]
  Placement = pos=(-52,0,36) rot=(0,0,1;0rad)
FEATURE [Part::Compound] Compound921
  Links = -> [Compound913,Compound911]
FEATURE [Part::Compound] Compound922  label="srouby_troj012"
  Links = -> [Cylinder2231,Cylinder2221]
  Placement = pos=(-52,0,0) rot=(0,0,1;0rad)
FEATURE [Part::Compound] Compound920
  Links = -> [Compound922,Compound919]
FEATURE [Part::Compound] Compound924
  Links = -> [Cylinder2216,Cylinder2206]
  Placement = pos=(0,-6,0) rot=(0,0,1;0rad)
FEATURE [Part::Cut] Cut521
  Base = -> Compound903
  Tool = -> Compound924
FEATURE [Part::Cut] Cut529
  Base = -> Cut521
  Tool = -> Compound920
FEATURE [Part::Compound] Compound925
  Links = -> [Cylinder2229,Cylinder2227,Cylinder2224,Cylinder2220]
  Placement = pos=(0,6,0) rot=(0,0,1;0rad)
FEATURE [Part::Compound] Compound926
  Links = -> [Box528,Box527]
  Placement = pos=(-52,0,36) rot=(0,0,1;0rad)
FEATURE [Part::Cut] Cut517
  Base = -> Cut529
  Tool = -> Compound926
FEATURE [Part::Compound] Compound927
  Links = -> [Cylinder2236,Cylinder2232]
  Placement = pos=(0,-6,0) rot=(0,0,1;0rad)
FEATURE [Part::Compound] Compound928
  Links = -> [Compound927,Compound925,Compound907]
  Placement = pos=(0,0,-10) rot=(0,0,1;0rad)
FEATURE [Part::Cut] Cut531
  Base = -> Cut515
  Tool = -> Compound928
FEATURE [Part::Compound] Compound929
  Links = -> [Cylinder2207,Cylinder2186]
FEATURE [Part::Compound] Compound905
  Links = -> [Compound910,Compound908,Compound929]
  Placement = pos=(0,0,-10) rot=(0,0,1;0rad)
FEATURE [Part::Cut] Cut522
  Base = -> Box524
  Tool = -> Compound905
FEATURE [Part::Compound] Compound930
  Links = -> [Cylinder2218,Cylinder2215]
  Placement = pos=(-52,0,42) rot=(0,0,1;0rad)
FEATURE [Part::Cut] Cut516
  Base = -> Cut522
  Tool = -> Compound930
FEATURE [Part::Cut] Cut513
  Base = -> Cut516
  Tool = -> Compound921
FEATURE [Part::Cut] Cut519
  Base = -> Cut513
  Tool = -> Cylinder2242
FEATURE [Part::Cut] Cut523
  Base = -> Cut519
  Tool = -> Compound917
FEATURE [Part::Compound] Compound931
  Links = -> [Cylinder2239,Cylinder2235]
  Placement = pos=(-52,0,36) rot=(0,0,1;0rad)
FEATURE [Part::Compound] Compound932  label="srouby_troj013"
  Links = -> [Cylinder2237,Cylinder2222]
  Placement = pos=(-52,0,0) rot=(0,0,1;0rad)
FEATURE [Part::Compound] Compound916
  Links = -> [Compound932,Compound918]
FEATURE [Part::Cut] Cut525
  Base = -> Cut531
  Tool = -> Compound916
FEATURE [Part::Cut] Cut518
  Base = -> Cut525
  Tool = -> Compound912
FEATURE [Part::Cut] Cut532
  Base = -> Cut518
  Tool = -> Compound915
FEATURE [Part::Cut] Cut514
  Base = -> Cut532
  Tool = -> Cylinder2241
FEATURE [Part::Compound] Compound933  label="srouby_troj014"
  Links = -> [Cylinder2240,Cylinder2228]
  Placement = pos=(-52,0,0) rot=(0,0,1;0rad)
FEATURE [Part::Compound] Compound934
  Links = -> [Cylinder2233,Cylinder2234]
  Placement = pos=(-52,0,42) rot=(0,0,1;0rad)
FEATURE [Part::Cut] Cut528
  Base = -> Cut526
  Tool = -> Compound934
FEATURE [Part::Compound] Compound935
  Links = -> [Compound933,Compound931]
FEATURE [Part::Cut] Cut512
  Base = -> Cut528
  Tool = -> Compound935
FEATURE [Part::Compound] Compound923  label="Base_deep-triangle001"
  Links = -> [Cut514,Cut523,Cut512,Cut517,Cut524]
  Placement = pos=(52,0,-36) rot=(0,0,1;3.14159rad)
FEATURE [Part::Cut] Cut520
  Base = -> Compound923
  Tool = -> Cylinder2184
FEATURE [Part::Fillet] Fillet
  Base = -> Cut520
  Edges = 1 edges r=8: [Edge47]
FEATURE [Part::Fillet] Fillet042  label="Base_deep-triangle-holed"
  Base = -> Fillet
  Edges = 1 edges r=8: [Edge39]
FEATURE [Part::FeaturePython] Tube093  # WARN: FeaturePython — macro-defined, semantics opaque (R4)
  AttacherType = Attacher::AttachEngine3D
  Height = 25
  InnerRadius = 53
  OuterRadius = 60
  Placement = pos=(0,0,20) rot=(0,0,1;0rad)
FEATURE [Part::FeaturePython] Tube094  label="ZKL-6818-higher"  # WARN: FeaturePython — macro-defined, semantics opaque (R4)
  AttacherType = Attacher::AttachEngine3D
  Height = 14
  InnerRadius = 45
  OuterRadius = 57.5
  Placement = pos=(0,0,20) rot=(0,0,1;0rad)
FEATURE [Part::Cut] Cut533
  Base = -> Tube093
  Tool = -> Tube094
FEATURE [Part::Box] Box458  label="Krychle458"
  AttacherType = Attacher::AttachEngine3D
  Height = 25
  Length = 4
  Placement = pos=(59,-7,20) rot=(0,0,1;0rad)
  Width = 14
FEATURE [Part::Chamfer] Chamfer040
  Base = -> Box458
  Edges = 2 edges r=3: [Edge5,Edge7]
FEATURE [Part::Chamfer] Chamfer001
  Base = -> Box458
  Edges = 2 edges r=3: [Edge5,Edge7]
  Placement = pos=(0,0,0) rot=(0,0,1;0.785398rad)
FEATURE [Part::Chamfer] Chamfer002
  Base = -> Box458
  Edges = 2 edges r=3: [Edge5,Edge7]
  Placement = pos=(0,0,0) rot=(0,0,1;1.5708rad)
FEATURE [Part::Chamfer] Chamfer003
  Base = -> Box458
  Edges = 2 edges r=3: [Edge5,Edge7]
  Placement = pos=(0,0,0) rot=(0,0,1;2.35619rad)
FEATURE [Part::Chamfer] Chamfer004
  Base = -> Box458
  Edges = 2 edges r=3: [Edge5,Edge7]
  Placement = pos=(0,0,0) rot=(0,0,1;3.14159rad)
FEATURE [Part::Chamfer] Chamfer005
  Base = -> Box458
  Edges = 2 edges r=3: [Edge5,Edge7]
  Placement = pos=(0,0,0) rot=(0,0,1;3.92699rad)
FEATURE [Part::Chamfer] Chamfer006
  Base = -> Box458
  Edges = 2 edges r=3: [Edge5,Edge7]
  Placement = pos=(0,0,0) rot=(0,0,-1;1.5708rad)
FEATURE [Part::Chamfer] Chamfer007
  Base = -> Box458
  Edges = 2 edges r=3: [Edge5,Edge7]
  Placement = pos=(0,0,0) rot=(0,0,-1;0.785398rad)
FEATURE [Part::Compound] Compound861
  Links = -> [Chamfer001,Chamfer002,Chamfer003,Chamfer004,Chamfer005,Chamfer006,Chamfer007,Chamfer040]
FEATURE [Part::Cylinder] Cylinder2243  label="Válec2243"
  Angle = 360
  AttacherType = Attacher::AttachEngine3D
  Height = 40
  Placement = pos=(60,0,3) rot=(0,0,1;0rad)
  Radius = 1.5
FEATURE [Part::Cylinder] Cylinder2244  label="Válec2244"
  Angle = 360
  AttacherType = Attacher::AttachEngine3D
  Height = 40
  Placement = pos=(42.4264,42.4264,3) rot=(0,0,1;0.785398rad)
  Radius = 1.5
FEATURE [Part::Cylinder] Cylinder2245  label="Válec2245"
  Angle = 360
  AttacherType = Attacher::AttachEngine3D
  Height = 40
  Placement = pos=(-7e-15,60,3) rot=(0,0,1;1.5708rad)
  Radius = 1.5
FEATURE [Part::Cylinder] Cylinder2246  label="Válec2246"
  Angle = 360
  AttacherType = Attacher::AttachEngine3D
  Height = 40
  Placement = pos=(-42.4264,42.4264,3) rot=(0,0,1;2.35619rad)
  Radius = 1.5
FEATURE [Part::Cylinder] Cylinder2247  label="Válec2247"
  Angle = 360
  AttacherType = Attacher::AttachEngine3D
  Height = 40
  Placement = pos=(-60,-2e-14,3) rot=(0,0,1;3.14159rad)
  Radius = 1.5
FEATURE [Part::Cylinder] Cylinder2248  label="Válec2248"
  Angle = 360
  AttacherType = Attacher::AttachEngine3D
  Height = 40
  Placement = pos=(-42.4264,-42.4264,3) rot=(0,0,1;3.92699rad)
  Radius = 1.5
FEATURE [Part::Cylinder] Cylinder2249  label="Válec2249"
  Angle = 360
  AttacherType = Attacher::AttachEngine3D
  Height = 40
  Placement = pos=(2.8e-14,-60,3) rot=(0,0,-1;1.5708rad)
  Radius = 1.5
FEATURE [Part::Cylinder] Cylinder2250  label="Válec2250"
  Angle = 360
  AttacherType = Attacher::AttachEngine3D
  Height = 40
  Placement = pos=(42.4264,-42.4264,3) rot=(0,0,-1;0.785398rad)
  Radius = 1.5
FEATURE [Part::Compound] Compound936
  Links = -> [Cylinder2243,Cylinder2244,Cylinder2245,Cylinder2246,Cylinder2247,Cylinder2248,Cylinder2249,Cylinder2250]
FEATURE [Part::Cylinder] Cylinder2251  label="Válec2251"
  Angle = 360
  AttacherType = Attacher::AttachEngine3D
  Height = 40
  Placement = pos=(60,0,3) rot=(0,0,1;0rad)
  Radius = 1.5
FEATURE [Part::Cut] Cut472
  Base = -> Compound861
  Tool = -> Compound936
FEATURE [Part::Cylinder] Cylinder2252  label="Válec2252"
  Angle = 360
  AttacherType = Attacher::AttachEngine3D
  Height = 40
  Placement = pos=(42.4264,42.4264,3) rot=(0,0,1;0.785398rad)
  Radius = 1.5
FEATURE [Part::Cylinder] Cylinder2253  label="Válec2253"
  Angle = 360
  AttacherType = Attacher::AttachEngine3D
  Height = 40
  Placement = pos=(-7e-15,60,3) rot=(0,0,1;1.5708rad)
  Radius = 1.5
FEATURE [Part::Cylinder] Cylinder2254  label="Válec2254"
  Angle = 360
  AttacherType = Attacher::AttachEngine3D
  Height = 40
  Placement = pos=(-42.4264,42.4264,3) rot=(0,0,1;2.35619rad)
  Radius = 1.5
FEATURE [Part::Cylinder] Cylinder2255  label="Válec2255"
  Angle = 360
  AttacherType = Attacher::AttachEngine3D
  Height = 40
  Placement = pos=(-60,-2e-14,3) rot=(0,0,1;3.14159rad)
  Radius = 1.5
FEATURE [Part::Cylinder] Cylinder2256  label="Válec2256"
  Angle = 360
  AttacherType = Attacher::AttachEngine3D
  Height = 40
  Placement = pos=(-42.4264,-42.4264,3) rot=(0,0,1;3.92699rad)
  Radius = 1.5
FEATURE [Part::Cylinder] Cylinder2257  label="Válec2257"
  Angle = 360
  AttacherType = Attacher::AttachEngine3D
  Height = 40
  Placement = pos=(2.8e-14,-60,3) rot=(0,0,-1;1.5708rad)
  Radius = 1.5
FEATURE [Part::Cylinder] Cylinder2258  label="Válec2258"
  Angle = 360
  AttacherType = Attacher::AttachEngine3D
  Height = 40
  Placement = pos=(42.4264,-42.4264,3) rot=(0,0,-1;0.785398rad)
  Radius = 1.5
FEATURE [Part::Compound] Compound937
  Links = -> [Cylinder2251,Cylinder2252,Cylinder2253,Cylinder2254,Cylinder2255,Cylinder2256,Cylinder2257,Cylinder2258]
FEATURE [Part::Cut] Cut473
  Base = -> Cut533
  Tool = -> Compound937
FEATURE [Part::Box] Box531  label="Krychle531"
  AttacherType = Attacher::AttachEngine3D
  Height = 2
  Length = 10
  Placement = pos=(53,-3,37) rot=(0,0,1;0rad)
  Width = 6
FEATURE [Part::Box] Box532  label="Krychle532"
  AttacherType = Attacher::AttachEngine3D
  Height = 2
  Length = 10
  Placement = pos=(39.598,35.3553,37) rot=(0,0,1;0.785398rad)
  Width = 6
FEATURE [Part::Box] Box533  label="Krychle533"
  AttacherType = Attacher::AttachEngine3D
  Height = 2
  Length = 10
  Placement = pos=(3,53,37) rot=(0,0,1;1.5708rad)
  Width = 6
FEATURE [Part::Box] Box534  label="Krychle534"
  AttacherType = Attacher::AttachEngine3D
  Height = 2
  Length = 10
  Placement = pos=(-35.3553,39.598,37) rot=(0,0,1;2.35619rad)
  Width = 6
FEATURE [Part::Box] Box535  label="Krychle535"
  AttacherType = Attacher::AttachEngine3D
  Height = 2
  Length = 10
  Placement = pos=(-53,3,37) rot=(0,0,1;3.14159rad)
  Width = 6
FEATURE [Part::Box] Box536  label="Krychle536"
  AttacherType = Attacher::AttachEngine3D
  Height = 2
  Length = 10
  Placement = pos=(-39.598,-35.3553,37) rot=(0,0,1;3.92699rad)
  Width = 6
FEATURE [Part::Box] Box537  label="Krychle537"
  AttacherType = Attacher::AttachEngine3D
  Height = 2
  Length = 10
  Placement = pos=(-3,-53,37) rot=(0,0,-1;1.5708rad)
  Width = 6
FEATURE [Part::Box] Box538  label="Krychle538"
  AttacherType = Attacher::AttachEngine3D
  Height = 2
  Length = 10
  Placement = pos=(35.3553,-39.598,37) rot=(0,0,-1;0.785398rad)
  Width = 6
FEATURE [Part::Compound] Compound938
  Links = -> [Box532,Box533,Box534,Box535,Box536,Box537,Box538,Box531]
FEATURE [Part::Cut] Cut474
  Base = -> Cut472
  Tool = -> Compound938
FEATURE [Part::Box] Box539  label="Krychle539"
  AttacherType = Attacher::AttachEngine3D
  Height = 2
  Length = 10
  Placement = pos=(53,-3,37) rot=(0,0,1;0rad)
  Width = 6
FEATURE [Part::Box] Box540  label="Krychle540"
  AttacherType = Attacher::AttachEngine3D
  Height = 2
  Length = 10
  Placement = pos=(39.598,35.3553,37) rot=(0,0,1;0.785398rad)
  Width = 6
FEATURE [Part::Box] Box541  label="Krychle541"
  AttacherType = Attacher::AttachEngine3D
  Height = 2
  Length = 10
  Placement = pos=(3,53,37) rot=(0,0,1;1.5708rad)
  Width = 6
FEATURE [Part::Box] Box542  label="Krychle542"
  AttacherType = Attacher::AttachEngine3D
  Height = 2
  Length = 10
  Placement = pos=(-35.3553,39.598,37) rot=(0,0,1;2.35619rad)
  Width = 6
FEATURE [Part::Box] Box543  label="Krychle543"
  AttacherType = Attacher::AttachEngine3D
  Height = 2
  Length = 10
  Placement = pos=(-53,3,37) rot=(0,0,1;3.14159rad)
  Width = 6
FEATURE [Part::Box] Box544  label="Krychle544"
  AttacherType = Attacher::AttachEngine3D
  Height = 2
  Length = 10
  Placement = pos=(-39.598,-35.3553,37) rot=(0,0,1;3.92699rad)
  Width = 6
FEATURE [Part::Box] Box545  label="Krychle545"
  AttacherType = Attacher::AttachEngine3D
  Height = 2
  Length = 10
  Placement = pos=(-3,-53,37) rot=(0,0,-1;1.5708rad)
  Width = 6
FEATURE [Part::Box] Box546  label="Krychle546"
  AttacherType = Attacher::AttachEngine3D
  Height = 2
  Length = 10
  Placement = pos=(35.3553,-39.598,37) rot=(0,0,-1;0.785398rad)
  Width = 6
FEATURE [Part::Compound] Compound939
  Links = -> [Box540,Box541,Box542,Box543,Box544,Box545,Box546,Box539]
FEATURE [Part::Cut] Cut475
  Base = -> Cut473
  Tool = -> Compound939
FEATURE [Part::Box] Box547  label="Krychle547"
  AttacherType = Attacher::AttachEngine3D
  Height = 6
  Length = 6
  Placement = pos=(48,-45,35) rot=(0,0,1;0rad)
  Width = 2
FEATURE [Part::Box] Box548  label="Krychle548"
  AttacherType = Attacher::AttachEngine3D
  Height = 6
  Length = 6
  Placement = pos=(-54,-45,35) rot=(0,0,1;0rad)
  Width = 2
FEATURE [Part::Compound] Compound943
  Links = -> [Box547,Box548]
  Placement = pos=(0,0,-11) rot=(0,0,1;0rad)
FEATURE [Part::Cylinder] Cylinder2259  label="Válec2259"
  Angle = 360
  AttacherType = Attacher::AttachEngine3D
  Height = 40
  Placement = pos=(-51,-40,38) rot=(1,0,0;1.5708rad)
  Radius = 1.5
FEATURE [Part::Cylinder] Cylinder2260  label="Válec2260"
  Angle = 360
  AttacherType = Attacher::AttachEngine3D
  Height = 40
  Placement = pos=(51,-40,38) rot=(1,0,0;1.5708rad)
  Radius = 1.5
FEATURE [Part::Compound] Compound942
  Links = -> [Cylinder2259,Cylinder2260]
  Placement = pos=(0,8,-11) rot=(0,0,1;0rad)
FEATURE [Part::Cylinder] Cylinder2261  label="Válec2261"
  Angle = 360
  AttacherType = Attacher::AttachEngine3D
  Height = 25
  Placement = pos=(0,0,20) rot=(0,0,1;0rad)
  Radius = 60
FEATURE [Part::Box] Box549  label="Krychle549"
  AttacherType = Attacher::AttachEngine3D
  Height = 25
  Length = 108
  Placement = pos=(-54,-53,20) rot=(0,0,1;0rad)
  Width = 46
FEATURE [Part::Cut] Cut538
  Base = -> Box549
  Tool = -> Cylinder2261
FEATURE [Part::Cut] Cut534
  Base = -> Cut538
  Tool = -> Compound942
FEATURE [Part::Cut] Cut537
  Base = -> Cut534
  Placement = pos=(0,0,12) rot=(0,0,1;0rad)
  Tool = -> Compound943
FEATURE [Part::Cylinder] Cylinder2262  label="Válec2262"
  Angle = 360
  AttacherType = Attacher::AttachEngine3D
  Height = 40
  Placement = pos=(0,-17,27) rot=(1,0,0;1.5708rad)
  Radius = 59
FEATURE [Part::Common] Common003
  Base = -> Cut537
  Tool = -> Cylinder2262
FEATURE [Part::Box] Box550  label="Krychle550"
  AttacherType = Attacher::AttachEngine3D
  Height = 6
  Length = 6
  Placement = pos=(36,-47,56) rot=(0,0,1;0rad)
  Width = 2
FEATURE [Part::Cylinder] Cylinder2263  label="Válec2263"
  Angle = 360
  AttacherType = Attacher::AttachEngine3D
  Height = 40
  Placement = pos=(39,-40,59) rot=(1,0,0;1.5708rad)
  Radius = 1.5
FEATURE [Part::Cylinder] Cylinder2264  label="Válec2264"
  Angle = 360
  AttacherType = Attacher::AttachEngine3D
  Height = 40
  Placement = pos=(-39,-40,59) rot=(1,0,0;1.5708rad)
  Radius = 1.5
FEATURE [Part::Compound] Compound940
  Links = -> [Cylinder2263,Cylinder2264]
  Placement = pos=(0,0,-5) rot=(0,0,1;0rad)
FEATURE [Part::Box] Box551  label="Krychle551"
  AttacherType = Attacher::AttachEngine3D
  Height = 6
  Length = 6
  Placement = pos=(-42,-47,56) rot=(0,0,1;0rad)
  Width = 2
FEATURE [Part::Compound] Compound941
  Links = -> [Box551,Box550]
  Placement = pos=(0,0,-5) rot=(0,0,1;0rad)
FEATURE [Part::Cut] Cut536
  Base = -> Common003
  Tool = -> Compound941
FEATURE [Part::Cut] Cut535
  Base = -> Cut536
  Placement = pos=(0,0,-12) rot=(0,0,1;0rad)
  Tool = -> Compound940
FEATURE [Part::Box] Box552  label="Krychle552"
  AttacherType = Attacher::AttachEngine3D
  Height = 6
  Length = 6
  Placement = pos=(36,-47,56) rot=(0,0,1;0rad)
  Width = 2
FEATURE [Part::Box] Box553  label="Krychle553"
  AttacherType = Attacher::AttachEngine3D
  Height = 6
  Length = 6
  Placement = pos=(-42,-47,56) rot=(0,0,1;0rad)
  Width = 2
FEATURE [Part::Cylinder] Cylinder2265  label="Válec2265"
  Angle = 360
  AttacherType = Attacher::AttachEngine3D
  Height = 40
  Placement = pos=(39,-40,59) rot=(1,0,0;1.5708rad)
  Radius = 1.5
FEATURE [Part::Cylinder] Cylinder2266  label="Válec2266"
  Angle = 360
  AttacherType = Attacher::AttachEngine3D
  Height = 40
  Placement = pos=(-39,-40,59) rot=(1,0,0;1.5708rad)
  Radius = 1.5
FEATURE [Part::Box] Box554  label="Krychle554"
  AttacherType = Attacher::AttachEngine3D
  Height = 2
  Length = 10
  Placement = pos=(53,-3,37) rot=(0,0,1;0rad)
  Width = 6
FEATURE [Part::Box] Box555  label="Krychle555"
  AttacherType = Attacher::AttachEngine3D
  Height = 2
  Length = 10
  Placement = pos=(39.598,35.3553,37) rot=(0,0,1;0.785398rad)
  Width = 6
FEATURE [Part::Box] Box556  label="Krychle556"
  AttacherType = Attacher::AttachEngine3D
  Height = 2
  Length = 10
  Placement = pos=(3,53,37) rot=(0,0,1;1.5708rad)
  Width = 6
FEATURE [Part::Box] Box557  label="Krychle557"
  AttacherType = Attacher::AttachEngine3D
  Height = 2
  Length = 10
  Placement = pos=(-35.3553,39.598,37) rot=(0,0,1;2.35619rad)
  Width = 6
FEATURE [Part::Box] Box558  label="Krychle558"
  AttacherType = Attacher::AttachEngine3D
  Height = 2
  Length = 10
  Placement = pos=(-53,3,37) rot=(0,0,1;3.14159rad)
  Width = 6
FEATURE [Part::Box] Box559  label="Krychle559"
  AttacherType = Attacher::AttachEngine3D
  Height = 2
  Length = 10
  Placement = pos=(-39.598,-35.3553,37) rot=(0,0,1;3.92699rad)
  Width = 6
FEATURE [Part::Box] Box560  label="Krychle560"
  AttacherType = Attacher::AttachEngine3D
  Height = 2
  Length = 10
  Placement = pos=(-3,-53,37) rot=(0,0,-1;1.5708rad)
  Width = 6
FEATURE [Part::Box] Box561  label="Krychle561"
  AttacherType = Attacher::AttachEngine3D
  Height = 2
  Length = 10
  Placement = pos=(35.3553,-39.598,37) rot=(0,0,-1;0.785398rad)
  Width = 6
FEATURE [Part::Cylinder] Cylinder2267  label="Válec2267"
  Angle = 360
  AttacherType = Attacher::AttachEngine3D
  Height = 40
  Placement = pos=(60,0,3) rot=(0,0,1;0rad)
  Radius = 1.5
FEATURE [Part::Compound] Compound944
  Links = -> [Box553,Box552]
  Placement = pos=(0,0,-17) rot=(0,0,1;0rad)
FEATURE [Part::Cut] Cut539
  Base = -> Cut535
  Tool = -> Compound944
FEATURE [Part::Compound] Compound945
  Links = -> [Cylinder2265,Cylinder2266]
  Placement = pos=(0,0,-17) rot=(0,0,1;0rad)
FEATURE [Part::Compound] Compound946
  Links = -> [Box555,Box556,Box557,Box558,Box559,Box560,Box561,Box554]
FEATURE [Part::Cut] Cut540
  Base = -> Cut539
  Tool = -> Compound945
FEATURE [Part::Cut] Cut488
  Base = -> Cut540
  Tool = -> Compound946
FEATURE [Part::Cylinder] Cylinder2268  label="Válec2268"
  Angle = 360
  AttacherType = Attacher::AttachEngine3D
  Height = 40
  Placement = pos=(42.4264,42.4264,3) rot=(0,0,1;0.785398rad)
  Radius = 1.5
FEATURE [Part::Cylinder] Cylinder2269  label="Válec2269"
  Angle = 360
  AttacherType = Attacher::AttachEngine3D
  Height = 40
  Placement = pos=(-7e-15,60,3) rot=(0,0,1;1.5708rad)
  Radius = 1.5
FEATURE [Part::Cylinder] Cylinder2270  label="Válec2270"
  Angle = 360
  AttacherType = Attacher::AttachEngine3D
  Height = 40
  Placement = pos=(-42.4264,42.4264,3) rot=(0,0,1;2.35619rad)
  Radius = 1.5
FEATURE [Part::Cylinder] Cylinder2271  label="Válec2271"
  Angle = 360
  AttacherType = Attacher::AttachEngine3D
  Height = 40
  Placement = pos=(-60,-2e-14,3) rot=(0,0,1;3.14159rad)
  Radius = 1.5
FEATURE [Part::Cylinder] Cylinder2272  label="Válec2272"
  Angle = 360
  AttacherType = Attacher::AttachEngine3D
  Height = 40
  Placement = pos=(-42.4264,-42.4264,3) rot=(0,0,1;3.92699rad)
  Radius = 1.5
FEATURE [Part::Cylinder] Cylinder2273  label="Válec2273"
  Angle = 360
  AttacherType = Attacher::AttachEngine3D
  Height = 40
  Placement = pos=(2.8e-14,-60,3) rot=(0,0,-1;1.5708rad)
  Radius = 1.5
FEATURE [Part::Cylinder] Cylinder2274  label="Válec2274"
  Angle = 360
  AttacherType = Attacher::AttachEngine3D
  Height = 40
  Placement = pos=(42.4264,-42.4264,3) rot=(0,0,-1;0.785398rad)
  Radius = 1.5
FEATURE [Part::Compound] Compound947
  Links = -> [Cylinder2267,Cylinder2268,Cylinder2269,Cylinder2270,Cylinder2271,Cylinder2272,Cylinder2273,Cylinder2274]
FEATURE [Part::Cut] Cut541
  Base = -> Cut488
  Tool = -> Compound947
FEATURE [Part::Cylinder] Cylinder2275  label="Válec2275"
  Angle = 360
  AttacherType = Attacher::AttachEngine3D
  Height = 40
  Placement = pos=(39,-40,59) rot=(1,0,0;1.5708rad)
  Radius = 1.5
FEATURE [Part::Cylinder] Cylinder2276  label="Válec2276"
  Angle = 360
  AttacherType = Attacher::AttachEngine3D
  Height = 40
  Placement = pos=(-39,-40,59) rot=(1,0,0;1.5708rad)
  Radius = 1.5
FEATURE [Part::Box] Box562  label="Krychle562"
  AttacherType = Attacher::AttachEngine3D
  Height = 6
  Length = 6
  Placement = pos=(36,-47,56) rot=(0,0,1;0rad)
  Width = 2
FEATURE [Part::Box] Box563  label="Krychle563"
  AttacherType = Attacher::AttachEngine3D
  Height = 6
  Length = 6
  Placement = pos=(-42,-47,56) rot=(0,0,1;0rad)
  Width = 2
FEATURE [Part::Cylinder] Cylinder2277  label="Válec2277"
  Angle = 360
  AttacherType = Attacher::AttachEngine3D
  Height = 40
  Placement = pos=(39,-40,59) rot=(1,0,0;1.5708rad)
  Radius = 1.5
FEATURE [Part::Cylinder] Cylinder2278  label="Válec2278"
  Angle = 360
  AttacherType = Attacher::AttachEngine3D
  Height = 40
  Placement = pos=(-39,-40,59) rot=(1,0,0;1.5708rad)
  Radius = 1.5
FEATURE [Part::Box] Box564  label="Krychle564"
  AttacherType = Attacher::AttachEngine3D
  Height = 6
  Length = 6
  Placement = pos=(36,-47,56) rot=(0,0,1;0rad)
  Width = 2
FEATURE [Part::Box] Box565  label="Krychle565"
  AttacherType = Attacher::AttachEngine3D
  Height = 6
  Length = 6
  Placement = pos=(-42,-47,56) rot=(0,0,1;0rad)
  Width = 2
FEATURE [Part::Box] Box566  label="Krychle566"
  AttacherType = Attacher::AttachEngine3D
  Height = 19
  Length = 14
  Placement = pos=(-60,-43,10) rot=(0,0,1;0rad)
  Width = 43
FEATURE [Part::Compound] Compound948
  Links = -> [Cylinder2275,Cylinder2276]
  Placement = pos=(0,0,-17) rot=(0,0,1;0rad)
FEATURE [Part::Cut] Cut542
  Base = -> Cut475
  Tool = -> Compound948
FEATURE [Part::Compound] Compound949
  Links = -> [Box563,Box562]
  Placement = pos=(0,0,-17) rot=(0,0,1;0rad)
FEATURE [Part::Compound] Compound950
  Links = -> [Cylinder2277,Cylinder2278]
  Placement = pos=(0,0,-17) rot=(0,0,1;0rad)
FEATURE [Part::Compound] Compound951
  Links = -> [Box565,Box564]
  Placement = pos=(0,0,-17) rot=(0,0,1;0rad)
FEATURE [Part::Cut] Cut543
  Base = -> Cut542
  Tool = -> Compound949
FEATURE [Part::Cut] Cut544
  Base = -> Cut474
  Tool = -> Compound950
FEATURE [Part::Cut] Cut545
  Base = -> Cut544
  Tool = -> Compound951
FEATURE [Part::Box] Box567  label="Krychle567"
  AttacherType = Attacher::AttachEngine3D
  Height = 19
  Length = 14
  Placement = pos=(46,-43,10) rot=(0,0,1;0rad)
  Width = 43
FEATURE [Part::Compound] Compound952
  Links = -> [Box566,Box567]
  Placement = pos=(0,0,10) rot=(0,0,1;0rad)
FEATURE [Part::Cylinder] Cylinder2279  label="Válec2279"
  Angle = 360
  AttacherType = Attacher::AttachEngine3D
  Height = 33
  Placement = pos=(60,-43,10) rot=(0,0,1;0rad)
  Radius = 6
FEATURE [Part::Cylinder] Cylinder2280  label="Válec2280"
  Angle = 360
  AttacherType = Attacher::AttachEngine3D
  Height = 33
  Placement = pos=(-60,-43,10) rot=(0,0,1;0rad)
  Radius = 6
FEATURE [Part::Compound] Compound953
  Links = -> [Cylinder2279,Cylinder2280]
  Placement = pos=(0,0,6) rot=(0,0,1;0rad)
FEATURE [Part::Cylinder] Cylinder2281  label="Válec2281"
  Angle = 360
  AttacherType = Attacher::AttachEngine3D
  Height = 33
  Placement = pos=(0,0,20) rot=(0,0,1;0rad)
  Radius = 60
FEATURE [Part::Cylinder] Cylinder2282  label="Válec2282"
  Angle = 360
  AttacherType = Attacher::AttachEngine3D
  Height = 40
  Placement = pos=(60,0,3) rot=(0,0,1;0rad)
  Radius = 1.5
FEATURE [Part::Cylinder] Cylinder2283  label="Válec2283"
  Angle = 360
  AttacherType = Attacher::AttachEngine3D
  Height = 40
  Placement = pos=(42.4264,42.4264,3) rot=(0,0,1;0.785398rad)
  Radius = 1.5
FEATURE [Part::Cylinder] Cylinder2284  label="Válec2284"
  Angle = 360
  AttacherType = Attacher::AttachEngine3D
  Height = 40
  Placement = pos=(-7e-15,60,3) rot=(0,0,1;1.5708rad)
  Radius = 1.5
FEATURE [Part::Cylinder] Cylinder2285  label="Válec2285"
  Angle = 360
  AttacherType = Attacher::AttachEngine3D
  Height = 40
  Placement = pos=(-42.4264,42.4264,3) rot=(0,0,1;2.35619rad)
  Radius = 1.5
FEATURE [Part::Cylinder] Cylinder2286  label="Válec2286"
  Angle = 360
  AttacherType = Attacher::AttachEngine3D
  Height = 40
  Placement = pos=(-60,-2e-14,3) rot=(0,0,1;3.14159rad)
  Radius = 1.5
FEATURE [Part::Cylinder] Cylinder2287  label="Válec2287"
  Angle = 360
  AttacherType = Attacher::AttachEngine3D
  Height = 40
  Placement = pos=(-42.4264,-42.4264,3) rot=(0,0,1;3.92699rad)
  Radius = 1.5
FEATURE [Part::Cylinder] Cylinder2288  label="Válec2288"
  Angle = 360
  AttacherType = Attacher::AttachEngine3D
  Height = 40
  Placement = pos=(2.8e-14,-60,3) rot=(0,0,-1;1.5708rad)
  Radius = 1.5
FEATURE [Part::Cylinder] Cylinder2289  label="Válec2289"
  Angle = 360
  AttacherType = Attacher::AttachEngine3D
  Height = 40
  Placement = pos=(42.4264,-42.4264,3) rot=(0,0,-1;0.785398rad)
  Radius = 1.5
FEATURE [Part::Compound] Compound954
  Links = -> [Cylinder2282,Cylinder2283,Cylinder2284,Cylinder2285,Cylinder2286,Cylinder2287,Cylinder2288,Cylinder2289]
FEATURE [Part::Box] Box568  label="Krychle568"
  AttacherType = Attacher::AttachEngine3D
  Height = 2
  Length = 10
  Placement = pos=(53,-3,37) rot=(0,0,1;0rad)
  Width = 6
FEATURE [Part::Box] Box569  label="Krychle569"
  AttacherType = Attacher::AttachEngine3D
  Height = 2
  Length = 10
  Placement = pos=(39.598,35.3553,37) rot=(0,0,1;0.785398rad)
  Width = 6
FEATURE [Part::Box] Box570  label="Krychle570"
  AttacherType = Attacher::AttachEngine3D
  Height = 2
  Length = 10
  Placement = pos=(3,53,37) rot=(0,0,1;1.5708rad)
  Width = 6
FEATURE [Part::Box] Box571  label="Krychle571"
  AttacherType = Attacher::AttachEngine3D
  Height = 2
  Length = 10
  Placement = pos=(-35.3553,39.598,37) rot=(0,0,1;2.35619rad)
  Width = 6
FEATURE [Part::Box] Box572  label="Krychle572"
  AttacherType = Attacher::AttachEngine3D
  Height = 2
  Length = 10
  Placement = pos=(-53,3,37) rot=(0,0,1;3.14159rad)
  Width = 6
FEATURE [Part::Box] Box573  label="Krychle573"
  AttacherType = Attacher::AttachEngine3D
  Height = 2
  Length = 10
  Placement = pos=(-39.598,-35.3553,37) rot=(0,0,1;3.92699rad)
  Width = 6
FEATURE [Part::Box] Box574  label="Krychle574"
  AttacherType = Attacher::AttachEngine3D
  Height = 2
  Length = 10
  Placement = pos=(-3,-53,37) rot=(0,0,-1;1.5708rad)
  Width = 6
FEATURE [Part::Box] Box575  label="Krychle575"
  AttacherType = Attacher::AttachEngine3D
  Height = 2
  Length = 10
  Placement = pos=(35.3553,-39.598,37) rot=(0,0,-1;0.785398rad)
  Width = 6
FEATURE [Part::Compound] Compound955
  Links = -> [Box569,Box570,Box571,Box572,Box573,Box574,Box575,Box568]
FEATURE [Part::Cylinder] Cylinder2290  label="Válec2290"
  Angle = 360
  AttacherType = Attacher::AttachEngine3D
  Height = 40
  Placement = pos=(-51,-40,38) rot=(1,0,0;1.5708rad)
  Radius = 1.5
FEATURE [Part::Cylinder] Cylinder2291  label="Válec2291"
  Angle = 360
  AttacherType = Attacher::AttachEngine3D
  Height = 40
  Placement = pos=(51,-40,38) rot=(1,0,0;1.5708rad)
  Radius = 1.5
FEATURE [Part::Compound] Compound956
  Links = -> [Cylinder2290,Cylinder2291]
  Placement = pos=(0,8,-11) rot=(0,0,1;0rad)
FEATURE [Part::Chamfer] Chamfer008
  Base = -> Compound952
  Edges = 1 edges r=6: [Edge2]
FEATURE [Part::Chamfer] Chamfer009
  Base = -> Chamfer008
  Edges = 1 edges r=6: [Edge21]
FEATURE [Part::Cut] Cut546
  Base = -> Chamfer009
  Tool = -> Compound953
FEATURE [Part::Fillet] Fillet043
  Base = -> Cut546
  Edges = 1 edges r=8: [Edge21]
FEATURE [Part::Fillet] Fillet044
  Base = -> Fillet043
  Edges = 1 edges r=8: [Edge24]
FEATURE [Part::Cut] Cut547
  Base = -> Fillet044
  Tool = -> Cylinder2281
FEATURE [Part::Cut] Cut548
  Base = -> Cut547
  Tool = -> Compound956
FEATURE [Part::Cut] Cut549
  Base = -> Cut548
  Tool = -> Compound955
FEATURE [Part::Cut] Cut550
  Base = -> Cut549
  Tool = -> Compound954
FEATURE [Part::Compound] Compound957  label="J-max-deep-thin_bearing-ring"
  Links = -> [Cut541,Cut543,Cut545,Cut550]
  Placement = pos=(0,15,-53) rot=(0,0.707107,-0.707107;3.14159rad)
FEATURE [Part::Box] Box576  label="Krychle576"
  AttacherType = Attacher::AttachEngine3D
  Height = 50
  Length = 4
  Placement = pos=(59,-7.5,20) rot=(0,0,1;0rad)
  Width = 15
FEATURE [Part::Chamfer] Chamfer041
  Base = -> Box576
  Edges = 2 edges r=3: [Edge5,Edge7]
  Placement = pos=(0,0,0) rot=(0,0,-1;0.785398rad)
FEATURE [Part::Chamfer] Chamfer042
  Base = -> Box576
  Edges = 2 edges r=3: [Edge5,Edge7]
  Placement = pos=(0,0,0) rot=(0,0,-1;1.5708rad)
FEATURE [Part::Chamfer] Chamfer043
  Base = -> Box576
  Edges = 2 edges r=3: [Edge5,Edge7]
  Placement = pos=(0,0,0) rot=(0,0,1;3.92699rad)
FEATURE [Part::Chamfer] Chamfer044
  Base = -> Box576
  Edges = 2 edges r=3: [Edge5,Edge7]
  Placement = pos=(0,0,0) rot=(0,0,1;3.14159rad)
FEATURE [Part::Chamfer] Chamfer045
  Base = -> Box576
  Edges = 2 edges r=3: [Edge5,Edge7]
  Placement = pos=(0,0,0) rot=(0,0,1;2.35619rad)
FEATURE [Part::Chamfer] Chamfer046
  Base = -> Box576
  Edges = 2 edges r=3: [Edge5,Edge7]
  Placement = pos=(0,0,0) rot=(0,0,1;1.5708rad)
FEATURE [Part::Chamfer] Chamfer047
  Base = -> Box576
  Edges = 2 edges r=3: [Edge5,Edge7]
  Placement = pos=(0,0,0) rot=(0,0,1;0.785398rad)
FEATURE [Part::Chamfer] Chamfer048
  Base = -> Box576
  Edges = 2 edges r=3: [Edge5,Edge7]
FEATURE [Part::Compound] Compound958
  Links = -> [Chamfer047,Chamfer046,Chamfer045,Chamfer044,Chamfer043,Chamfer042,Chamfer041,Chamfer048]
  Placement = pos=(0,-50,-53) rot=(-1,0,0;1.5708rad)
FEATURE [Sketcher::SketchObject] Sketch006
  FullyConstrained = false
  MapMode = 5
  Support = -> [XY_Plane004]
  sketch-geometry (5):
    g0: LineSegment StartX=-53.11 StartY=25.5869 StartZ=0 EndX=-9.47198 EndY=128.297 EndZ=0
    g1: LineSegment StartX=-9.47198 StartY=128.297 StartZ=0 EndX=9.50803 EndY=128.154 EndZ=0
    g2: LineSegment StartX=9.50803 StartY=128.154 StartZ=0 EndX=53.1093 EndY=25.7412 EndZ=0
    g3: LineSegment StartX=53.1093 StartY=25.7412 StartZ=0 EndX=-0.067027 EndY=50.049 EndZ=0
    g4: LineSegment StartX=-0.067027 StartY=50.049 StartZ=0 EndX=-53.11 EndY=25.5869 EndZ=0
  constraints (5):
    c: Coincident(g0,g1)
    c: Coincident(g1,g2)
    c: Coincident(g2,g3)
    c: Coincident(g3,g4)
    c: Coincident(g4,g0)
FEATURE [PartDesign::Pad] Pad004
  Direction = (1,1,1)
  Length = 10
  Length2 = 100
  Profile = -> Sketch006
  Type = 0
FEATURE [Part::Cylinder] Cylinder2292  label="Válec2292"
  Angle = 360
  AttacherType = Attacher::AttachEngine3D
  Height = 32
  Placement = pos=(78,41,-42) rot=(0,0,1;0rad)
  Radius = 1.5
FEATURE [Part::Cylinder] Cylinder2293  label="Válec2293"
  Angle = 360
  AttacherType = Attacher::AttachEngine3D
  Height = 160
  Placement = pos=(-18,0,-60) rot=(0,0,1;0rad)
  Radius = 17
FEATURE [Part::Cylinder] Cylinder2294  label="Válec2294"
  Angle = 360
  AttacherType = Attacher::AttachEngine3D
  Height = 4
  Placement = pos=(7,-34,37) rot=(1,0,0;1.5708rad)
  Radius = 3
FEATURE [Part::Cylinder] Cylinder2295  label="Válec2295"
  Angle = 360
  AttacherType = Attacher::AttachEngine3D
  Height = 100
  Placement = pos=(51,-12,0) rot=(0,0,1;0rad)
  Radius = 1.5
FEATURE [Part::Box] Box577  label="Krychle577"
  AttacherType = Attacher::AttachEngine3D
  Height = 10
  Length = 10
  Placement = pos=(32,-24,0) rot=(0,0,1;0rad)
  Width = 52
FEATURE [Part::Cylinder] Cylinder2296  label="Válec2296"
  Angle = 360
  AttacherType = Attacher::AttachEngine3D
  Height = 20
  Placement = pos=(-7,-34,37) rot=(1,0,0;1.5708rad)
  Radius = 1.5
FEATURE [Part::Cylinder] Cylinder2297  label="Válec2297"
  Angle = 360
  AttacherType = Attacher::AttachEngine3D
  Height = 20
  Placement = pos=(-7,-34,37) rot=(1,0,0;1.5708rad)
  Radius = 1.5
FEATURE [Part::FeaturePython] Tube095  # WARN: FeaturePython — macro-defined, semantics opaque (R4)
  AttacherType = Attacher::AttachEngine3D
  Height = 10
  InnerRadius = 40
  OuterRadius = 59
FEATURE [Part::Cylinder] Cylinder2298  label="Válec2298"
  Angle = 360
  AttacherType = Attacher::AttachEngine3D
  Height = 50
  Placement = pos=(24,18,0) rot=(0,0,1;0rad)
  Radius = 1.5
FEATURE [Part::Cylinder] Cylinder2299  label="Válec2299"
  Angle = 360
  AttacherType = Attacher::AttachEngine3D
  Height = 10
  Placement = pos=(0,106,0) rot=(0,0,1;0rad)
  Radius = 10
FEATURE [Part::Box] Box578  label="Krychle578"
  AttacherType = Attacher::AttachEngine3D
  Height = 10
  Length = 10
  Placement = pos=(-42,-24,0) rot=(0,0,1;0rad)
  Width = 52
FEATURE [Part::Compound] Compound959
  Links = -> [Box577,Box578]
FEATURE [Part::Box] Box579  label="Krychle579"
  AttacherType = Attacher::AttachEngine3D
  Height = 32
  Length = 200
  Placement = pos=(-100,-130,0) rot=(0,0,1;0rad)
  Width = 100
FEATURE [Part::Cut] Cut554
  Base = -> Tube095
  Tool = -> Box579
FEATURE [Part::Cylinder] Cylinder2300  label="Válec2300"
  Angle = 360
  AttacherType = Attacher::AttachEngine3D
  Height = 4
  Placement = pos=(7,-34,73) rot=(1,0,0;1.5708rad)
  Radius = 3
FEATURE [Part::Cylinder] Cylinder2301  label="Válec2301"
  Angle = 360
  AttacherType = Attacher::AttachEngine3D
  Height = 4
  Placement = pos=(7,-34,37) rot=(1,0,0;1.5708rad)
  Radius = 3
FEATURE [Part::Cylinder] Cylinder2302  label="Válec2302"
  Angle = 360
  AttacherType = Attacher::AttachEngine3D
  Height = 4
  Placement = pos=(-7,-34,73) rot=(1,0,0;1.5708rad)
  Radius = 3
FEATURE [Part::Cylinder] Cylinder2303  label="Válec2303"
  Angle = 360
  AttacherType = Attacher::AttachEngine3D
  Height = 20
  Placement = pos=(-7,-34,73) rot=(1,0,0;1.5708rad)
  Radius = 1.5
FEATURE [Part::Cylinder] Cylinder2304  label="Válec2304"
  Angle = 360
  AttacherType = Attacher::AttachEngine3D
  Height = 20
  Placement = pos=(7,-34,73) rot=(1,0,0;1.5708rad)
  Radius = 1.5
FEATURE [Part::Cylinder] Cylinder2305  label="Válec2305"
  Angle = 360
  AttacherType = Attacher::AttachEngine3D
  Height = 20
  Placement = pos=(7,-34,37) rot=(1,0,0;1.5708rad)
  Radius = 1.5
FEATURE [Part::Cylinder] Cylinder2306  label="Válec2306"
  Angle = 360
  AttacherType = Attacher::AttachEngine3D
  Height = 50
  Placement = pos=(51,6,0) rot=(0,0,1;0rad)
  Radius = 1.5
FEATURE [Part::Box] Box580  label="Krychle580"
  AttacherType = Attacher::AttachEngine3D
  Height = 10
  Length = 72
  Placement = pos=(-36,-30,0) rot=(0,0,1;0rad)
  Width = 70
FEATURE [Part::Cylinder] Cylinder2307  label="Válec2307"
  Angle = 360
  AttacherType = Attacher::AttachEngine3D
  Height = 20
  Placement = pos=(7,-34,73) rot=(1,0,0;1.5708rad)
  Radius = 1.5
FEATURE [Part::Cylinder] Cylinder2308  label="Válec2308"
  Angle = 360
  AttacherType = Attacher::AttachEngine3D
  Height = 3
  Placement = pos=(26,41,-42) rot=(0,0,1;0rad)
  Radius = 3
FEATURE [Part::Cylinder] Cylinder2309  label="Válec2309"
  Angle = 360
  AttacherType = Attacher::AttachEngine3D
  Height = 50
  Placement = pos=(-24,18,0) rot=(0,0,1;0rad)
  Radius = 1.5
FEATURE [Part::Cylinder] Cylinder2310  label="Válec2310"
  Angle = 360
  AttacherType = Attacher::AttachEngine3D
  Height = 100
  Placement = pos=(14,0,-60) rot=(0,0,1;0rad)
  Radius = 1.5
FEATURE [Part::Cylinder] Cylinder2311  label="Válec2311"
  Angle = 360
  AttacherType = Attacher::AttachEngine3D
  Height = 20
  Placement = pos=(-7,-34,73) rot=(1,0,0;1.5708rad)
  Radius = 1.5
FEATURE [Part::Cylinder] Cylinder2312  label="Válec2312"
  Angle = 360
  AttacherType = Attacher::AttachEngine3D
  Height = 100
  Placement = pos=(39,-21,0) rot=(0,0,1;0rad)
  Radius = 1.5
FEATURE [Part::Cylinder] Cylinder2313  label="Válec2313"
  Angle = 360
  AttacherType = Attacher::AttachEngine3D
  Height = 4
  Placement = pos=(-7,-34,37) rot=(1,0,0;1.5708rad)
  Radius = 3
FEATURE [Part::Compound] Compound960
  Links = -> [Cylinder2301,Cylinder2313,Cylinder2300,Cylinder2302]
  Placement = pos=(0,141,45) rot=(1,0,0;1.5708rad)
FEATURE [Part::Cylinder] Cylinder2314  label="Válec2314"
  Angle = 360
  AttacherType = Attacher::AttachEngine3D
  Height = 4
  Placement = pos=(-7,-34,73) rot=(1,0,0;1.5708rad)
  Radius = 3
FEATURE [Part::Cylinder] Cylinder2315  label="Válec2315"
  Angle = 360
  AttacherType = Attacher::AttachEngine3D
  Height = 100
  Placement = pos=(39,-21,0) rot=(0,0,1;0rad)
  Radius = 1.5
FEATURE [Part::Cylinder] Cylinder2316  label="Válec2316"
  Angle = 360
  AttacherType = Attacher::AttachEngine3D
  Height = 100
  Placement = pos=(-51,-12,0) rot=(0,0,1;0rad)
  Radius = 1.5
FEATURE [Part::Cylinder] Cylinder2317  label="Válec2317"
  Angle = 360
  AttacherType = Attacher::AttachEngine3D
  Height = 50
  Placement = pos=(-51,6,0) rot=(0,0,1;0rad)
  Radius = 1.5
FEATURE [Part::Cylinder] Cylinder2318  label="Válec2318"
  Angle = 360
  AttacherType = Attacher::AttachEngine3D
  Height = 20
  Placement = pos=(7,-34,37) rot=(1,0,0;1.5708rad)
  Radius = 1.5
FEATURE [Part::Cylinder] Cylinder2319  label="Válec2319"
  Angle = 360
  AttacherType = Attacher::AttachEngine3D
  Height = 100
  Placement = pos=(51,-12,0) rot=(0,0,1;0rad)
  Radius = 1.5
FEATURE [Part::Cylinder] Cylinder2320  label="Válec2320"
  Angle = 360
  AttacherType = Attacher::AttachEngine3D
  Height = 32
  Placement = pos=(26,41,-42) rot=(0,0,1;0rad)
  Radius = 1.5
FEATURE [Part::Cylinder] Cylinder2321  label="Válec2321"
  Angle = 360
  AttacherType = Attacher::AttachEngine3D
  Height = 100
  Placement = pos=(-39,-21,0) rot=(0,0,1;0rad)
  Radius = 1.5
FEATURE [Part::Cylinder] Cylinder2322  label="Válec2322"
  Angle = 360
  AttacherType = Attacher::AttachEngine3D
  Height = 4
  Placement = pos=(-7,-34,37) rot=(1,0,0;1.5708rad)
  Radius = 3
FEATURE [Part::Box] Box581  label="Krychle581"
  AttacherType = Attacher::AttachEngine3D
  Height = 64
  Length = 6
  Placement = pos=(11,-3,-93) rot=(0,0,1;0rad)
  Width = 6
FEATURE [Part::Cylinder] Cylinder2323  label="Válec2323"
  Angle = 360
  AttacherType = Attacher::AttachEngine3D
  Height = 100
  Placement = pos=(90,0,-60) rot=(0,0,1;0rad)
  Radius = 1.5
FEATURE [Part::Cylinder] Cylinder2324  label="Válec2324"
  Angle = 360
  AttacherType = Attacher::AttachEngine3D
  Height = 3
  Placement = pos=(78,41,-42) rot=(0,0,1;0rad)
  Radius = 3
FEATURE [Part::Cylinder] Cylinder2325  label="Válec2325"
  Angle = 360
  AttacherType = Attacher::AttachEngine3D
  Height = 100
  Placement = pos=(-39,-21,0) rot=(0,0,1;0rad)
  Radius = 1.5
FEATURE [Part::Cylinder] Cylinder2326  label="Válec2326"
  Angle = 360
  AttacherType = Attacher::AttachEngine3D
  Height = 3
  Placement = pos=(78,41,-42) rot=(0,0,1;0rad)
  Radius = 3
FEATURE [Part::Box] Box582  label="Krychle582"
  AttacherType = Attacher::AttachEngine3D
  Height = 64
  Length = 6
  Placement = pos=(87,-3,-93) rot=(0,0,1;0rad)
  Width = 6
FEATURE [Part::Cylinder] Cylinder2327  label="Válec2327"
  Angle = 360
  AttacherType = Attacher::AttachEngine3D
  Height = 3
  Placement = pos=(26,41,-42) rot=(0,0,1;0rad)
  Radius = 3
FEATURE [Part::Cylinder] Cylinder2328  label="Válec2328"
  Angle = 360
  AttacherType = Attacher::AttachEngine3D
  Height = 4
  Placement = pos=(7,-34,73) rot=(1,0,0;1.5708rad)
  Radius = 3
FEATURE [Part::Compound] Compound962
  Links = -> [Cylinder2294,Cylinder2322,Cylinder2328,Cylinder2314]
  Placement = pos=(0,160,45) rot=(1,0,0;1.5708rad)
FEATURE [Part::Cylinder] Cylinder2329  label="Válec2329"
  Angle = 360
  AttacherType = Attacher::AttachEngine3D
  Height = 50
  Placement = pos=(24,18,0) rot=(0,0,1;0rad)
  Radius = 1.5
FEATURE [Part::Cylinder] Cylinder2330  label="Válec2330"
  Angle = 360
  AttacherType = Attacher::AttachEngine3D
  Height = 100
  Placement = pos=(14,0,-60) rot=(0,0,1;0rad)
  Radius = 1.5
FEATURE [Part::Cylinder] Cylinder2331  label="Válec2331"
  Angle = 360
  AttacherType = Attacher::AttachEngine3D
  Height = 100
  Placement = pos=(14,0,-60) rot=(0,0,1;0rad)
  Radius = 1.5
FEATURE [Part::Cylinder] Cylinder2332  label="Válec2332"
  Angle = 360
  AttacherType = Attacher::AttachEngine3D
  Height = 32
  Placement = pos=(26,41,-42) rot=(0,0,1;0rad)
  Radius = 1.5
FEATURE [Part::Cylinder] Cylinder2333  label="Válec2333"
  Angle = 360
  AttacherType = Attacher::AttachEngine3D
  Height = 50
  Placement = pos=(-24,18,0) rot=(0,0,1;0rad)
  Radius = 1.5
FEATURE [Part::Cylinder] Cylinder2334  label="Válec2334"
  Angle = 360
  AttacherType = Attacher::AttachEngine3D
  Height = 32
  Placement = pos=(78,41,-42) rot=(0,0,1;0rad)
  Radius = 1.5
FEATURE [Part::Cylinder] Cylinder2335  label="Válec2335"
  Angle = 360
  AttacherType = Attacher::AttachEngine3D
  Height = 32
  Placement = pos=(78,41,-42) rot=(0,0,1;0rad)
  Radius = 1.5
FEATURE [Part::Cylinder] Cylinder2336  label="Válec2336"
  Angle = 360
  AttacherType = Attacher::AttachEngine3D
  Height = 50
  Placement = pos=(-51,6,0) rot=(0,0,1;0rad)
  Radius = 1.5
FEATURE [Part::Cylinder] Cylinder2337  label="Válec2337"
  Angle = 360
  AttacherType = Attacher::AttachEngine3D
  Height = 100
  Placement = pos=(14,0,-60) rot=(0,0,1;0rad)
  Radius = 1.5
FEATURE [Part::Cylinder] Cylinder2338  label="Válec2338"
  Angle = 360
  AttacherType = Attacher::AttachEngine3D
  Height = 50
  Placement = pos=(51,6,0) rot=(0,0,1;0rad)
  Radius = 1.5
FEATURE [Part::Cylinder] Cylinder2339  label="Válec2339"
  Angle = 360
  AttacherType = Attacher::AttachEngine3D
  Height = 100
  Placement = pos=(-51,-12,0) rot=(0,0,1;0rad)
  Radius = 1.5
FEATURE [Part::Box] Box583  label="Krychle583"
  AttacherType = Attacher::AttachEngine3D
  Height = 64
  Length = 6
  Placement = pos=(87,-3,-93) rot=(0,0,1;0rad)
  Width = 6
FEATURE [Part::Cylinder] Cylinder2340  label="Válec2340"
  Angle = 360
  AttacherType = Attacher::AttachEngine3D
  Height = 100
  Placement = pos=(90,0,-60) rot=(0,0,1;0rad)
  Radius = 1.5
FEATURE [Part::Cylinder] Cylinder2341  label="Válec2341"
  Angle = 360
  AttacherType = Attacher::AttachEngine3D
  Height = 100
  Placement = pos=(39,-21,0) rot=(0,0,1;0rad)
  Radius = 1.5
FEATURE [Part::Cylinder] Cylinder2342  label="Válec2342"
  Angle = 360
  AttacherType = Attacher::AttachEngine3D
  Height = 3
  Placement = pos=(26,41,-42) rot=(0,0,1;0rad)
  Radius = 3
FEATURE [Part::Cylinder] Cylinder2343  label="Válec2343"
  Angle = 360
  AttacherType = Attacher::AttachEngine3D
  Height = 3
  Placement = pos=(78,41,-42) rot=(0,0,1;0rad)
  Radius = 3
FEATURE [Part::Cylinder] Cylinder2344  label="Válec2344"
  Angle = 360
  AttacherType = Attacher::AttachEngine3D
  Height = 32
  Placement = pos=(78,41,-42) rot=(0,0,1;0rad)
  Radius = 1.5
FEATURE [Part::Cylinder] Cylinder2345  label="Válec2345"
  Angle = 360
  AttacherType = Attacher::AttachEngine3D
  Height = 100
  Placement = pos=(-39,-21,0) rot=(0,0,1;0rad)
  Radius = 1.5
FEATURE [Part::Cylinder] Cylinder2346  label="Válec2346"
  Angle = 360
  AttacherType = Attacher::AttachEngine3D
  Height = 100
  Placement = pos=(90,0,-60) rot=(0,0,1;0rad)
  Radius = 1.5
FEATURE [Part::Cylinder] Cylinder2347  label="Válec2347"
  Angle = 360
  AttacherType = Attacher::AttachEngine3D
  Height = 32
  Placement = pos=(26,41,-42) rot=(0,0,1;0rad)
  Radius = 1.5
FEATURE [Part::Cylinder] Cylinder2348  label="Válec2348"
  Angle = 360
  AttacherType = Attacher::AttachEngine3D
  Height = 32
  Placement = pos=(26,41,-42) rot=(0,0,1;0rad)
  Radius = 1.5
FEATURE [Part::Cylinder] Cylinder2349  label="Válec2349"
  Angle = 360
  AttacherType = Attacher::AttachEngine3D
  Height = 100
  Placement = pos=(90,0,-60) rot=(0,0,1;0rad)
  Radius = 1.5
FEATURE [Part::Box] Box584  label="Krychle584"
  AttacherType = Attacher::AttachEngine3D
  Height = 64
  Length = 6
  Placement = pos=(11,-3,-93) rot=(0,0,1;0rad)
  Width = 6
FEATURE [Part::Box] Box585  label="Krychle585"
  AttacherType = Attacher::AttachEngine3D
  Height = 64
  Length = 6
  Placement = pos=(87,-3,-93) rot=(0,0,1;0rad)
  Width = 6
FEATURE [Part::Cylinder] Cylinder2350  label="Válec2350"
  Angle = 360
  AttacherType = Attacher::AttachEngine3D
  Height = 58
  Placement = pos=(0,19,-53) rot=(1,0,0;1.5708rad)
  Radius = 60.2
FEATURE [Part::Cylinder] Cylinder2351  label="Válec2351"
  Angle = 360
  AttacherType = Attacher::AttachEngine3D
  Height = 58
  Placement = pos=(0,19,-53) rot=(1,0,0;1.5708rad)
  Radius = 60.2
FEATURE [Part::Box] Box586  label="Krychle586"
  AttacherType = Attacher::AttachEngine3D
  Height = 64
  Length = 6
  Placement = pos=(11,-3,-93) rot=(0,0,1;0rad)
  Width = 6
FEATURE [Part::Compound] Compound963
  Links = -> [Cylinder2339,Cylinder2319]
FEATURE [Part::Compound] Compound964
  Links = -> [Cylinder2306,Cylinder2317,Cylinder2309,Cylinder2298]
  Placement = pos=(0,6,0) rot=(0,0,1;0rad)
FEATURE [Part::Compound] Compound965
  Links = -> [Cylinder2318,Cylinder2297,Cylinder2307,Cylinder2303]
  Placement = pos=(0,141,45) rot=(1,0,0;1.5708rad)
FEATURE [Part::Cut] Cut566
  Base = -> Cylinder2299
  Tool = -> Compound965
FEATURE [Part::Cut] Cut563
  Base = -> Cut566
  Placement = pos=(0,19,0) rot=(0,0,1;0rad)
  Tool = -> Compound960
FEATURE [Part::Compound] Compound966
  Links = -> [Cylinder2321,Cylinder2312]
  Placement = pos=(0,-6,0) rot=(0,0,1;0rad)
FEATURE [Part::Compound] Compound967
  Links = -> [Cylinder2320,Cylinder2335]
  Placement = pos=(-52,0,36) rot=(0,0,1;0rad)
FEATURE [PartDesign::Body] Body004
  Group = -> [Sketch006,Pad004]
  Origin = -> Origin004
  Tip = -> Pad004
FEATURE [Part::Compound] Compound968
  Links = -> [Cylinder2308,Cylinder2326]
  Placement = pos=(-52,0,42) rot=(0,0,1;0rad)
FEATURE [Part::Compound] Compound969  label="srouby_troj015"
  Links = -> [Cylinder2323,Cylinder2310]
  Placement = pos=(-52,0,0) rot=(0,0,1;0rad)
FEATURE [Part::Compound] Compound970
  Links = -> [Cylinder2305,Cylinder2296,Cylinder2304,Cylinder2311]
  Placement = pos=(0,160,45) rot=(1,0,0;1.5708rad)
FEATURE [Part::Cut] Cut569
  Base = -> Body004
  Tool = -> Compound970
FEATURE [Part::Cut] Cut565
  Base = -> Cut569
  Tool = -> Compound962
FEATURE [Part::Compound] Compound971
  Links = -> [Box581,Box582]
  Placement = pos=(-52,0,36) rot=(0,0,1;0rad)
FEATURE [Part::Compound] Compound973
  Links = -> [Box586,Box585]
  Placement = pos=(-52,0,36) rot=(0,0,1;0rad)
FEATURE [Part::Compound] Compound974
  Links = -> [Cylinder2332,Cylinder2334]
  Placement = pos=(-52,0,36) rot=(0,0,1;0rad)
FEATURE [Part::Compound] Compound975
  Links = -> [Cylinder2347,Cylinder2292]
  Placement = pos=(-52,0,36) rot=(0,0,1;0rad)
FEATURE [Part::Compound] Compound977
  Links = -> [Compound969,Compound967]
FEATURE [Part::Compound] Compound978  label="srouby_troj016"
  Links = -> [Cylinder2340,Cylinder2330]
  Placement = pos=(-52,0,0) rot=(0,0,1;0rad)
FEATURE [Part::Compound] Compound976
  Links = -> [Compound978,Compound975]
FEATURE [Part::Compound] Compound980
  Links = -> [Cylinder2325,Cylinder2315]
  Placement = pos=(0,-6,0) rot=(0,0,1;0rad)
FEATURE [Part::Cut] Cut560
  Base = -> Compound959
  Tool = -> Compound980
FEATURE [Part::Cut] Cut568
  Base = -> Cut560
  Tool = -> Compound976
FEATURE [Part::Compound] Compound981
  Links = -> [Cylinder2338,Cylinder2336,Cylinder2333,Cylinder2329]
  Placement = pos=(0,6,0) rot=(0,0,1;0rad)
FEATURE [Part::Compound] Compound982
  Links = -> [Box584,Box583]
  Placement = pos=(-52,0,36) rot=(0,0,1;0rad)
FEATURE [Part::Cut] Cut556
  Base = -> Cut568
  Tool = -> Compound982
FEATURE [Part::Compound] Compound983
  Links = -> [Cylinder2345,Cylinder2341]
  Placement = pos=(0,-6,0) rot=(0,0,1;0rad)
FEATURE [Part::Compound] Compound984
  Links = -> [Compound983,Compound981,Compound963]
  Placement = pos=(0,0,-10) rot=(0,0,1;0rad)
FEATURE [Part::Cut] Cut570
  Base = -> Cut554
  Tool = -> Compound984
FEATURE [Part::Compound] Compound985
  Links = -> [Cylinder2316,Cylinder2295]
FEATURE [Part::Compound] Compound961
  Links = -> [Compound966,Compound964,Compound985]
  Placement = pos=(0,0,-10) rot=(0,0,1;0rad)
FEATURE [Part::Cut] Cut561
  Base = -> Box580
  Tool = -> Compound961
FEATURE [Part::Compound] Compound986
  Links = -> [Cylinder2327,Cylinder2324]
  Placement = pos=(-52,0,42) rot=(0,0,1;0rad)
FEATURE [Part::Cut] Cut555
  Base = -> Cut561
  Tool = -> Compound986
FEATURE [Part::Cut] Cut552
  Base = -> Cut555
  Tool = -> Compound977
FEATURE [Part::Cut] Cut558
  Base = -> Cut552
  Tool = -> Cylinder2351
FEATURE [Part::Cut] Cut562
  Base = -> Cut558
  Tool = -> Compound973
FEATURE [Part::Compound] Compound987
  Links = -> [Cylinder2348,Cylinder2344]
  Placement = pos=(-52,0,36) rot=(0,0,1;0rad)
FEATURE [Part::Compound] Compound988  label="srouby_troj017"
  Links = -> [Cylinder2346,Cylinder2331]
  Placement = pos=(-52,0,0) rot=(0,0,1;0rad)
FEATURE [Part::Compound] Compound972
  Links = -> [Compound988,Compound974]
FEATURE [Part::Cut] Cut564
  Base = -> Cut570
  Tool = -> Compound972
FEATURE [Part::Cut] Cut557
  Base = -> Cut564
  Tool = -> Compound968
FEATURE [Part::Cut] Cut571
  Base = -> Cut557
  Tool = -> Compound971
FEATURE [Part::Cut] Cut553
  Base = -> Cut571
  Tool = -> Cylinder2350
FEATURE [Part::Compound] Compound989  label="srouby_troj018"
  Links = -> [Cylinder2349,Cylinder2337]
  Placement = pos=(-52,0,0) rot=(0,0,1;0rad)
FEATURE [Part::Compound] Compound990
  Links = -> [Cylinder2342,Cylinder2343]
  Placement = pos=(-52,0,42) rot=(0,0,1;0rad)
FEATURE [Part::Cut] Cut567
  Base = -> Cut565
  Tool = -> Compound990
FEATURE [Part::Compound] Compound991
  Links = -> [Compound989,Compound987]
FEATURE [Part::Cut] Cut551
  Base = -> Cut567
  Tool = -> Compound991
FEATURE [Part::Compound] Compound979  label="Base_deep-triangle002"
  Links = -> [Cut553,Cut562,Cut551,Cut556,Cut563]
  Placement = pos=(52,0,-36) rot=(0,0,1;3.14159rad)
FEATURE [Part::Cut] Cut559
  Base = -> Compound979
  Tool = -> Cylinder2293
FEATURE [Part::Fillet] Fillet045
  Base = -> Cut559
  Edges = 1 edges r=8: [Edge47]
FEATURE [Part::Fillet] Fillet046  label="auxi1"
  Base = -> Fillet045
  Edges = 1 edges r=8: [Edge39]
FEATURE [Sketcher::SketchObject] Sketch007
  FullyConstrained = false
  MapMode = 5
  Support = -> [XY_Plane005]
  sketch-geometry (5):
    g0: LineSegment StartX=-53.11 StartY=25.5869 StartZ=0 EndX=-9.47198 EndY=128.297 EndZ=0
    g1: LineSegment StartX=-9.47198 StartY=128.297 StartZ=0 EndX=9.50803 EndY=128.154 EndZ=0
    g2: LineSegment StartX=9.50803 StartY=128.154 StartZ=0 EndX=53.1093 EndY=25.7412 EndZ=0
    g3: LineSegment StartX=53.1093 StartY=25.7412 StartZ=0 EndX=-0.067027 EndY=50.049 EndZ=0
    g4: LineSegment StartX=-0.067027 StartY=50.049 StartZ=0 EndX=-53.11 EndY=25.5869 EndZ=0
  constraints (5):
    c: Coincident(g0,g1)
    c: Coincident(g1,g2)
    c: Coincident(g2,g3)
    c: Coincident(g3,g4)
    c: Coincident(g4,g0)
FEATURE [PartDesign::Pad] Pad005
  Direction = (1,1,1)
  Length = 10
  Length2 = 100
  Profile = -> Sketch007
  Type = 0
FEATURE [Part::Cylinder] Cylinder2352  label="Válec2352"
  Angle = 360
  AttacherType = Attacher::AttachEngine3D
  Height = 32
  Placement = pos=(78,41,-42) rot=(0,0,1;0rad)
  Radius = 1.5
FEATURE [Part::Cylinder] Cylinder2353  label="Válec2353"
  Angle = 360
  AttacherType = Attacher::AttachEngine3D
  Height = 160
  Placement = pos=(-18,0,-60) rot=(0,0,1;0rad)
  Radius = 17
FEATURE [Part::Cylinder] Cylinder2354  label="Válec2354"
  Angle = 360
  AttacherType = Attacher::AttachEngine3D
  Height = 4
  Placement = pos=(7,-34,37) rot=(1,0,0;1.5708rad)
  Radius = 3
FEATURE [Part::Cylinder] Cylinder2355  label="Válec2355"
  Angle = 360
  AttacherType = Attacher::AttachEngine3D
  Height = 100
  Placement = pos=(51,-12,0) rot=(0,0,1;0rad)
  Radius = 1.5
FEATURE [Part::Box] Box588  label="Krychle588"
  AttacherType = Attacher::AttachEngine3D
  Height = 10
  Length = 10
  Placement = pos=(32,-24,0) rot=(0,0,1;0rad)
  Width = 52
FEATURE [Part::Cylinder] Cylinder2356  label="Válec2356"
  Angle = 360
  AttacherType = Attacher::AttachEngine3D
  Height = 20
  Placement = pos=(-7,-34,37) rot=(1,0,0;1.5708rad)
  Radius = 1.5
FEATURE [Part::Cylinder] Cylinder2357  label="Válec2357"
  Angle = 360
  AttacherType = Attacher::AttachEngine3D
  Height = 20
  Placement = pos=(-7,-34,37) rot=(1,0,0;1.5708rad)
  Radius = 1.5
FEATURE [Part::Cylinder] Cylinder2358  label="Válec2358"
  Angle = 360
  AttacherType = Attacher::AttachEngine3D
  Height = 50
  Placement = pos=(24,18,0) rot=(0,0,1;0rad)
  Radius = 1.5
FEATURE [Part::FeaturePython] Tube096  # WARN: FeaturePython — macro-defined, semantics opaque (R4)
  AttacherType = Attacher::AttachEngine3D
  Height = 10
  InnerRadius = 40
  OuterRadius = 59
FEATURE [Part::Cylinder] Cylinder2359  label="Válec2359"
  Angle = 360
  AttacherType = Attacher::AttachEngine3D
  Height = 10
  Placement = pos=(0,106,0) rot=(0,0,1;0rad)
  Radius = 10
FEATURE [Part::Box] Box589  label="Krychle589"
  AttacherType = Attacher::AttachEngine3D
  Height = 10
  Length = 10
  Placement = pos=(-42,-24,0) rot=(0,0,1;0rad)
  Width = 52
FEATURE [Part::Compound] Compound993
  Links = -> [Box588,Box589]
FEATURE [Part::Box] Box590  label="Krychle590"
  AttacherType = Attacher::AttachEngine3D
  Height = 32
  Length = 200
  Placement = pos=(-100,-130,0) rot=(0,0,1;0rad)
  Width = 100
FEATURE [Part::Cut] Cut575
  Base = -> Tube096
  Tool = -> Box590
FEATURE [Part::Cylinder] Cylinder2360  label="Válec2360"
  Angle = 360
  AttacherType = Attacher::AttachEngine3D
  Height = 4
  Placement = pos=(7,-34,73) rot=(1,0,0;1.5708rad)
  Radius = 3
FEATURE [Part::Cylinder] Cylinder2361  label="Válec2361"
  Angle = 360
  AttacherType = Attacher::AttachEngine3D
  Height = 4
  Placement = pos=(7,-34,37) rot=(1,0,0;1.5708rad)
  Radius = 3
FEATURE [Part::Cylinder] Cylinder2362  label="Válec2362"
  Angle = 360
  AttacherType = Attacher::AttachEngine3D
  Height = 4
  Placement = pos=(-7,-34,73) rot=(1,0,0;1.5708rad)
  Radius = 3
FEATURE [Part::Cylinder] Cylinder2363  label="Válec2363"
  Angle = 360
  AttacherType = Attacher::AttachEngine3D
  Height = 20
  Placement = pos=(-7,-34,73) rot=(1,0,0;1.5708rad)
  Radius = 1.5
FEATURE [Part::Cylinder] Cylinder2364  label="Válec2364"
  Angle = 360
  AttacherType = Attacher::AttachEngine3D
  Height = 20
  Placement = pos=(7,-34,73) rot=(1,0,0;1.5708rad)
  Radius = 1.5
FEATURE [Part::Cylinder] Cylinder2365  label="Válec2365"
  Angle = 360
  AttacherType = Attacher::AttachEngine3D
  Height = 20
  Placement = pos=(7,-34,37) rot=(1,0,0;1.5708rad)
  Radius = 1.5
FEATURE [Part::Cylinder] Cylinder2366  label="Válec2366"
  Angle = 360
  AttacherType = Attacher::AttachEngine3D
  Height = 50
  Placement = pos=(51,6,0) rot=(0,0,1;0rad)
  Radius = 1.5
FEATURE [Part::Box] Box591  label="Krychle591"
  AttacherType = Attacher::AttachEngine3D
  Height = 10
  Length = 72
  Placement = pos=(-36,-30,0) rot=(0,0,1;0rad)
  Width = 70
FEATURE [Part::Cylinder] Cylinder2367  label="Válec2367"
  Angle = 360
  AttacherType = Attacher::AttachEngine3D
  Height = 20
  Placement = pos=(7,-34,73) rot=(1,0,0;1.5708rad)
  Radius = 1.5
FEATURE [Part::Cylinder] Cylinder2368  label="Válec2368"
  Angle = 360
  AttacherType = Attacher::AttachEngine3D
  Height = 3
  Placement = pos=(26,41,-42) rot=(0,0,1;0rad)
  Radius = 3
FEATURE [Part::Cylinder] Cylinder2369  label="Válec2369"
  Angle = 360
  AttacherType = Attacher::AttachEngine3D
  Height = 50
  Placement = pos=(-24,18,0) rot=(0,0,1;0rad)
  Radius = 1.5
FEATURE [Part::Cylinder] Cylinder2370  label="Válec2370"
  Angle = 360
  AttacherType = Attacher::AttachEngine3D
  Height = 100
  Placement = pos=(14,0,-60) rot=(0,0,1;0rad)
  Radius = 1.5
FEATURE [Part::Cylinder] Cylinder2371  label="Válec2371"
  Angle = 360
  AttacherType = Attacher::AttachEngine3D
  Height = 20
  Placement = pos=(-7,-34,73) rot=(1,0,0;1.5708rad)
  Radius = 1.5
FEATURE [Part::Cylinder] Cylinder2372  label="Válec2372"
  Angle = 360
  AttacherType = Attacher::AttachEngine3D
  Height = 100
  Placement = pos=(39,-21,0) rot=(0,0,1;0rad)
  Radius = 1.5
FEATURE [Part::Cylinder] Cylinder2373  label="Válec2373"
  Angle = 360
  AttacherType = Attacher::AttachEngine3D
  Height = 4
  Placement = pos=(-7,-34,37) rot=(1,0,0;1.5708rad)
  Radius = 3
FEATURE [Part::Compound] Compound994
  Links = -> [Cylinder2361,Cylinder2373,Cylinder2360,Cylinder2362]
  Placement = pos=(0,141,45) rot=(1,0,0;1.5708rad)
FEATURE [Part::Cylinder] Cylinder2374  label="Válec2374"
  Angle = 360
  AttacherType = Attacher::AttachEngine3D
  Height = 4
  Placement = pos=(-7,-34,73) rot=(1,0,0;1.5708rad)
  Radius = 3
FEATURE [Part::Cylinder] Cylinder2375  label="Válec2375"
  Angle = 360
  AttacherType = Attacher::AttachEngine3D
  Height = 100
  Placement = pos=(39,-21,0) rot=(0,0,1;0rad)
  Radius = 1.5
FEATURE [Part::Cylinder] Cylinder2376  label="Válec2376"
  Angle = 360
  AttacherType = Attacher::AttachEngine3D
  Height = 100
  Placement = pos=(-51,-12,0) rot=(0,0,1;0rad)
  Radius = 1.5
FEATURE [Part::Cylinder] Cylinder2377  label="Válec2377"
  Angle = 360
  AttacherType = Attacher::AttachEngine3D
  Height = 50
  Placement = pos=(-51,6,0) rot=(0,0,1;0rad)
  Radius = 1.5
FEATURE [Part::Cylinder] Cylinder2378  label="Válec2378"
  Angle = 360
  AttacherType = Attacher::AttachEngine3D
  Height = 20
  Placement = pos=(7,-34,37) rot=(1,0,0;1.5708rad)
  Radius = 1.5
FEATURE [Part::Cylinder] Cylinder2379  label="Válec2379"
  Angle = 360
  AttacherType = Attacher::AttachEngine3D
  Height = 100
  Placement = pos=(51,-12,0) rot=(0,0,1;0rad)
  Radius = 1.5
FEATURE [Part::Cylinder] Cylinder2380  label="Válec2380"
  Angle = 360
  AttacherType = Attacher::AttachEngine3D
  Height = 32
  Placement = pos=(26,41,-42) rot=(0,0,1;0rad)
  Radius = 1.5
FEATURE [Part::Cylinder] Cylinder2381  label="Válec2381"
  Angle = 360
  AttacherType = Attacher::AttachEngine3D
  Height = 100
  Placement = pos=(-39,-21,0) rot=(0,0,1;0rad)
  Radius = 1.5
FEATURE [Part::Cylinder] Cylinder2382  label="Válec2382"
  Angle = 360
  AttacherType = Attacher::AttachEngine3D
  Height = 4
  Placement = pos=(-7,-34,37) rot=(1,0,0;1.5708rad)
  Radius = 3
FEATURE [Part::Box] Box592  label="Krychle592"
  AttacherType = Attacher::AttachEngine3D
  Height = 64
  Length = 6
  Placement = pos=(11,-3,-93) rot=(0,0,1;0rad)
  Width = 6
FEATURE [Part::Cylinder] Cylinder2383  label="Válec2383"
  Angle = 360
  AttacherType = Attacher::AttachEngine3D
  Height = 100
  Placement = pos=(90,0,-60) rot=(0,0,1;0rad)
  Radius = 1.5
FEATURE [Part::Cylinder] Cylinder2384  label="Válec2384"
  Angle = 360
  AttacherType = Attacher::AttachEngine3D
  Height = 3
  Placement = pos=(78,41,-42) rot=(0,0,1;0rad)
  Radius = 3
FEATURE [Part::Cylinder] Cylinder2385  label="Válec2385"
  Angle = 360
  AttacherType = Attacher::AttachEngine3D
  Height = 100
  Placement = pos=(-39,-21,0) rot=(0,0,1;0rad)
  Radius = 1.5
FEATURE [Part::Cylinder] Cylinder2386  label="Válec2386"
  Angle = 360
  AttacherType = Attacher::AttachEngine3D
  Height = 3
  Placement = pos=(78,41,-42) rot=(0,0,1;0rad)
  Radius = 3
FEATURE [Part::Box] Box593  label="Krychle593"
  AttacherType = Attacher::AttachEngine3D
  Height = 64
  Length = 6
  Placement = pos=(87,-3,-93) rot=(0,0,1;0rad)
  Width = 6
FEATURE [Part::Cylinder] Cylinder2387  label="Válec2387"
  Angle = 360
  AttacherType = Attacher::AttachEngine3D
  Height = 3
  Placement = pos=(26,41,-42) rot=(0,0,1;0rad)
  Radius = 3
FEATURE [Part::Cylinder] Cylinder2388  label="Válec2388"
  Angle = 360
  AttacherType = Attacher::AttachEngine3D
  Height = 4
  Placement = pos=(7,-34,73) rot=(1,0,0;1.5708rad)
  Radius = 3
FEATURE [Part::Compound] Compound996
  Links = -> [Cylinder2354,Cylinder2382,Cylinder2388,Cylinder2374]
  Placement = pos=(0,160,45) rot=(1,0,0;1.5708rad)
FEATURE [Part::Cylinder] Cylinder2389  label="Válec2389"
  Angle = 360
  AttacherType = Attacher::AttachEngine3D
  Height = 50
  Placement = pos=(24,18,0) rot=(0,0,1;0rad)
  Radius = 1.5
FEATURE [Part::Cylinder] Cylinder2390  label="Válec2390"
  Angle = 360
  AttacherType = Attacher::AttachEngine3D
  Height = 100
  Placement = pos=(14,0,-60) rot=(0,0,1;0rad)
  Radius = 1.5
FEATURE [Part::Cylinder] Cylinder2391  label="Válec2391"
  Angle = 360
  AttacherType = Attacher::AttachEngine3D
  Height = 100
  Placement = pos=(14,0,-60) rot=(0,0,1;0rad)
  Radius = 1.5
FEATURE [Part::Cylinder] Cylinder2392  label="Válec2392"
  Angle = 360
  AttacherType = Attacher::AttachEngine3D
  Height = 32
  Placement = pos=(26,41,-42) rot=(0,0,1;0rad)
  Radius = 1.5
FEATURE [Part::Cylinder] Cylinder2393  label="Válec2393"
  Angle = 360
  AttacherType = Attacher::AttachEngine3D
  Height = 50
  Placement = pos=(-24,18,0) rot=(0,0,1;0rad)
  Radius = 1.5
FEATURE [Part::Cylinder] Cylinder2394  label="Válec2394"
  Angle = 360
  AttacherType = Attacher::AttachEngine3D
  Height = 32
  Placement = pos=(78,41,-42) rot=(0,0,1;0rad)
  Radius = 1.5
FEATURE [Part::Cylinder] Cylinder2395  label="Válec2395"
  Angle = 360
  AttacherType = Attacher::AttachEngine3D
  Height = 32
  Placement = pos=(78,41,-42) rot=(0,0,1;0rad)
  Radius = 1.5
FEATURE [Part::Cylinder] Cylinder2396  label="Válec2396"
  Angle = 360
  AttacherType = Attacher::AttachEngine3D
  Height = 50
  Placement = pos=(-51,6,0) rot=(0,0,1;0rad)
  Radius = 1.5
FEATURE [Part::Cylinder] Cylinder2397  label="Válec2397"
  Angle = 360
  AttacherType = Attacher::AttachEngine3D
  Height = 100
  Placement = pos=(14,0,-60) rot=(0,0,1;0rad)
  Radius = 1.5
FEATURE [Part::Cylinder] Cylinder2398  label="Válec2398"
  Angle = 360
  AttacherType = Attacher::AttachEngine3D
  Height = 50
  Placement = pos=(51,6,0) rot=(0,0,1;0rad)
  Radius = 1.5
FEATURE [Part::Cylinder] Cylinder2399  label="Válec2399"
  Angle = 360
  AttacherType = Attacher::AttachEngine3D
  Height = 100
  Placement = pos=(-51,-12,0) rot=(0,0,1;0rad)
  Radius = 1.5
FEATURE [Part::Box] Box594  label="Krychle594"
  AttacherType = Attacher::AttachEngine3D
  Height = 64
  Length = 6
  Placement = pos=(87,-3,-93) rot=(0,0,1;0rad)
  Width = 6
FEATURE [Part::Cylinder] Cylinder2400  label="Válec2400"
  Angle = 360
  AttacherType = Attacher::AttachEngine3D
  Height = 100
  Placement = pos=(90,0,-60) rot=(0,0,1;0rad)
  Radius = 1.5
FEATURE [Part::Cylinder] Cylinder2401  label="Válec2401"
  Angle = 360
  AttacherType = Attacher::AttachEngine3D
  Height = 100
  Placement = pos=(39,-21,0) rot=(0,0,1;0rad)
  Radius = 1.5
FEATURE [Part::Cylinder] Cylinder2402  label="Válec2402"
  Angle = 360
  AttacherType = Attacher::AttachEngine3D
  Height = 3
  Placement = pos=(26,41,-42) rot=(0,0,1;0rad)
  Radius = 3
FEATURE [Part::Cylinder] Cylinder2403  label="Válec2403"
  Angle = 360
  AttacherType = Attacher::AttachEngine3D
  Height = 3
  Placement = pos=(78,41,-42) rot=(0,0,1;0rad)
  Radius = 3
FEATURE [Part::Cylinder] Cylinder2404  label="Válec2404"
  Angle = 360
  AttacherType = Attacher::AttachEngine3D
  Height = 32
  Placement = pos=(78,41,-42) rot=(0,0,1;0rad)
  Radius = 1.5
FEATURE [Part::Cylinder] Cylinder2405  label="Válec2405"
  Angle = 360
  AttacherType = Attacher::AttachEngine3D
  Height = 100
  Placement = pos=(-39,-21,0) rot=(0,0,1;0rad)
  Radius = 1.5
FEATURE [Part::Cylinder] Cylinder2406  label="Válec2406"
  Angle = 360
  AttacherType = Attacher::AttachEngine3D
  Height = 100
  Placement = pos=(90,0,-60) rot=(0,0,1;0rad)
  Radius = 1.5
FEATURE [Part::Cylinder] Cylinder2407  label="Válec2407"
  Angle = 360
  AttacherType = Attacher::AttachEngine3D
  Height = 32
  Placement = pos=(26,41,-42) rot=(0,0,1;0rad)
  Radius = 1.5
FEATURE [Part::Cylinder] Cylinder2408  label="Válec2408"
  Angle = 360
  AttacherType = Attacher::AttachEngine3D
  Height = 32
  Placement = pos=(26,41,-42) rot=(0,0,1;0rad)
  Radius = 1.5
FEATURE [Part::Cylinder] Cylinder2409  label="Válec2409"
  Angle = 360
  AttacherType = Attacher::AttachEngine3D
  Height = 100
  Placement = pos=(90,0,-60) rot=(0,0,1;0rad)
  Radius = 1.5
FEATURE [Part::Box] Box595  label="Krychle595"
  AttacherType = Attacher::AttachEngine3D
  Height = 64
  Length = 6
  Placement = pos=(11,-3,-93) rot=(0,0,1;0rad)
  Width = 6
FEATURE [Part::Box] Box596  label="Krychle596"
  AttacherType = Attacher::AttachEngine3D
  Height = 64
  Length = 6
  Placement = pos=(87,-3,-93) rot=(0,0,1;0rad)
  Width = 6
FEATURE [Part::Cylinder] Cylinder2410  label="Válec2410"
  Angle = 360
  AttacherType = Attacher::AttachEngine3D
  Height = 58
  Placement = pos=(0,19,-53) rot=(1,0,0;1.5708rad)
  Radius = 60.2
FEATURE [Part::Cylinder] Cylinder2411  label="Válec2411"
  Angle = 360
  AttacherType = Attacher::AttachEngine3D
  Height = 58
  Placement = pos=(0,19,-53) rot=(1,0,0;1.5708rad)
  Radius = 60.2
FEATURE [Part::Box] Box597  label="Krychle597"
  AttacherType = Attacher::AttachEngine3D
  Height = 64
  Length = 6
  Placement = pos=(11,-3,-93) rot=(0,0,1;0rad)
  Width = 6
FEATURE [Part::Compound] Compound997
  Links = -> [Cylinder2399,Cylinder2379]
FEATURE [Part::Compound] Compound998
  Links = -> [Cylinder2366,Cylinder2377,Cylinder2369,Cylinder2358]
  Placement = pos=(0,6,0) rot=(0,0,1;0rad)
FEATURE [Part::Compound] Compound999
  Links = -> [Cylinder2378,Cylinder2357,Cylinder2367,Cylinder2363]
  Placement = pos=(0,141,45) rot=(1,0,0;1.5708rad)
FEATURE [Part::Compound] Compound1000
  Links = -> [Cylinder2381,Cylinder2372]
  Placement = pos=(0,-6,0) rot=(0,0,1;0rad)
FEATURE [Part::Compound] Compound1001
  Links = -> [Cylinder2380,Cylinder2395]
  Placement = pos=(-52,0,36) rot=(0,0,1;0rad)
FEATURE [Part::Compound] Compound1002
  Links = -> [Cylinder2368,Cylinder2386]
  Placement = pos=(-52,0,42) rot=(0,0,1;0rad)
FEATURE [Part::Compound] Compound1003  label="srouby_troj019"
  Links = -> [Cylinder2383,Cylinder2370]
  Placement = pos=(-52,0,0) rot=(0,0,1;0rad)
FEATURE [Part::Compound] Compound1004
  Links = -> [Cylinder2365,Cylinder2356,Cylinder2364,Cylinder2371]
  Placement = pos=(0,160,45) rot=(1,0,0;1.5708rad)
FEATURE [Part::Compound] Compound1005
  Links = -> [Box592,Box593]
  Placement = pos=(-52,0,36) rot=(0,0,1;0rad)
FEATURE [Part::Compound] Compound1007
  Links = -> [Box597,Box596]
  Placement = pos=(-52,0,36) rot=(0,0,1;0rad)
FEATURE [Part::Compound] Compound1008
  Links = -> [Cylinder2392,Cylinder2394]
  Placement = pos=(-52,0,36) rot=(0,0,1;0rad)
FEATURE [Part::Compound] Compound1009
  Links = -> [Cylinder2407,Cylinder2352]
  Placement = pos=(-52,0,36) rot=(0,0,1;0rad)
FEATURE [Part::Compound] Compound1011
  Links = -> [Compound1003,Compound1001]
FEATURE [Part::Compound] Compound1012  label="srouby_troj020"
  Links = -> [Cylinder2400,Cylinder2390]
  Placement = pos=(-52,0,0) rot=(0,0,1;0rad)
FEATURE [Part::Compound] Compound1010
  Links = -> [Compound1012,Compound1009]
FEATURE [Part::Compound] Compound1014
  Links = -> [Cylinder2385,Cylinder2375]
  Placement = pos=(0,-6,0) rot=(0,0,1;0rad)
FEATURE [Part::Cut] Cut581
  Base = -> Compound993
  Tool = -> Compound1014
FEATURE [Part::Cut] Cut589
  Base = -> Cut581
  Tool = -> Compound1010
FEATURE [Part::Compound] Compound1015
  Links = -> [Cylinder2398,Cylinder2396,Cylinder2393,Cylinder2389]
  Placement = pos=(0,6,0) rot=(0,0,1;0rad)
FEATURE [Part::Compound] Compound1016
  Links = -> [Box595,Box594]
  Placement = pos=(-52,0,36) rot=(0,0,1;0rad)
FEATURE [Part::Cut] Cut577
  Base = -> Cut589
  Placement = pos=(52,0,-36) rot=(0,0,1;3.14159rad)
  Tool = -> Compound1016
FEATURE [Part::Compound] Compound1017
  Links = -> [Cylinder2405,Cylinder2401]
  Placement = pos=(0,-6,0) rot=(0,0,1;0rad)
FEATURE [Part::Compound] Compound1018
  Links = -> [Compound1017,Compound1015,Compound997]
  Placement = pos=(0,0,-10) rot=(0,0,1;0rad)
FEATURE [Part::Cut] Cut591
  Base = -> Cut575
  Tool = -> Compound1018
FEATURE [Part::Compound] Compound1019
  Links = -> [Cylinder2376,Cylinder2355]
FEATURE [Part::Compound] Compound995
  Links = -> [Compound1000,Compound998,Compound1019]
  Placement = pos=(0,0,-10) rot=(0,0,1;0rad)
FEATURE [Part::Cut] Cut582
  Base = -> Box591
  Tool = -> Compound995
FEATURE [Part::Compound] Compound1020
  Links = -> [Cylinder2387,Cylinder2384]
  Placement = pos=(-52,0,42) rot=(0,0,1;0rad)
FEATURE [Part::Cut] Cut576
  Base = -> Cut582
  Tool = -> Compound1020
FEATURE [Part::Cut] Cut573
  Base = -> Cut576
  Tool = -> Compound1011
FEATURE [Part::Cut] Cut579
  Base = -> Cut573
  Tool = -> Cylinder2411
FEATURE [Part::Cut] Cut583
  Base = -> Cut579
  Placement = pos=(52,0,-36) rot=(0,0,1;3.14159rad)
  Tool = -> Compound1007
FEATURE [PartDesign::Body] Body005
  Group = -> [Sketch007,Pad005]
  Origin = -> Origin005
  Tip = -> Pad005
FEATURE [Part::Compound] Compound1021
  Links = -> [Cylinder2408,Cylinder2404]
  Placement = pos=(-52,0,36) rot=(0,0,1;0rad)
FEATURE [Part::Compound] Compound1022  label="srouby_troj021"
  Links = -> [Cylinder2406,Cylinder2391]
  Placement = pos=(-52,0,0) rot=(0,0,1;0rad)
FEATURE [Part::Compound] Compound1006
  Links = -> [Compound1022,Compound1008]
FEATURE [Part::Cut] Cut585
  Base = -> Cut591
  Tool = -> Compound1006
FEATURE [Part::Cut] Cut578
  Base = -> Cut585
  Tool = -> Compound1002
FEATURE [Part::Cut] Cut592
  Base = -> Cut578
  Tool = -> Compound1005
FEATURE [Part::Cut] Cut574
  Base = -> Cut592
  Placement = pos=(52,0,-36) rot=(0,0,1;3.14159rad)
  Tool = -> Cylinder2410
FEATURE [Part::Compound] Compound1023  label="srouby_troj022"
  Links = -> [Cylinder2409,Cylinder2397]
  Placement = pos=(-52,0,0) rot=(0,0,1;0rad)
FEATURE [Part::Compound] Compound1024
  Links = -> [Cylinder2402,Cylinder2403]
  Placement = pos=(-52,0,42) rot=(0,0,1;0rad)
FEATURE [Part::Compound] Compound1025
  Links = -> [Compound1023,Compound1021]
FEATURE [Part::Box] Box587  label="Krychle587"
  AttacherType = Attacher::AttachEngine3D
  Height = 49
  Length = 4
  Placement = pos=(59,-7.5,20) rot=(0,0,1;0rad)
  Width = 15
FEATURE [Part::Chamfer] Chamfer049
  Base = -> Box587
  Edges = 2 edges r=3: [Edge5,Edge7]
  Placement = pos=(0,0,0) rot=(0,0,-1;0.785398rad)
FEATURE [Part::Chamfer] Chamfer050
  Base = -> Box587
  Edges = 2 edges r=3: [Edge5,Edge7]
  Placement = pos=(0,0,0) rot=(0,0,-1;1.5708rad)
FEATURE [Part::Chamfer] Chamfer051
  Base = -> Box587
  Edges = 2 edges r=3: [Edge5,Edge7]
  Placement = pos=(0,0,0) rot=(0,0,1;3.92699rad)
FEATURE [Part::Chamfer] Chamfer052
  Base = -> Box587
  Edges = 2 edges r=3: [Edge5,Edge7]
  Placement = pos=(0,0,0) rot=(0,0,1;3.14159rad)
FEATURE [Part::Chamfer] Chamfer053
  Base = -> Box587
  Edges = 2 edges r=3: [Edge5,Edge7]
  Placement = pos=(0,0,0) rot=(0,0,1;2.35619rad)
FEATURE [Part::Chamfer] Chamfer054
  Base = -> Box587
  Edges = 2 edges r=3: [Edge5,Edge7]
  Placement = pos=(0,0,0) rot=(0,0,1;1.5708rad)
FEATURE [Part::Chamfer] Chamfer055
  Base = -> Box587
  Edges = 2 edges r=3: [Edge5,Edge7]
  Placement = pos=(0,0,0) rot=(0,0,1;0.785398rad)
FEATURE [Part::Chamfer] Chamfer056
  Base = -> Box587
  Edges = 2 edges r=3: [Edge5,Edge7]
FEATURE [Part::Compound] Compound992
  Links = -> [Chamfer055,Chamfer054,Chamfer053,Chamfer052,Chamfer051,Chamfer050,Chamfer049,Chamfer056]
  Placement = pos=(52,-39,-89) rot=(-1,0,0;1.5708rad)
FEATURE [Part::Cut] Cut593
  Base = -> Cut574
  Tool = -> Cylinder2353
FEATURE [Part::Fillet] Fillet047
  Base = -> Cut593
  Edges = 2 edges r=8: [Edge1,Edge47]
FEATURE [Part::Cut] Cut594
  Base = -> Cut583
  Tool = -> Compound992
FEATURE [Part::Chamfer] Chamfer057
  Base = -> Cylinder2359
  Edges = 1 edges r=2: [Edge1]
FEATURE [Part::Cut] Cut595
  Base = -> Chamfer057
  Tool = -> Compound994
FEATURE [Part::Cut] Cut596
  Base = -> Cut595
  Placement = pos=(52,-19,-36) rot=(0,0,1;3.14159rad)
  Tool = -> Compound999
FEATURE [Part::Chamfer] Chamfer058
  Base = -> Pad005
  Edges = 1 edges r=2: [Edge10]
FEATURE [Part::Chamfer] Chamfer059
  Base = -> Chamfer058
  Edges = 1 edges r=2: [Edge16]
FEATURE [Part::Cut] Cut597
  Base = -> Chamfer059
  Tool = -> Compound1025
FEATURE [Part::Cut] Cut598
  Base = -> Cut597
  Tool = -> Compound1024
FEATURE [Part::Cut] Cut599
  Base = -> Cut598
  Tool = -> Compound996
FEATURE [Part::Cut] Cut600
  Base = -> Cut599
  Placement = pos=(52,0,-36) rot=(0,0,1;3.14159rad)
  Tool = -> Compound1004
FEATURE [Part::Compound] Compound1026  label="Base-deep-thin_trinagle-holed_v1.0"
  Links = -> [Cut577,Fillet047,Cut594,Cut596,Cut600]
FEATURE [Mesh::Feature] Mesh001  label="Base-deep-thin_trinagle-holed_v1.0 (Meshed)"
